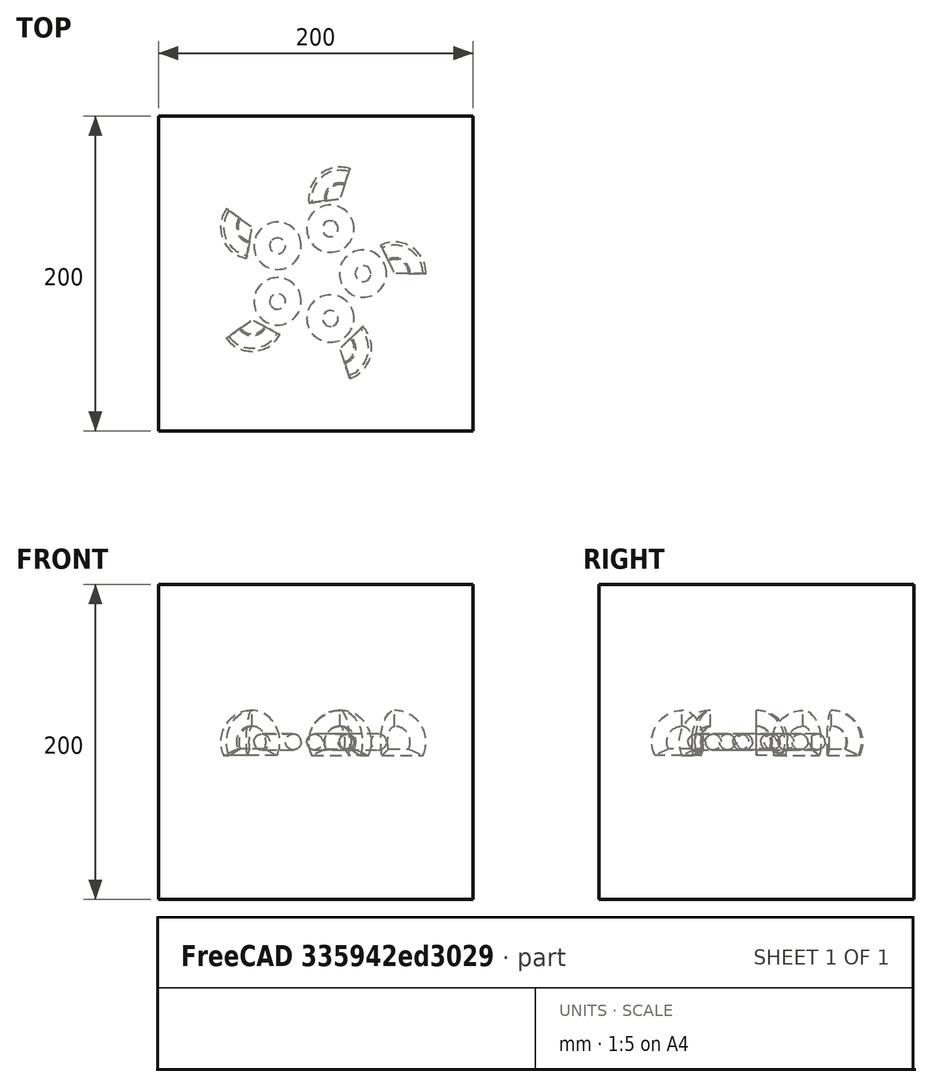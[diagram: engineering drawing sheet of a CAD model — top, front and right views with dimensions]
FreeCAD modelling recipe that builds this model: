
FCSTD DOCUMENT  (FreeCAD 1.0R39109 (Git))
Label: arrayTest-7
License: All rights reserved
LicenseURL: http://en.wikipedia.org/wiki/All_rights_reserved
objects: App::DocumentObjectGroupPython×1248, Part::FeaturePython×4, App::Part×2, Part::MultiFuse×1
note: 5 computed .brp shape members not serialized (recipe doc carries the construction recipe); baked Part::Feature solids carry a one-line shape summary decoded from their .brp

FEATURE [App::DocumentObjectGroupPython] HALFPI  # scripted group (container) (typed FeaturePython)
  name = HALFPI
  value = pi/2.
FEATURE [App::DocumentObjectGroupPython] PI  # scripted group (container) (typed FeaturePython)
  name = PI
  value = 1.*pi
FEATURE [App::DocumentObjectGroupPython] TWOPI  # scripted group (container) (typed FeaturePython)
  name = TWOPI
  value = 2.*pi
FEATURE [App::DocumentObjectGroupPython] Constants  # scripted group (container) (typed FeaturePython)
  Group = -> [HALFPI,PI,TWOPI]
FEATURE [App::DocumentObjectGroupPython] Variables  # scripted group (container) (typed FeaturePython)
FEATURE [App::DocumentObjectGroupPython] Quantities  # scripted group (container) (typed FeaturePython)
FEATURE [App::DocumentObjectGroupPython] Isotopes  # scripted group (container) (typed FeaturePython)
FEATURE [App::DocumentObjectGroupPython] Elements  # scripted group (container) (typed FeaturePython)
FEATURE [App::DocumentObjectGroupPython] G4Isotopes  # scripted group (container) (typed FeaturePython)
FEATURE [App::DocumentObjectGroupPython] H_element  # scripted group (container) (typed FeaturePython)
  Z = 1
  atom_value = 1.008
  formula = H
  name = H_element
FEATURE [App::DocumentObjectGroupPython] He_element  # scripted group (container) (typed FeaturePython)
  Z = 2
  atom_value = 4.0026
  formula = He
  name = He_element
FEATURE [App::DocumentObjectGroupPython] Li_element  # scripted group (container) (typed FeaturePython)
  Z = 3
  atom_value = 6.94
  formula = Li
  name = Li_element
FEATURE [App::DocumentObjectGroupPython] Be_element  # scripted group (container) (typed FeaturePython)
  Z = 4
  atom_value = 9.01218
  formula = Be
  name = Be_element
FEATURE [App::DocumentObjectGroupPython] B_element  # scripted group (container) (typed FeaturePython)
  Z = 5
  atom_value = 10.81
  formula = B
  name = B_element
FEATURE [App::DocumentObjectGroupPython] C_element  # scripted group (container) (typed FeaturePython)
  Z = 6
  atom_value = 12.011
  formula = C
  name = C_element
FEATURE [App::DocumentObjectGroupPython] N_element  # scripted group (container) (typed FeaturePython)
  Z = 7
  atom_value = 14.007
  formula = N
  name = N_element
FEATURE [App::DocumentObjectGroupPython] O_element  # scripted group (container) (typed FeaturePython)
  Z = 8
  atom_value = 15.999
  formula = O
  name = O_element
FEATURE [App::DocumentObjectGroupPython] F_element  # scripted group (container) (typed FeaturePython)
  Z = 9
  atom_value = 18.9984
  formula = F
  name = F_element
FEATURE [App::DocumentObjectGroupPython] Ne_element  # scripted group (container) (typed FeaturePython)
  Z = 10
  atom_value = 20.1797
  formula = Ne
  name = Ne_element
FEATURE [App::DocumentObjectGroupPython] Na_element  # scripted group (container) (typed FeaturePython)
  Z = 11
  atom_value = 22.9898
  formula = Na
  name = Na_element
FEATURE [App::DocumentObjectGroupPython] Mg_element  # scripted group (container) (typed FeaturePython)
  Z = 12
  atom_value = 24.305
  formula = Mg
  name = Mg_element
FEATURE [App::DocumentObjectGroupPython] Al_element  # scripted group (container) (typed FeaturePython)
  Z = 13
  atom_value = 26.9815
  formula = Al
  name = Al_element
FEATURE [App::DocumentObjectGroupPython] Si_element  # scripted group (container) (typed FeaturePython)
  Z = 14
  atom_value = 28.085
  formula = Si
  name = Si_element
FEATURE [App::DocumentObjectGroupPython] P_element  # scripted group (container) (typed FeaturePython)
  Z = 15
  atom_value = 30.9738
  formula = P
  name = P_element
FEATURE [App::DocumentObjectGroupPython] S_element  # scripted group (container) (typed FeaturePython)
  Z = 16
  atom_value = 32.06
  formula = S
  name = S_element
FEATURE [App::DocumentObjectGroupPython] Cl_element  # scripted group (container) (typed FeaturePython)
  Z = 17
  atom_value = 35.45
  formula = Cl
  name = Cl_element
FEATURE [App::DocumentObjectGroupPython] Ar_element  # scripted group (container) (typed FeaturePython)
  Z = 18
  atom_value = 39.95
  formula = Ar
  name = Ar_element
FEATURE [App::DocumentObjectGroupPython] K_element  # scripted group (container) (typed FeaturePython)
  Z = 19
  atom_value = 39.0983
  formula = K
  name = K_element
FEATURE [App::DocumentObjectGroupPython] Ca_element  # scripted group (container) (typed FeaturePython)
  Z = 20
  atom_value = 40.078
  formula = Ca
  name = Ca_element
FEATURE [App::DocumentObjectGroupPython] Sc_element  # scripted group (container) (typed FeaturePython)
  Z = 21
  atom_value = 44.9559
  formula = Sc
  name = Sc_element
FEATURE [App::DocumentObjectGroupPython] Ti_element  # scripted group (container) (typed FeaturePython)
  Z = 22
  atom_value = 47.867
  formula = Ti
  name = Ti_element
FEATURE [App::DocumentObjectGroupPython] V_element  # scripted group (container) (typed FeaturePython)
  Z = 23
  atom_value = 50.9415
  formula = V
  name = V_element
FEATURE [App::DocumentObjectGroupPython] Cr_element  # scripted group (container) (typed FeaturePython)
  Z = 24
  atom_value = 51.9961
  formula = Cr
  name = Cr_element
FEATURE [App::DocumentObjectGroupPython] Mn_element  # scripted group (container) (typed FeaturePython)
  Z = 25
  atom_value = 54.938
  formula = Mn
  name = Mn_element
FEATURE [App::DocumentObjectGroupPython] Fe_element  # scripted group (container) (typed FeaturePython)
  Z = 26
  atom_value = 55.845
  formula = Fe
  name = Fe_element
FEATURE [App::DocumentObjectGroupPython] Co_element  # scripted group (container) (typed FeaturePython)
  Z = 27
  atom_value = 58.9332
  formula = Co
  name = Co_element
FEATURE [App::DocumentObjectGroupPython] Ni_element  # scripted group (container) (typed FeaturePython)
  Z = 28
  atom_value = 58.6934
  formula = Ni
  name = Ni_element
FEATURE [App::DocumentObjectGroupPython] Cu_element  # scripted group (container) (typed FeaturePython)
  Z = 29
  atom_value = 63.546
  formula = Cu
  name = Cu_element
FEATURE [App::DocumentObjectGroupPython] Zn_element  # scripted group (container) (typed FeaturePython)
  Z = 30
  atom_value = 65.38
  formula = Zn
  name = Zn_element
FEATURE [App::DocumentObjectGroupPython] Ga_element  # scripted group (container) (typed FeaturePython)
  Z = 31
  atom_value = 69.723
  formula = Ga
  name = Ga_element
FEATURE [App::DocumentObjectGroupPython] Ge_element  # scripted group (container) (typed FeaturePython)
  Z = 32
  atom_value = 72.63
  formula = Ge
  name = Ge_element
FEATURE [App::DocumentObjectGroupPython] As_element  # scripted group (container) (typed FeaturePython)
  Z = 33
  atom_value = 74.9216
  formula = As
  name = As_element
FEATURE [App::DocumentObjectGroupPython] Se_element  # scripted group (container) (typed FeaturePython)
  Z = 34
  atom_value = 78.971
  formula = Se
  name = Se_element
FEATURE [App::DocumentObjectGroupPython] Br_element  # scripted group (container) (typed FeaturePython)
  Z = 35
  atom_value = 79.904
  formula = Br
  name = Br_element
FEATURE [App::DocumentObjectGroupPython] Kr_element  # scripted group (container) (typed FeaturePython)
  Z = 36
  atom_value = 83.798
  formula = Kr
  name = Kr_element
FEATURE [App::DocumentObjectGroupPython] Rb_element  # scripted group (container) (typed FeaturePython)
  Z = 37
  atom_value = 85.4678
  formula = Rb
  name = Rb_element
FEATURE [App::DocumentObjectGroupPython] Sr_element  # scripted group (container) (typed FeaturePython)
  Z = 38
  atom_value = 87.62
  formula = Sr
  name = Sr_element
FEATURE [App::DocumentObjectGroupPython] Y_element  # scripted group (container) (typed FeaturePython)
  Z = 39
  atom_value = 88.9058
  formula = Y
  name = Y_element
FEATURE [App::DocumentObjectGroupPython] Zr_element  # scripted group (container) (typed FeaturePython)
  Z = 40
  atom_value = 91.224
  formula = Zr
  name = Zr_element
FEATURE [App::DocumentObjectGroupPython] Nb_element  # scripted group (container) (typed FeaturePython)
  Z = 41
  atom_value = 92.9064
  formula = Nb
  name = Nb_element
FEATURE [App::DocumentObjectGroupPython] Mo_element  # scripted group (container) (typed FeaturePython)
  Z = 42
  atom_value = 95.95
  formula = Mo
  name = Mo_element
FEATURE [App::DocumentObjectGroupPython] Tc_element  # scripted group (container) (typed FeaturePython)
  Z = 43
  atom_value = 97
  formula = Tc
  name = Tc_element
FEATURE [App::DocumentObjectGroupPython] Ru_element  # scripted group (container) (typed FeaturePython)
  Z = 44
  atom_value = 101.07
  formula = Ru
  name = Ru_element
FEATURE [App::DocumentObjectGroupPython] Rh_element  # scripted group (container) (typed FeaturePython)
  Z = 45
  atom_value = 102.905
  formula = Rh
  name = Rh_element
FEATURE [App::DocumentObjectGroupPython] Pd_element  # scripted group (container) (typed FeaturePython)
  Z = 46
  atom_value = 106.42
  formula = Pd
  name = Pd_element
FEATURE [App::DocumentObjectGroupPython] Ag_element  # scripted group (container) (typed FeaturePython)
  Z = 47
  atom_value = 107.868
  formula = Ag
  name = Ag_element
FEATURE [App::DocumentObjectGroupPython] Cd_element  # scripted group (container) (typed FeaturePython)
  Z = 48
  atom_value = 112.414
  formula = Cd
  name = Cd_element
FEATURE [App::DocumentObjectGroupPython] In_element  # scripted group (container) (typed FeaturePython)
  Z = 49
  atom_value = 114.818
  formula = In
  name = In_element
FEATURE [App::DocumentObjectGroupPython] Sn_element  # scripted group (container) (typed FeaturePython)
  Z = 50
  atom_value = 118.71
  formula = Sn
  name = Sn_element
FEATURE [App::DocumentObjectGroupPython] Sb_element  # scripted group (container) (typed FeaturePython)
  Z = 51
  atom_value = 121.76
  formula = Sb
  name = Sb_element
FEATURE [App::DocumentObjectGroupPython] Te_element  # scripted group (container) (typed FeaturePython)
  Z = 52
  atom_value = 127.6
  formula = Te
  name = Te_element
FEATURE [App::DocumentObjectGroupPython] I_element  # scripted group (container) (typed FeaturePython)
  Z = 53
  atom_value = 126.904
  formula = I
  name = I_element
FEATURE [App::DocumentObjectGroupPython] Xe_element  # scripted group (container) (typed FeaturePython)
  Z = 54
  atom_value = 131.293
  formula = Xe
  name = Xe_element
FEATURE [App::DocumentObjectGroupPython] Cs_element  # scripted group (container) (typed FeaturePython)
  Z = 55
  atom_value = 132.905
  formula = Cs
  name = Cs_element
FEATURE [App::DocumentObjectGroupPython] Ba_element  # scripted group (container) (typed FeaturePython)
  Z = 56
  atom_value = 137.327
  formula = Ba
  name = Ba_element
FEATURE [App::DocumentObjectGroupPython] La_element  # scripted group (container) (typed FeaturePython)
  Z = 57
  atom_value = 138.905
  formula = La
  name = La_element
FEATURE [App::DocumentObjectGroupPython] Ce_element  # scripted group (container) (typed FeaturePython)
  Z = 58
  atom_value = 140.116
  formula = Ce
  name = Ce_element
FEATURE [App::DocumentObjectGroupPython] Pr_element  # scripted group (container) (typed FeaturePython)
  Z = 59
  atom_value = 140.908
  formula = Pr
  name = Pr_element
FEATURE [App::DocumentObjectGroupPython] Nd_element  # scripted group (container) (typed FeaturePython)
  Z = 60
  atom_value = 144.242
  formula = Nd
  name = Nd_element
FEATURE [App::DocumentObjectGroupPython] Pm_element  # scripted group (container) (typed FeaturePython)
  Z = 61
  atom_value = 145
  formula = Pm
  name = Pm_element
FEATURE [App::DocumentObjectGroupPython] Sm_element  # scripted group (container) (typed FeaturePython)
  Z = 62
  atom_value = 150.36
  formula = Sm
  name = Sm_element
FEATURE [App::DocumentObjectGroupPython] Eu_element  # scripted group (container) (typed FeaturePython)
  Z = 63
  atom_value = 151.964
  formula = Eu
  name = Eu_element
FEATURE [App::DocumentObjectGroupPython] Gd_element  # scripted group (container) (typed FeaturePython)
  Z = 64
  atom_value = 157.25
  formula = Gd
  name = Gd_element
FEATURE [App::DocumentObjectGroupPython] Tb_element  # scripted group (container) (typed FeaturePython)
  Z = 65
  atom_value = 158.925
  formula = Tb
  name = Tb_element
FEATURE [App::DocumentObjectGroupPython] Dy_element  # scripted group (container) (typed FeaturePython)
  Z = 66
  atom_value = 162.5
  formula = Dy
  name = Dy_element
FEATURE [App::DocumentObjectGroupPython] Ho_element  # scripted group (container) (typed FeaturePython)
  Z = 67
  atom_value = 164.93
  formula = Ho
  name = Ho_element
FEATURE [App::DocumentObjectGroupPython] Er_element  # scripted group (container) (typed FeaturePython)
  Z = 68
  atom_value = 167.259
  formula = Er
  name = Er_element
FEATURE [App::DocumentObjectGroupPython] Tm_element  # scripted group (container) (typed FeaturePython)
  Z = 69
  atom_value = 168.934
  formula = Tm
  name = Tm_element
FEATURE [App::DocumentObjectGroupPython] Yb_element  # scripted group (container) (typed FeaturePython)
  Z = 70
  atom_value = 173.045
  formula = Yb
  name = Yb_element
FEATURE [App::DocumentObjectGroupPython] Lu_element  # scripted group (container) (typed FeaturePython)
  Z = 71
  atom_value = 174.967
  formula = Lu
  name = Lu_element
FEATURE [App::DocumentObjectGroupPython] Hf_element  # scripted group (container) (typed FeaturePython)
  Z = 72
  atom_value = 178.49
  formula = Hf
  name = Hf_element
FEATURE [App::DocumentObjectGroupPython] Ta_element  # scripted group (container) (typed FeaturePython)
  Z = 73
  atom_value = 180.948
  formula = Ta
  name = Ta_element
FEATURE [App::DocumentObjectGroupPython] W_element  # scripted group (container) (typed FeaturePython)
  Z = 74
  atom_value = 183.84
  formula = W
  name = W_element
FEATURE [App::DocumentObjectGroupPython] Re_element  # scripted group (container) (typed FeaturePython)
  Z = 75
  atom_value = 186.207
  formula = Re
  name = Re_element
FEATURE [App::DocumentObjectGroupPython] Os_element  # scripted group (container) (typed FeaturePython)
  Z = 76
  atom_value = 190.23
  formula = Os
  name = Os_element
FEATURE [App::DocumentObjectGroupPython] Ir_element  # scripted group (container) (typed FeaturePython)
  Z = 77
  atom_value = 192.217
  formula = Ir
  name = Ir_element
FEATURE [App::DocumentObjectGroupPython] Pt_element  # scripted group (container) (typed FeaturePython)
  Z = 78
  atom_value = 195.084
  formula = Pt
  name = Pt_element
FEATURE [App::DocumentObjectGroupPython] Au_element  # scripted group (container) (typed FeaturePython)
  Z = 79
  atom_value = 196.967
  formula = Au
  name = Au_element
FEATURE [App::DocumentObjectGroupPython] Hg_element  # scripted group (container) (typed FeaturePython)
  Z = 80
  atom_value = 200.592
  formula = Hg
  name = Hg_element
FEATURE [App::DocumentObjectGroupPython] Tl_element  # scripted group (container) (typed FeaturePython)
  Z = 81
  atom_value = 204.38
  formula = Tl
  name = Tl_element
FEATURE [App::DocumentObjectGroupPython] Pb_element  # scripted group (container) (typed FeaturePython)
  Z = 82
  atom_value = 207.2
  formula = Pb
  name = Pb_element
FEATURE [App::DocumentObjectGroupPython] Bi_element  # scripted group (container) (typed FeaturePython)
  Z = 83
  atom_value = 208.98
  formula = Bi
  name = Bi_element
FEATURE [App::DocumentObjectGroupPython] Po_element  # scripted group (container) (typed FeaturePython)
  Z = 84
  atom_value = 209
  formula = Po
  name = Po_element
FEATURE [App::DocumentObjectGroupPython] At_element  # scripted group (container) (typed FeaturePython)
  Z = 85
  atom_value = 210
  formula = At
  name = At_element
FEATURE [App::DocumentObjectGroupPython] Rn_element  # scripted group (container) (typed FeaturePython)
  Z = 86
  atom_value = 222
  formula = Rn
  name = Rn_element
FEATURE [App::DocumentObjectGroupPython] Fr_element  # scripted group (container) (typed FeaturePython)
  Z = 87
  atom_value = 223
  formula = Fr
  name = Fr_element
FEATURE [App::DocumentObjectGroupPython] Ra_element  # scripted group (container) (typed FeaturePython)
  Z = 88
  atom_value = 226
  formula = Ra
  name = Ra_element
FEATURE [App::DocumentObjectGroupPython] Ac_element  # scripted group (container) (typed FeaturePython)
  Z = 89
  atom_value = 227
  formula = Ac
  name = Ac_element
FEATURE [App::DocumentObjectGroupPython] Th_element  # scripted group (container) (typed FeaturePython)
  Z = 90
  atom_value = 232.038
  formula = Th
  name = Th_element
FEATURE [App::DocumentObjectGroupPython] Pa_element  # scripted group (container) (typed FeaturePython)
  Z = 91
  atom_value = 231.036
  formula = Pa
  name = Pa_element
FEATURE [App::DocumentObjectGroupPython] U_element  # scripted group (container) (typed FeaturePython)
  Z = 92
  atom_value = 238.029
  formula = U
  name = U_element
FEATURE [App::DocumentObjectGroupPython] Np_element  # scripted group (container) (typed FeaturePython)
  Z = 93
  atom_value = 237
  formula = Np
  name = Np_element
FEATURE [App::DocumentObjectGroupPython] Pu_element  # scripted group (container) (typed FeaturePython)
  Z = 94
  atom_value = 244
  formula = Pu
  name = Pu_element
FEATURE [App::DocumentObjectGroupPython] Am_element  # scripted group (container) (typed FeaturePython)
  Z = 95
  atom_value = 243
  formula = Am
  name = Am_element
FEATURE [App::DocumentObjectGroupPython] Cm_element  # scripted group (container) (typed FeaturePython)
  Z = 96
  atom_value = 247
  formula = Cm
  name = Cm_element
FEATURE [App::DocumentObjectGroupPython] Bk_element  # scripted group (container) (typed FeaturePython)
  Z = 97
  atom_value = 247
  formula = Bk
  name = Bk_element
FEATURE [App::DocumentObjectGroupPython] Cf_element  # scripted group (container) (typed FeaturePython)
  Z = 98
  atom_value = 251
  formula = Cf
  name = Cf_element
FEATURE [App::DocumentObjectGroupPython] G4Elements  # scripted group (container) (typed FeaturePython)
  Group = -> [H_element,He_element,Li_element,Be_element,B_element,C_element,N_element,O_element,F_element,Ne_element,Na_element,Mg_element,Al_element,Si_element,P_element,S_element,Cl_element,Ar_element,K_element,Ca_element,Sc_element,Ti_element,V_element,Cr_element,Mn_element,Fe_element,Co_element,Ni_element,Cu_element,Zn_element,Ga_element,Ge_element,As_element,Se_element,Br_element,Kr_element,Rb_element,+61 more]
FEATURE [App::DocumentObjectGroupPython] H_element001  label="H_element : 0.101"  # scripted group (container) (typed FeaturePython)
  n = 0.101327
FEATURE [App::DocumentObjectGroupPython] C_element001  label="C_element : 0.775"  # scripted group (container) (typed FeaturePython)
  n = 0.7755
FEATURE [App::DocumentObjectGroupPython] N_element001  label="N_element : 0.035"  # scripted group (container) (typed FeaturePython)
  n = 0.035057
FEATURE [App::DocumentObjectGroupPython] O_element001  label="O_element : 0.052"  # scripted group (container) (typed FeaturePython)
  n = 0.0523159
FEATURE [App::DocumentObjectGroupPython] F_element001  label="F_element : 0.017"  # scripted group (container) (typed FeaturePython)
  n = 0.017422
FEATURE [App::DocumentObjectGroupPython] Ca_element001  label="Ca_element : 0.018"  # scripted group (container) (typed FeaturePython)
  n = 0.018378
FEATURE [App::DocumentObjectGroupPython] G4_A_150_TISSUE  label="G4_A-150_TISSUE"  # scripted group (container) (typed FeaturePython)
  Dunit = g/cm3
  Dvalue = 1.127
  Group = -> [H_element001,C_element001,N_element001,O_element001,F_element001,Ca_element001]
  conduct = 2
  density = 1
  expand = 3
  formula = G4_A-150_TISSUE
  name = G4_A-150_TISSUE
  specific = 4
FEATURE [App::DocumentObjectGroupPython] C_element002  label="C_element : 3"  # scripted group (container) (typed FeaturePython)
  n = 3
  ref = C_element
FEATURE [App::DocumentObjectGroupPython] H_element002  label="H_element : 6"  # scripted group (container) (typed FeaturePython)
  n = 6
  ref = H_element
FEATURE [App::DocumentObjectGroupPython] O_element002  label="O_element : 1"  # scripted group (container) (typed FeaturePython)
  n = 1
  ref = O_element
FEATURE [App::DocumentObjectGroupPython] G4_ACETONE  # scripted group (container) (typed FeaturePython)
  Dunit = g/cm3
  Dvalue = 0.7899
  Group = -> [C_element002,H_element002,O_element002]
  conduct = 2
  density = 1
  expand = 3
  formula = G4_ACETONE
  name = G4_ACETONE
  specific = 4
FEATURE [App::DocumentObjectGroupPython] C_element003  label="C_element : 2"  # scripted group (container) (typed FeaturePython)
  n = 2
  ref = C_element
FEATURE [App::DocumentObjectGroupPython] H_element003  label="H_element : 2"  # scripted group (container) (typed FeaturePython)
  n = 2
  ref = H_element
FEATURE [App::DocumentObjectGroupPython] G4_ACETYLENE  # scripted group (container) (typed FeaturePython)
  Dunit = g/cm3
  Dvalue = 0.0010967
  Group = -> [C_element003,H_element003]
  conduct = 2
  density = 1
  expand = 3
  formula = G4_ACETYLENE
  name = G4_ACETYLENE
  specific = 4
FEATURE [App::DocumentObjectGroupPython] C_element004  label="C_element : 5"  # scripted group (container) (typed FeaturePython)
  n = 5
  ref = C_element
FEATURE [App::DocumentObjectGroupPython] H_element004  label="H_element : 5"  # scripted group (container) (typed FeaturePython)
  n = 5
  ref = H_element
FEATURE [App::DocumentObjectGroupPython] N_element002  label="N_element : 5"  # scripted group (container) (typed FeaturePython)
  n = 5
  ref = N_element
FEATURE [App::DocumentObjectGroupPython] G4_ADENINE  # scripted group (container) (typed FeaturePython)
  Dunit = g/cm3
  Dvalue = 1.6
  Group = -> [C_element004,H_element004,N_element002]
  conduct = 2
  density = 1
  expand = 3
  formula = G4_ADENINE
  name = G4_ADENINE
  specific = 4
FEATURE [App::DocumentObjectGroupPython] H_element005  label="H_element : 0.114"  # scripted group (container) (typed FeaturePython)
  n = 0.114
FEATURE [App::DocumentObjectGroupPython] C_element005  label="C_element : 0.598"  # scripted group (container) (typed FeaturePython)
  n = 0.598
FEATURE [App::DocumentObjectGroupPython] N_element003  label="N_element : 0.007"  # scripted group (container) (typed FeaturePython)
  n = 0.007
FEATURE [App::DocumentObjectGroupPython] O_element003  label="O_element : 0.278"  # scripted group (container) (typed FeaturePython)
  n = 0.278
FEATURE [App::DocumentObjectGroupPython] Na_element001  label="Na_element : 0.001"  # scripted group (container) (typed FeaturePython)
  n = 0.001
FEATURE [App::DocumentObjectGroupPython] S_element001  label="S_element : 0.001"  # scripted group (container) (typed FeaturePython)
  n = 0.001
FEATURE [App::DocumentObjectGroupPython] Cl_element001  label="Cl_element : 0.001"  # scripted group (container) (typed FeaturePython)
  n = 0.001
FEATURE [App::DocumentObjectGroupPython] G4_ADIPOSE_TISSUE_ICRP  # scripted group (container) (typed FeaturePython)
  Dunit = g/cm3
  Dvalue = 0.95
  Group = -> [H_element005,C_element005,N_element003,O_element003,Na_element001,S_element001,Cl_element001]
  conduct = 2
  density = 1
  expand = 3
  formula = G4_ADIPOSE_TISSUE_ICRP
  name = G4_ADIPOSE_TISSUE_ICRP
  specific = 4
FEATURE [App::DocumentObjectGroupPython] C_element006  label="C_element : 0.000"  # scripted group (container) (typed FeaturePython)
  n = 0.000124
FEATURE [App::DocumentObjectGroupPython] N_element004  label="N_element : 0.755"  # scripted group (container) (typed FeaturePython)
  n = 0.755268
FEATURE [App::DocumentObjectGroupPython] O_element004  label="O_element : 0.232"  # scripted group (container) (typed FeaturePython)
  n = 0.231781
FEATURE [App::DocumentObjectGroupPython] Ar_element001  label="Ar_element : 0.013"  # scripted group (container) (typed FeaturePython)
  n = 0.012827
FEATURE [App::DocumentObjectGroupPython] G4_AIR  # scripted group (container) (typed FeaturePython)
  Dunit = g/cm3
  Dvalue = 0.00120479
  Group = -> [C_element006,N_element004,O_element004,Ar_element001]
  conduct = 2
  density = 1
  expand = 3
  formula = G4_AIR
  name = G4_AIR
  specific = 4
FEATURE [App::DocumentObjectGroupPython] C_element007  label="C_element : 006"  # scripted group (container) (typed FeaturePython)
  n = 3
  ref = C_element
FEATURE [App::DocumentObjectGroupPython] H_element006  label="H_element : 7"  # scripted group (container) (typed FeaturePython)
  n = 7
  ref = H_element
FEATURE [App::DocumentObjectGroupPython] N_element005  label="N_element : 1"  # scripted group (container) (typed FeaturePython)
  n = 1
  ref = N_element
FEATURE [App::DocumentObjectGroupPython] O_element005  label="O_element : 2"  # scripted group (container) (typed FeaturePython)
  n = 2
  ref = O_element
FEATURE [App::DocumentObjectGroupPython] G4_ALANINE  # scripted group (container) (typed FeaturePython)
  Dunit = g/cm3
  Dvalue = 1.42
  Group = -> [C_element007,H_element006,N_element005,O_element005]
  conduct = 2
  density = 1
  expand = 3
  formula = G4_ALANINE
  name = G4_ALANINE
  specific = 4
FEATURE [App::DocumentObjectGroupPython] Al_element001  label="Al_element : 2"  # scripted group (container) (typed FeaturePython)
  n = 2
  ref = Al_element
FEATURE [App::DocumentObjectGroupPython] O_element006  label="O_element : 3"  # scripted group (container) (typed FeaturePython)
  n = 3
  ref = O_element
FEATURE [App::DocumentObjectGroupPython] G4_ALUMINUM_OXIDE  # scripted group (container) (typed FeaturePython)
  Dunit = g/cm3
  Dvalue = 3.97
  Group = -> [Al_element001,O_element006]
  conduct = 2
  density = 1
  expand = 3
  formula = G4_ALUMINUM_OXIDE
  name = G4_ALUMINUM_OXIDE
  specific = 4
FEATURE [App::DocumentObjectGroupPython] H_element007  label="H_element : 0.106"  # scripted group (container) (typed FeaturePython)
  n = 0.10593
FEATURE [App::DocumentObjectGroupPython] C_element008  label="C_element : 0.789"  # scripted group (container) (typed FeaturePython)
  n = 0.788974
FEATURE [App::DocumentObjectGroupPython] O_element007  label="O_element : 0.105"  # scripted group (container) (typed FeaturePython)
  n = 0.105096
FEATURE [App::DocumentObjectGroupPython] G4_AMBER  # scripted group (container) (typed FeaturePython)
  Dunit = g/cm3
  Dvalue = 1.1
  Group = -> [H_element007,C_element008,O_element007]
  conduct = 2
  density = 1
  expand = 3
  formula = G4_AMBER
  name = G4_AMBER
  specific = 4
FEATURE [App::DocumentObjectGroupPython] N_element006  label="N_element : 006"  # scripted group (container) (typed FeaturePython)
  n = 1
  ref = N_element
FEATURE [App::DocumentObjectGroupPython] H_element008  label="H_element : 3"  # scripted group (container) (typed FeaturePython)
  n = 3
  ref = H_element
FEATURE [App::DocumentObjectGroupPython] G4_AMMONIA  # scripted group (container) (typed FeaturePython)
  Dunit = g/cm3
  Dvalue = 0.000826019
  Group = -> [N_element006,H_element008]
  conduct = 2
  density = 1
  expand = 3
  formula = G4_AMMONIA
  name = G4_AMMONIA
  specific = 4
FEATURE [App::DocumentObjectGroupPython] C_element009  label="C_element : 6"  # scripted group (container) (typed FeaturePython)
  n = 6
  ref = C_element
FEATURE [App::DocumentObjectGroupPython] H_element009  label="H_element : 008"  # scripted group (container) (typed FeaturePython)
  n = 7
  ref = H_element
FEATURE [App::DocumentObjectGroupPython] N_element007  label="N_element : 007"  # scripted group (container) (typed FeaturePython)
  n = 1
  ref = N_element
FEATURE [App::DocumentObjectGroupPython] G4_ANILINE  # scripted group (container) (typed FeaturePython)
  Dunit = g/cm3
  Dvalue = 1.0235
  Group = -> [C_element009,H_element009,N_element007]
  conduct = 2
  density = 1
  expand = 3
  formula = G4_ANILINE
  name = G4_ANILINE
  specific = 4
FEATURE [App::DocumentObjectGroupPython] C_element010  label="C_element : 14"  # scripted group (container) (typed FeaturePython)
  n = 14
  ref = C_element
FEATURE [App::DocumentObjectGroupPython] H_element010  label="H_element : 10"  # scripted group (container) (typed FeaturePython)
  n = 10
  ref = H_element
FEATURE [App::DocumentObjectGroupPython] G4_ANTHRACENE  # scripted group (container) (typed FeaturePython)
  Dunit = g/cm3
  Dvalue = 1.283
  Group = -> [C_element010,H_element010]
  conduct = 2
  density = 1
  expand = 3
  formula = G4_ANTHRACENE
  name = G4_ANTHRACENE
  specific = 4
FEATURE [App::DocumentObjectGroupPython] H_element011  label="H_element : 0.065"  # scripted group (container) (typed FeaturePython)
  n = 0.0654709
FEATURE [App::DocumentObjectGroupPython] C_element011  label="C_element : 0.537"  # scripted group (container) (typed FeaturePython)
  n = 0.536944
FEATURE [App::DocumentObjectGroupPython] N_element008  label="N_element : 0.021"  # scripted group (container) (typed FeaturePython)
  n = 0.0215
FEATURE [App::DocumentObjectGroupPython] O_element008  label="O_element : 0.032"  # scripted group (container) (typed FeaturePython)
  n = 0.032085
FEATURE [App::DocumentObjectGroupPython] F_element002  label="F_element : 0.167"  # scripted group (container) (typed FeaturePython)
  n = 0.167411
FEATURE [App::DocumentObjectGroupPython] Ca_element002  label="Ca_element : 0.177"  # scripted group (container) (typed FeaturePython)
  n = 0.176589
FEATURE [App::DocumentObjectGroupPython] G4_B_100_BONE  label="G4_B-100_BONE"  # scripted group (container) (typed FeaturePython)
  Dunit = g/cm3
  Dvalue = 1.45
  Group = -> [H_element011,C_element011,N_element008,O_element008,F_element002,Ca_element002]
  conduct = 2
  density = 1
  expand = 3
  formula = G4_B-100_BONE
  name = G4_B-100_BONE
  specific = 4
FEATURE [App::DocumentObjectGroupPython] H_element012  label="H_element : 0.057"  # scripted group (container) (typed FeaturePython)
  n = 0.057441
FEATURE [App::DocumentObjectGroupPython] C_element012  label="C_element : 0.790"  # scripted group (container) (typed FeaturePython)
  n = 0.774591
FEATURE [App::DocumentObjectGroupPython] O_element009  label="O_element : 0.168"  # scripted group (container) (typed FeaturePython)
  n = 0.167968
FEATURE [App::DocumentObjectGroupPython] G4_BAKELITE  # scripted group (container) (typed FeaturePython)
  Dunit = g/cm3
  Dvalue = 1.25
  Group = -> [H_element012,C_element012,O_element009]
  conduct = 2
  density = 1
  expand = 3
  formula = G4_BAKELITE
  name = G4_BAKELITE
  specific = 4
FEATURE [App::DocumentObjectGroupPython] Ba_element001  label="Ba_element : 1"  # scripted group (container) (typed FeaturePython)
  n = 1
  ref = Ba_element
FEATURE [App::DocumentObjectGroupPython] F_element003  label="F_element : 2"  # scripted group (container) (typed FeaturePython)
  n = 2
  ref = F_element
FEATURE [App::DocumentObjectGroupPython] G4_BARIUM_FLUORIDE  # scripted group (container) (typed FeaturePython)
  Dunit = g/cm3
  Dvalue = 4.89
  Group = -> [Ba_element001,F_element003]
  conduct = 2
  density = 1
  expand = 3
  formula = G4_BARIUM_FLUORIDE
  name = G4_BARIUM_FLUORIDE
  specific = 4
FEATURE [App::DocumentObjectGroupPython] Ba_element002  label="Ba_element : 002"  # scripted group (container) (typed FeaturePython)
  n = 1
  ref = Ba_element
FEATURE [App::DocumentObjectGroupPython] S_element002  label="S_element : 1"  # scripted group (container) (typed FeaturePython)
  n = 1
  ref = S_element
FEATURE [App::DocumentObjectGroupPython] O_element010  label="O_element : 4"  # scripted group (container) (typed FeaturePython)
  n = 4
  ref = O_element
FEATURE [App::DocumentObjectGroupPython] G4_BARIUM_SULFATE  # scripted group (container) (typed FeaturePython)
  Dunit = g/cm3
  Dvalue = 4.5
  Group = -> [Ba_element002,S_element002,O_element010]
  conduct = 2
  density = 1
  expand = 3
  formula = G4_BARIUM_SULFATE
  name = G4_BARIUM_SULFATE
  specific = 4
FEATURE [App::DocumentObjectGroupPython] C_element013  label="C_element : 007"  # scripted group (container) (typed FeaturePython)
  n = 6
  ref = C_element
FEATURE [App::DocumentObjectGroupPython] H_element013  label="H_element : 009"  # scripted group (container) (typed FeaturePython)
  n = 6
  ref = H_element
FEATURE [App::DocumentObjectGroupPython] G4_BENZENE  # scripted group (container) (typed FeaturePython)
  Dunit = g/cm3
  Dvalue = 0.87865
  Group = -> [C_element013,H_element013]
  conduct = 2
  density = 1
  expand = 3
  formula = G4_BENZENE
  name = G4_BENZENE
  specific = 4
FEATURE [App::DocumentObjectGroupPython] Be_element001  label="Be_element : 1"  # scripted group (container) (typed FeaturePython)
  n = 1
  ref = Be_element
FEATURE [App::DocumentObjectGroupPython] O_element011  label="O_element : 005"  # scripted group (container) (typed FeaturePython)
  n = 1
  ref = O_element
FEATURE [App::DocumentObjectGroupPython] G4_BERYLLIUM_OXIDE  # scripted group (container) (typed FeaturePython)
  Dunit = g/cm3
  Dvalue = 3.01
  Group = -> [Be_element001,O_element011]
  conduct = 2
  density = 1
  expand = 3
  formula = G4_BERYLLIUM_OXIDE
  name = G4_BERYLLIUM_OXIDE
  specific = 4
FEATURE [App::DocumentObjectGroupPython] Bi_element001  label="Bi_element : 4"  # scripted group (container) (typed FeaturePython)
  n = 4
  ref = Bi_element
FEATURE [App::DocumentObjectGroupPython] Ge_element001  label="Ge_element : 3"  # scripted group (container) (typed FeaturePython)
  n = 3
  ref = Ge_element
FEATURE [App::DocumentObjectGroupPython] O_element012  label="O_element : 12"  # scripted group (container) (typed FeaturePython)
  n = 12
  ref = O_element
FEATURE [App::DocumentObjectGroupPython] G4_BGO  # scripted group (container) (typed FeaturePython)
  Dunit = g/cm3
  Dvalue = 7.13
  Group = -> [Bi_element001,Ge_element001,O_element012]
  conduct = 2
  density = 1
  expand = 3
  formula = G4_BGO
  name = G4_BGO
  specific = 4
FEATURE [App::DocumentObjectGroupPython] H_element014  label="H_element : 0.102"  # scripted group (container) (typed FeaturePython)
  n = 0.102
FEATURE [App::DocumentObjectGroupPython] C_element014  label="C_element : 0.110"  # scripted group (container) (typed FeaturePython)
  n = 0.11
FEATURE [App::DocumentObjectGroupPython] N_element009  label="N_element : 0.033"  # scripted group (container) (typed FeaturePython)
  n = 0.033
FEATURE [App::DocumentObjectGroupPython] O_element013  label="O_element : 0.745"  # scripted group (container) (typed FeaturePython)
  n = 0.745
FEATURE [App::DocumentObjectGroupPython] Na_element002  label="Na_element : 0.002"  # scripted group (container) (typed FeaturePython)
  n = 0.001
FEATURE [App::DocumentObjectGroupPython] P_element001  label="P_element : 0.001"  # scripted group (container) (typed FeaturePython)
  n = 0.001
FEATURE [App::DocumentObjectGroupPython] S_element003  label="S_element : 0.002"  # scripted group (container) (typed FeaturePython)
  n = 0.002
FEATURE [App::DocumentObjectGroupPython] Cl_element002  label="Cl_element : 0.003"  # scripted group (container) (typed FeaturePython)
  n = 0.003
FEATURE [App::DocumentObjectGroupPython] K_element001  label="K_element : 0.002"  # scripted group (container) (typed FeaturePython)
  n = 0.002
FEATURE [App::DocumentObjectGroupPython] Fe_element001  label="Fe_element : 0.001"  # scripted group (container) (typed FeaturePython)
  n = 0.001
FEATURE [App::DocumentObjectGroupPython] G4_BLOOD_ICRP  # scripted group (container) (typed FeaturePython)
  Dunit = g/cm3
  Dvalue = 1.06
  Group = -> [H_element014,C_element014,N_element009,O_element013,Na_element002,P_element001,S_element003,Cl_element002,K_element001,Fe_element001]
  conduct = 2
  density = 1
  expand = 3
  formula = G4_BLOOD_ICRP
  name = G4_BLOOD_ICRP
  specific = 4
FEATURE [App::DocumentObjectGroupPython] H_element015  label="H_element : 0.064"  # scripted group (container) (typed FeaturePython)
  n = 0.064
FEATURE [App::DocumentObjectGroupPython] C_element015  label="C_element : 0.278"  # scripted group (container) (typed FeaturePython)
  n = 0.278
FEATURE [App::DocumentObjectGroupPython] N_element010  label="N_element : 0.027"  # scripted group (container) (typed FeaturePython)
  n = 0.027
FEATURE [App::DocumentObjectGroupPython] O_element014  label="O_element : 0.410"  # scripted group (container) (typed FeaturePython)
  n = 0.41
FEATURE [App::DocumentObjectGroupPython] Mg_element001  label="Mg_element : 0.002"  # scripted group (container) (typed FeaturePython)
  n = 0.002
FEATURE [App::DocumentObjectGroupPython] P_element002  label="P_element : 0.070"  # scripted group (container) (typed FeaturePython)
  n = 0.07
FEATURE [App::DocumentObjectGroupPython] S_element004  label="S_element : 0.003"  # scripted group (container) (typed FeaturePython)
  n = 0.002
FEATURE [App::DocumentObjectGroupPython] Ca_element003  label="Ca_element : 0.147"  # scripted group (container) (typed FeaturePython)
  n = 0.147
FEATURE [App::DocumentObjectGroupPython] G4_BONE_COMPACT_ICRU  # scripted group (container) (typed FeaturePython)
  Dunit = g/cm3
  Dvalue = 1.85
  Group = -> [H_element015,C_element015,N_element010,O_element014,Mg_element001,P_element002,S_element004,Ca_element003]
  conduct = 2
  density = 1
  expand = 3
  formula = G4_BONE_COMPACT_ICRU
  name = G4_BONE_COMPACT_ICRU
  specific = 4
FEATURE [App::DocumentObjectGroupPython] H_element016  label="H_element : 0.034"  # scripted group (container) (typed FeaturePython)
  n = 0.034
FEATURE [App::DocumentObjectGroupPython] C_element016  label="C_element : 0.155"  # scripted group (container) (typed FeaturePython)
  n = 0.155
FEATURE [App::DocumentObjectGroupPython] N_element011  label="N_element : 0.042"  # scripted group (container) (typed FeaturePython)
  n = 0.042
FEATURE [App::DocumentObjectGroupPython] O_element015  label="O_element : 0.435"  # scripted group (container) (typed FeaturePython)
  n = 0.435
FEATURE [App::DocumentObjectGroupPython] Na_element003  label="Na_element : 0.003"  # scripted group (container) (typed FeaturePython)
  n = 0.001
FEATURE [App::DocumentObjectGroupPython] Mg_element002  label="Mg_element : 0.003"  # scripted group (container) (typed FeaturePython)
  n = 0.002
FEATURE [App::DocumentObjectGroupPython] P_element003  label="P_element : 0.103"  # scripted group (container) (typed FeaturePython)
  n = 0.103
FEATURE [App::DocumentObjectGroupPython] S_element005  label="S_element : 0.004"  # scripted group (container) (typed FeaturePython)
  n = 0.003
FEATURE [App::DocumentObjectGroupPython] Ca_element004  label="Ca_element : 0.225"  # scripted group (container) (typed FeaturePython)
  n = 0.225
FEATURE [App::DocumentObjectGroupPython] G4_BONE_CORTICAL_ICRP  # scripted group (container) (typed FeaturePython)
  Dunit = g/cm3
  Dvalue = 1.92
  Group = -> [H_element016,C_element016,N_element011,O_element015,Na_element003,Mg_element002,P_element003,S_element005,Ca_element004]
  conduct = 2
  density = 1
  expand = 3
  formula = G4_BONE_CORTICAL_ICRP
  name = G4_BONE_CORTICAL_ICRP
  specific = 4
FEATURE [App::DocumentObjectGroupPython] B_element001  label="B_element : 4"  # scripted group (container) (typed FeaturePython)
  n = 4
  ref = B_element
FEATURE [App::DocumentObjectGroupPython] C_element017  label="C_element : 1"  # scripted group (container) (typed FeaturePython)
  n = 1
  ref = C_element
FEATURE [App::DocumentObjectGroupPython] G4_BORON_CARBIDE  # scripted group (container) (typed FeaturePython)
  Dunit = g/cm3
  Dvalue = 2.52
  Group = -> [B_element001,C_element017]
  conduct = 2
  density = 1
  expand = 3
  formula = G4_BORON_CARBIDE
  name = G4_BORON_CARBIDE
  specific = 4
FEATURE [App::DocumentObjectGroupPython] B_element002  label="B_element : 2"  # scripted group (container) (typed FeaturePython)
  n = 2
  ref = B_element
FEATURE [App::DocumentObjectGroupPython] O_element016  label="O_element : 006"  # scripted group (container) (typed FeaturePython)
  n = 3
  ref = O_element
FEATURE [App::DocumentObjectGroupPython] G4_BORON_OXIDE  # scripted group (container) (typed FeaturePython)
  Dunit = g/cm3
  Dvalue = 1.812
  Group = -> [B_element002,O_element016]
  conduct = 2
  density = 1
  expand = 3
  formula = G4_BORON_OXIDE
  name = G4_BORON_OXIDE
  specific = 4
FEATURE [App::DocumentObjectGroupPython] H_element017  label="H_element : 0.107"  # scripted group (container) (typed FeaturePython)
  n = 0.107
FEATURE [App::DocumentObjectGroupPython] C_element018  label="C_element : 0.145"  # scripted group (container) (typed FeaturePython)
  n = 0.145
FEATURE [App::DocumentObjectGroupPython] N_element012  label="N_element : 0.022"  # scripted group (container) (typed FeaturePython)
  n = 0.022
FEATURE [App::DocumentObjectGroupPython] O_element017  label="O_element : 0.712"  # scripted group (container) (typed FeaturePython)
  n = 0.712
FEATURE [App::DocumentObjectGroupPython] Na_element004  label="Na_element : 0.004"  # scripted group (container) (typed FeaturePython)
  n = 0.002
FEATURE [App::DocumentObjectGroupPython] P_element004  label="P_element : 0.004"  # scripted group (container) (typed FeaturePython)
  n = 0.004
FEATURE [App::DocumentObjectGroupPython] S_element006  label="S_element : 0.005"  # scripted group (container) (typed FeaturePython)
  n = 0.002
FEATURE [App::DocumentObjectGroupPython] Cl_element003  label="Cl_element : 0.004"  # scripted group (container) (typed FeaturePython)
  n = 0.003
FEATURE [App::DocumentObjectGroupPython] K_element002  label="K_element : 0.003"  # scripted group (container) (typed FeaturePython)
  n = 0.003
FEATURE [App::DocumentObjectGroupPython] G4_BRAIN_ICRP  # scripted group (container) (typed FeaturePython)
  Dunit = g/cm3
  Dvalue = 1.04
  Group = -> [H_element017,C_element018,N_element012,O_element017,Na_element004,P_element004,S_element006,Cl_element003,K_element002]
  conduct = 2
  density = 1
  expand = 3
  formula = G4_BRAIN_ICRP
  name = G4_BRAIN_ICRP
  specific = 4
FEATURE [App::DocumentObjectGroupPython] C_element019  label="C_element : 4"  # scripted group (container) (typed FeaturePython)
  n = 4
  ref = C_element
FEATURE [App::DocumentObjectGroupPython] H_element018  label="H_element : 010"  # scripted group (container) (typed FeaturePython)
  n = 10
  ref = H_element
FEATURE [App::DocumentObjectGroupPython] G4_BUTANE  # scripted group (container) (typed FeaturePython)
  Dunit = g/cm3
  Dvalue = 0.00249343
  Group = -> [C_element019,H_element018]
  conduct = 2
  density = 1
  expand = 3
  formula = G4_BUTANE
  name = G4_BUTANE
  specific = 4
FEATURE [App::DocumentObjectGroupPython] C_element020  label="C_element : 008"  # scripted group (container) (typed FeaturePython)
  n = 4
  ref = C_element
FEATURE [App::DocumentObjectGroupPython] H_element019  label="H_element : 011"  # scripted group (container) (typed FeaturePython)
  n = 10
  ref = H_element
FEATURE [App::DocumentObjectGroupPython] O_element018  label="O_element : 007"  # scripted group (container) (typed FeaturePython)
  n = 1
  ref = O_element
FEATURE [App::DocumentObjectGroupPython] G4_N_BUTYL_ALCOHOL  label="G4_N-BUTYL_ALCOHOL"  # scripted group (container) (typed FeaturePython)
  Dunit = g/cm3
  Dvalue = 0.8098
  Group = -> [C_element020,H_element019,O_element018]
  conduct = 2
  density = 1
  expand = 3
  formula = G4_N-BUTYL_ALCOHOL
  name = G4_N-BUTYL_ALCOHOL
  specific = 4
FEATURE [App::DocumentObjectGroupPython] H_element020  label="H_element : 0.025"  # scripted group (container) (typed FeaturePython)
  n = 0.02468
FEATURE [App::DocumentObjectGroupPython] C_element021  label="C_element : 0.502"  # scripted group (container) (typed FeaturePython)
  n = 0.501611
FEATURE [App::DocumentObjectGroupPython] O_element019  label="O_element : 0.005"  # scripted group (container) (typed FeaturePython)
  n = 0.004527
FEATURE [App::DocumentObjectGroupPython] F_element004  label="F_element : 0.465"  # scripted group (container) (typed FeaturePython)
  n = 0.465209
FEATURE [App::DocumentObjectGroupPython] Si_element001  label="Si_element : 0.004"  # scripted group (container) (typed FeaturePython)
  n = 0.003973
FEATURE [App::DocumentObjectGroupPython] G4_C_552  label="G4_C-552"  # scripted group (container) (typed FeaturePython)
  Dunit = g/cm3
  Dvalue = 1.76
  Group = -> [H_element020,C_element021,O_element019,F_element004,Si_element001]
  conduct = 2
  density = 1
  expand = 3
  formula = G4_C-552
  name = G4_C-552
  specific = 4
FEATURE [App::DocumentObjectGroupPython] Cd_element001  label="Cd_element : 1"  # scripted group (container) (typed FeaturePython)
  n = 1
  ref = Cd_element
FEATURE [App::DocumentObjectGroupPython] Te_element001  label="Te_element : 1"  # scripted group (container) (typed FeaturePython)
  n = 1
  ref = Te_element
FEATURE [App::DocumentObjectGroupPython] G4_CADMIUM_TELLURIDE  # scripted group (container) (typed FeaturePython)
  Dunit = g/cm3
  Dvalue = 6.2
  Group = -> [Cd_element001,Te_element001]
  conduct = 2
  density = 1
  expand = 3
  formula = G4_CADMIUM_TELLURIDE
  name = G4_CADMIUM_TELLURIDE
  specific = 4
FEATURE [App::DocumentObjectGroupPython] Cd_element002  label="Cd_element : 002"  # scripted group (container) (typed FeaturePython)
  n = 1
  ref = Cd_element
FEATURE [App::DocumentObjectGroupPython] W_element001  label="W_element : 1"  # scripted group (container) (typed FeaturePython)
  n = 1
  ref = W_element
FEATURE [App::DocumentObjectGroupPython] O_element020  label="O_element : 008"  # scripted group (container) (typed FeaturePython)
  n = 4
  ref = O_element
FEATURE [App::DocumentObjectGroupPython] G4_CADMIUM_TUNGSTATE  # scripted group (container) (typed FeaturePython)
  Dunit = g/cm3
  Dvalue = 7.9
  Group = -> [Cd_element002,W_element001,O_element020]
  conduct = 2
  density = 1
  expand = 3
  formula = G4_CADMIUM_TUNGSTATE
  name = G4_CADMIUM_TUNGSTATE
  specific = 4
FEATURE [App::DocumentObjectGroupPython] Ca_element005  label="Ca_element : 1"  # scripted group (container) (typed FeaturePython)
  n = 1
  ref = Ca_element
FEATURE [App::DocumentObjectGroupPython] C_element022  label="C_element : 009"  # scripted group (container) (typed FeaturePython)
  n = 1
  ref = C_element
FEATURE [App::DocumentObjectGroupPython] O_element021  label="O_element : 009"  # scripted group (container) (typed FeaturePython)
  n = 3
  ref = O_element
FEATURE [App::DocumentObjectGroupPython] G4_CALCIUM_CARBONATE  # scripted group (container) (typed FeaturePython)
  Dunit = g/cm3
  Dvalue = 2.8
  Group = -> [Ca_element005,C_element022,O_element021]
  conduct = 2
  density = 1
  expand = 3
  formula = G4_CALCIUM_CARBONATE
  name = G4_CALCIUM_CARBONATE
  specific = 4
FEATURE [App::DocumentObjectGroupPython] Ca_element006  label="Ca_element : 002"  # scripted group (container) (typed FeaturePython)
  n = 1
  ref = Ca_element
FEATURE [App::DocumentObjectGroupPython] F_element005  label="F_element : 003"  # scripted group (container) (typed FeaturePython)
  n = 2
  ref = F_element
FEATURE [App::DocumentObjectGroupPython] G4_CALCIUM_FLUORIDE  # scripted group (container) (typed FeaturePython)
  Dunit = g/cm3
  Dvalue = 3.18
  Group = -> [Ca_element006,F_element005]
  conduct = 2
  density = 1
  expand = 3
  formula = G4_CALCIUM_FLUORIDE
  name = G4_CALCIUM_FLUORIDE
  specific = 4
FEATURE [App::DocumentObjectGroupPython] Ca_element007  label="Ca_element : 003"  # scripted group (container) (typed FeaturePython)
  n = 1
  ref = Ca_element
FEATURE [App::DocumentObjectGroupPython] O_element022  label="O_element : 010"  # scripted group (container) (typed FeaturePython)
  n = 1
  ref = O_element
FEATURE [App::DocumentObjectGroupPython] G4_CALCIUM_OXIDE  # scripted group (container) (typed FeaturePython)
  Dunit = g/cm3
  Dvalue = 3.3
  Group = -> [Ca_element007,O_element022]
  conduct = 2
  density = 1
  expand = 3
  formula = G4_CALCIUM_OXIDE
  name = G4_CALCIUM_OXIDE
  specific = 4
FEATURE [App::DocumentObjectGroupPython] Ca_element008  label="Ca_element : 004"  # scripted group (container) (typed FeaturePython)
  n = 1
  ref = Ca_element
FEATURE [App::DocumentObjectGroupPython] S_element007  label="S_element : 002"  # scripted group (container) (typed FeaturePython)
  n = 1
  ref = S_element
FEATURE [App::DocumentObjectGroupPython] O_element023  label="O_element : 011"  # scripted group (container) (typed FeaturePython)
  n = 4
  ref = O_element
FEATURE [App::DocumentObjectGroupPython] G4_CALCIUM_SULFATE  # scripted group (container) (typed FeaturePython)
  Dunit = g/cm3
  Dvalue = 2.96
  Group = -> [Ca_element008,S_element007,O_element023]
  conduct = 2
  density = 1
  expand = 3
  formula = G4_CALCIUM_SULFATE
  name = G4_CALCIUM_SULFATE
  specific = 4
FEATURE [App::DocumentObjectGroupPython] Ca_element009  label="Ca_element : 005"  # scripted group (container) (typed FeaturePython)
  n = 1
  ref = Ca_element
FEATURE [App::DocumentObjectGroupPython] W_element002  label="W_element : 002"  # scripted group (container) (typed FeaturePython)
  n = 1
  ref = W_element
FEATURE [App::DocumentObjectGroupPython] O_element024  label="O_element : 012"  # scripted group (container) (typed FeaturePython)
  n = 4
  ref = O_element
FEATURE [App::DocumentObjectGroupPython] G4_CALCIUM_TUNGSTATE  # scripted group (container) (typed FeaturePython)
  Dunit = g/cm3
  Dvalue = 6.062
  Group = -> [Ca_element009,W_element002,O_element024]
  conduct = 2
  density = 1
  expand = 3
  formula = G4_CALCIUM_TUNGSTATE
  name = G4_CALCIUM_TUNGSTATE
  specific = 4
FEATURE [App::DocumentObjectGroupPython] C_element023  label="C_element : 010"  # scripted group (container) (typed FeaturePython)
  n = 1
  ref = C_element
FEATURE [App::DocumentObjectGroupPython] O_element025  label="O_element : 013"  # scripted group (container) (typed FeaturePython)
  n = 2
  ref = O_element
FEATURE [App::DocumentObjectGroupPython] G4_CARBON_DIOXIDE  # scripted group (container) (typed FeaturePython)
  Dunit = g/cm3
  Dvalue = 0.00184212
  Group = -> [C_element023,O_element025]
  conduct = 2
  density = 1
  expand = 3
  formula = G4_CARBON_DIOXIDE
  name = G4_CARBON_DIOXIDE
  specific = 4
FEATURE [App::DocumentObjectGroupPython] C_element024  label="C_element : 011"  # scripted group (container) (typed FeaturePython)
  n = 1
  ref = C_element
FEATURE [App::DocumentObjectGroupPython] Cl_element004  label="Cl_element : 4"  # scripted group (container) (typed FeaturePython)
  n = 4
  ref = Cl_element
FEATURE [App::DocumentObjectGroupPython] G4_CARBON_TETRACHLORIDE  # scripted group (container) (typed FeaturePython)
  Dunit = g/cm3
  Dvalue = 1.594
  Group = -> [C_element024,Cl_element004]
  conduct = 2
  density = 1
  expand = 3
  formula = G4_CARBON_TETRACHLORIDE
  name = G4_CARBON_TETRACHLORIDE
  specific = 4
FEATURE [App::DocumentObjectGroupPython] C_element025  label="C_element : 012"  # scripted group (container) (typed FeaturePython)
  n = 6
  ref = C_element
FEATURE [App::DocumentObjectGroupPython] H_element021  label="H_element : 012"  # scripted group (container) (typed FeaturePython)
  n = 10
  ref = H_element
FEATURE [App::DocumentObjectGroupPython] O_element026  label="O_element : 5"  # scripted group (container) (typed FeaturePython)
  n = 5
  ref = O_element
FEATURE [App::DocumentObjectGroupPython] G4_CELLULOSE_CELLOPHANE  # scripted group (container) (typed FeaturePython)
  Dunit = g/cm3
  Dvalue = 1.42
  Group = -> [C_element025,H_element021,O_element026]
  conduct = 2
  density = 1
  expand = 3
  formula = G4_CELLULOSE_CELLOPHANE
  name = G4_CELLULOSE_CELLOPHANE
  specific = 4
FEATURE [App::DocumentObjectGroupPython] H_element022  label="H_element : 0.067"  # scripted group (container) (typed FeaturePython)
  n = 0.067125
FEATURE [App::DocumentObjectGroupPython] C_element026  label="C_element : 0.545"  # scripted group (container) (typed FeaturePython)
  n = 0.545403
FEATURE [App::DocumentObjectGroupPython] O_element027  label="O_element : 0.387"  # scripted group (container) (typed FeaturePython)
  n = 0.387472
FEATURE [App::DocumentObjectGroupPython] G4_CELLULOSE_BUTYRATE  # scripted group (container) (typed FeaturePython)
  Dunit = g/cm3
  Dvalue = 1.2
  Group = -> [H_element022,C_element026,O_element027]
  conduct = 2
  density = 1
  expand = 3
  formula = G4_CELLULOSE_BUTYRATE
  name = G4_CELLULOSE_BUTYRATE
  specific = 4
FEATURE [App::DocumentObjectGroupPython] H_element023  label="H_element : 0.029"  # scripted group (container) (typed FeaturePython)
  n = 0.029216
FEATURE [App::DocumentObjectGroupPython] C_element027  label="C_element : 0.271"  # scripted group (container) (typed FeaturePython)
  n = 0.271296
FEATURE [App::DocumentObjectGroupPython] N_element013  label="N_element : 0.121"  # scripted group (container) (typed FeaturePython)
  n = 0.121276
FEATURE [App::DocumentObjectGroupPython] O_element028  label="O_element : 0.578"  # scripted group (container) (typed FeaturePython)
  n = 0.578212
FEATURE [App::DocumentObjectGroupPython] G4_CELLULOSE_NITRATE  # scripted group (container) (typed FeaturePython)
  Dunit = g/cm3
  Dvalue = 1.49
  Group = -> [H_element023,C_element027,N_element013,O_element028]
  conduct = 2
  density = 1
  expand = 3
  formula = G4_CELLULOSE_NITRATE
  name = G4_CELLULOSE_NITRATE
  specific = 4
FEATURE [App::DocumentObjectGroupPython] H_element024  label="H_element : 0.108"  # scripted group (container) (typed FeaturePython)
  n = 0.107596
FEATURE [App::DocumentObjectGroupPython] N_element014  label="N_element : 0.001"  # scripted group (container) (typed FeaturePython)
  n = 0.0008
FEATURE [App::DocumentObjectGroupPython] O_element029  label="O_element : 0.875"  # scripted group (container) (typed FeaturePython)
  n = 0.874976
FEATURE [App::DocumentObjectGroupPython] S_element008  label="S_element : 0.015"  # scripted group (container) (typed FeaturePython)
  n = 0.014627
FEATURE [App::DocumentObjectGroupPython] Ce_element001  label="Ce_element : 0.002"  # scripted group (container) (typed FeaturePython)
  n = 0.002001
FEATURE [App::DocumentObjectGroupPython] G4_CERIC_SULFATE  # scripted group (container) (typed FeaturePython)
  Dunit = g/cm3
  Dvalue = 1.03
  Group = -> [H_element024,N_element014,O_element029,S_element008,Ce_element001]
  conduct = 2
  density = 1
  expand = 3
  formula = G4_CERIC_SULFATE
  name = G4_CERIC_SULFATE
  specific = 4
FEATURE [App::DocumentObjectGroupPython] Cs_element001  label="Cs_element : 1"  # scripted group (container) (typed FeaturePython)
  n = 1
  ref = Cs_element
FEATURE [App::DocumentObjectGroupPython] F_element006  label="F_element : 1"  # scripted group (container) (typed FeaturePython)
  n = 1
  ref = F_element
FEATURE [App::DocumentObjectGroupPython] G4_CESIUM_FLUORIDE  # scripted group (container) (typed FeaturePython)
  Dunit = g/cm3
  Dvalue = 4.115
  Group = -> [Cs_element001,F_element006]
  conduct = 2
  density = 1
  expand = 3
  formula = G4_CESIUM_FLUORIDE
  name = G4_CESIUM_FLUORIDE
  specific = 4
FEATURE [App::DocumentObjectGroupPython] Cs_element002  label="Cs_element : 002"  # scripted group (container) (typed FeaturePython)
  n = 1
  ref = Cs_element
FEATURE [App::DocumentObjectGroupPython] I_element001  label="I_element : 1"  # scripted group (container) (typed FeaturePython)
  n = 1
  ref = I_element
FEATURE [App::DocumentObjectGroupPython] G4_CESIUM_IODIDE  # scripted group (container) (typed FeaturePython)
  Dunit = g/cm3
  Dvalue = 4.51
  Group = -> [Cs_element002,I_element001]
  conduct = 2
  density = 1
  expand = 3
  formula = G4_CESIUM_IODIDE
  name = G4_CESIUM_IODIDE
  specific = 4
FEATURE [App::DocumentObjectGroupPython] C_element028  label="C_element : 013"  # scripted group (container) (typed FeaturePython)
  n = 6
  ref = C_element
FEATURE [App::DocumentObjectGroupPython] H_element025  label="H_element : 013"  # scripted group (container) (typed FeaturePython)
  n = 5
  ref = H_element
FEATURE [App::DocumentObjectGroupPython] Cl_element005  label="Cl_element : 1"  # scripted group (container) (typed FeaturePython)
  n = 1
  ref = Cl_element
FEATURE [App::DocumentObjectGroupPython] G4_CHLOROBENZENE  # scripted group (container) (typed FeaturePython)
  Dunit = g/cm3
  Dvalue = 1.1058
  Group = -> [C_element028,H_element025,Cl_element005]
  conduct = 2
  density = 1
  expand = 3
  formula = G4_CHLOROBENZENE
  name = G4_CHLOROBENZENE
  specific = 4
FEATURE [App::DocumentObjectGroupPython] C_element029  label="C_element : 014"  # scripted group (container) (typed FeaturePython)
  n = 1
  ref = C_element
FEATURE [App::DocumentObjectGroupPython] H_element026  label="H_element : 1"  # scripted group (container) (typed FeaturePython)
  n = 1
  ref = H_element
FEATURE [App::DocumentObjectGroupPython] Cl_element006  label="Cl_element : 3"  # scripted group (container) (typed FeaturePython)
  n = 3
  ref = Cl_element
FEATURE [App::DocumentObjectGroupPython] G4_CHLOROFORM  # scripted group (container) (typed FeaturePython)
  Dunit = g/cm3
  Dvalue = 1.4832
  Group = -> [C_element029,H_element026,Cl_element006]
  conduct = 2
  density = 1
  expand = 3
  formula = G4_CHLOROFORM
  name = G4_CHLOROFORM
  specific = 4
FEATURE [App::DocumentObjectGroupPython] H_element027  label="H_element : 0.010"  # scripted group (container) (typed FeaturePython)
  n = 0.01
FEATURE [App::DocumentObjectGroupPython] C_element030  label="C_element : 0.001"  # scripted group (container) (typed FeaturePython)
  n = 0.001
FEATURE [App::DocumentObjectGroupPython] O_element030  label="O_element : 0.529"  # scripted group (container) (typed FeaturePython)
  n = 0.529107
FEATURE [App::DocumentObjectGroupPython] Na_element005  label="Na_element : 0.016"  # scripted group (container) (typed FeaturePython)
  n = 0.016
FEATURE [App::DocumentObjectGroupPython] Mg_element003  label="Mg_element : 0.004"  # scripted group (container) (typed FeaturePython)
  n = 0.002
FEATURE [App::DocumentObjectGroupPython] Al_element002  label="Al_element : 0.034"  # scripted group (container) (typed FeaturePython)
  n = 0.033872
FEATURE [App::DocumentObjectGroupPython] Si_element002  label="Si_element : 0.337"  # scripted group (container) (typed FeaturePython)
  n = 0.337021
FEATURE [App::DocumentObjectGroupPython] K_element003  label="K_element : 0.013"  # scripted group (container) (typed FeaturePython)
  n = 0.013
FEATURE [App::DocumentObjectGroupPython] Ca_element010  label="Ca_element : 0.044"  # scripted group (container) (typed FeaturePython)
  n = 0.044
FEATURE [App::DocumentObjectGroupPython] Fe_element002  label="Fe_element : 0.014"  # scripted group (container) (typed FeaturePython)
  n = 0.014
FEATURE [App::DocumentObjectGroupPython] G4_CONCRETE  # scripted group (container) (typed FeaturePython)
  Dunit = g/cm3
  Dvalue = 2.3
  Group = -> [H_element027,C_element030,O_element030,Na_element005,Mg_element003,Al_element002,Si_element002,K_element003,Ca_element010,Fe_element002]
  conduct = 2
  density = 1
  expand = 3
  formula = G4_CONCRETE
  name = G4_CONCRETE
  specific = 4
FEATURE [App::DocumentObjectGroupPython] C_element031  label="C_element : 015"  # scripted group (container) (typed FeaturePython)
  n = 6
  ref = C_element
FEATURE [App::DocumentObjectGroupPython] H_element028  label="H_element : 12"  # scripted group (container) (typed FeaturePython)
  n = 12
  ref = H_element
FEATURE [App::DocumentObjectGroupPython] G4_CYCLOHEXANE  # scripted group (container) (typed FeaturePython)
  Dunit = g/cm3
  Dvalue = 0.779
  Group = -> [C_element031,H_element028]
  conduct = 2
  density = 1
  expand = 3
  formula = G4_CYCLOHEXANE
  name = G4_CYCLOHEXANE
  specific = 4
FEATURE [App::DocumentObjectGroupPython] C_element032  label="C_element : 016"  # scripted group (container) (typed FeaturePython)
  n = 6
  ref = C_element
FEATURE [App::DocumentObjectGroupPython] H_element029  label="H_element : 4"  # scripted group (container) (typed FeaturePython)
  n = 4
  ref = H_element
FEATURE [App::DocumentObjectGroupPython] Cl_element007  label="Cl_element : 2"  # scripted group (container) (typed FeaturePython)
  n = 2
  ref = Cl_element
FEATURE [App::DocumentObjectGroupPython] G4_1_2_DICHLOROBENZENE  label="G4_1.2-DICHLOROBENZENE"  # scripted group (container) (typed FeaturePython)
  Dunit = g/cm3
  Dvalue = 1.3048
  Group = -> [C_element032,H_element029,Cl_element007]
  conduct = 2
  density = 1
  expand = 3
  formula = G4_1.2-DICHLOROBENZENE
  name = G4_1.2-DICHLOROBENZENE
  specific = 4
FEATURE [App::DocumentObjectGroupPython] C_element033  label="C_element : 017"  # scripted group (container) (typed FeaturePython)
  n = 4
  ref = C_element
FEATURE [App::DocumentObjectGroupPython] H_element030  label="H_element : 8"  # scripted group (container) (typed FeaturePython)
  n = 8
  ref = H_element
FEATURE [App::DocumentObjectGroupPython] O_element031  label="O_element : 014"  # scripted group (container) (typed FeaturePython)
  n = 1
  ref = O_element
FEATURE [App::DocumentObjectGroupPython] Cl_element008  label="Cl_element : 005"  # scripted group (container) (typed FeaturePython)
  n = 2
  ref = Cl_element
FEATURE [App::DocumentObjectGroupPython] G4_DICHLORODIETHYL_ETHER  # scripted group (container) (typed FeaturePython)
  Dunit = g/cm3
  Dvalue = 1.2199
  Group = -> [C_element033,H_element030,O_element031,Cl_element008]
  conduct = 2
  density = 1
  expand = 3
  formula = G4_DICHLORODIETHYL_ETHER
  name = G4_DICHLORODIETHYL_ETHER
  specific = 4
FEATURE [App::DocumentObjectGroupPython] C_element034  label="C_element : 018"  # scripted group (container) (typed FeaturePython)
  n = 2
  ref = C_element
FEATURE [App::DocumentObjectGroupPython] H_element031  label="H_element : 014"  # scripted group (container) (typed FeaturePython)
  n = 4
  ref = H_element
FEATURE [App::DocumentObjectGroupPython] Cl_element009  label="Cl_element : 006"  # scripted group (container) (typed FeaturePython)
  n = 2
  ref = Cl_element
FEATURE [App::DocumentObjectGroupPython] G4_1_2_DICHLOROETHANE  label="G4_1.2-DICHLOROETHANE"  # scripted group (container) (typed FeaturePython)
  Dunit = g/cm3
  Dvalue = 1.2351
  Group = -> [C_element034,H_element031,Cl_element009]
  conduct = 2
  density = 1
  expand = 3
  formula = G4_1.2-DICHLOROETHANE
  name = G4_1.2-DICHLOROETHANE
  specific = 4
FEATURE [App::DocumentObjectGroupPython] C_element035  label="C_element : 019"  # scripted group (container) (typed FeaturePython)
  n = 4
  ref = C_element
FEATURE [App::DocumentObjectGroupPython] H_element032  label="H_element : 015"  # scripted group (container) (typed FeaturePython)
  n = 10
  ref = H_element
FEATURE [App::DocumentObjectGroupPython] O_element032  label="O_element : 015"  # scripted group (container) (typed FeaturePython)
  n = 1
  ref = O_element
FEATURE [App::DocumentObjectGroupPython] G4_DIETHYL_ETHER  # scripted group (container) (typed FeaturePython)
  Dunit = g/cm3
  Dvalue = 0.71378
  Group = -> [C_element035,H_element032,O_element032]
  conduct = 2
  density = 1
  expand = 3
  formula = G4_DIETHYL_ETHER
  name = G4_DIETHYL_ETHER
  specific = 4
FEATURE [App::DocumentObjectGroupPython] C_element036  label="C_element : 020"  # scripted group (container) (typed FeaturePython)
  n = 3
  ref = C_element
FEATURE [App::DocumentObjectGroupPython] H_element033  label="H_element : 016"  # scripted group (container) (typed FeaturePython)
  n = 7
  ref = H_element
FEATURE [App::DocumentObjectGroupPython] N_element015  label="N_element : 008"  # scripted group (container) (typed FeaturePython)
  n = 1
  ref = N_element
FEATURE [App::DocumentObjectGroupPython] O_element033  label="O_element : 016"  # scripted group (container) (typed FeaturePython)
  n = 1
  ref = O_element
FEATURE [App::DocumentObjectGroupPython] G4_N_N_DIMETHYL_FORMAMIDE  label="G4_N.N-DIMETHYL_FORMAMIDE"  # scripted group (container) (typed FeaturePython)
  Dunit = g/cm3
  Dvalue = 0.9487
  Group = -> [C_element036,H_element033,N_element015,O_element033]
  conduct = 2
  density = 1
  expand = 3
  formula = G4_N.N-DIMETHYL_FORMAMIDE
  name = G4_N.N-DIMETHYL_FORMAMIDE
  specific = 4
FEATURE [App::DocumentObjectGroupPython] C_element037  label="C_element : 021"  # scripted group (container) (typed FeaturePython)
  n = 2
  ref = C_element
FEATURE [App::DocumentObjectGroupPython] H_element034  label="H_element : 017"  # scripted group (container) (typed FeaturePython)
  n = 6
  ref = H_element
FEATURE [App::DocumentObjectGroupPython] O_element034  label="O_element : 017"  # scripted group (container) (typed FeaturePython)
  n = 1
  ref = O_element
FEATURE [App::DocumentObjectGroupPython] S_element009  label="S_element : 003"  # scripted group (container) (typed FeaturePython)
  n = 1
  ref = S_element
FEATURE [App::DocumentObjectGroupPython] G4_DIMETHYL_SULFOXIDE  # scripted group (container) (typed FeaturePython)
  Dunit = g/cm3
  Dvalue = 1.1014
  Group = -> [C_element037,H_element034,O_element034,S_element009]
  conduct = 2
  density = 1
  expand = 3
  formula = G4_DIMETHYL_SULFOXIDE
  name = G4_DIMETHYL_SULFOXIDE
  specific = 4
FEATURE [App::DocumentObjectGroupPython] C_element038  label="C_element : 022"  # scripted group (container) (typed FeaturePython)
  n = 2
  ref = C_element
FEATURE [App::DocumentObjectGroupPython] H_element035  label="H_element : 018"  # scripted group (container) (typed FeaturePython)
  n = 6
  ref = H_element
FEATURE [App::DocumentObjectGroupPython] G4_ETHANE  # scripted group (container) (typed FeaturePython)
  Dunit = g/cm3
  Dvalue = 0.00125324
  Group = -> [C_element038,H_element035]
  conduct = 2
  density = 1
  expand = 3
  formula = G4_ETHANE
  name = G4_ETHANE
  specific = 4
FEATURE [App::DocumentObjectGroupPython] C_element039  label="C_element : 023"  # scripted group (container) (typed FeaturePython)
  n = 2
  ref = C_element
FEATURE [App::DocumentObjectGroupPython] H_element036  label="H_element : 019"  # scripted group (container) (typed FeaturePython)
  n = 6
  ref = H_element
FEATURE [App::DocumentObjectGroupPython] O_element035  label="O_element : 018"  # scripted group (container) (typed FeaturePython)
  n = 1
  ref = O_element
FEATURE [App::DocumentObjectGroupPython] G4_ETHYL_ALCOHOL  # scripted group (container) (typed FeaturePython)
  Dunit = g/cm3
  Dvalue = 0.7893
  Group = -> [C_element039,H_element036,O_element035]
  conduct = 2
  density = 1
  expand = 3
  formula = G4_ETHYL_ALCOHOL
  name = G4_ETHYL_ALCOHOL
  specific = 4
FEATURE [App::DocumentObjectGroupPython] H_element037  label="H_element : 0.090"  # scripted group (container) (typed FeaturePython)
  n = 0.090027
FEATURE [App::DocumentObjectGroupPython] C_element040  label="C_element : 0.585"  # scripted group (container) (typed FeaturePython)
  n = 0.585182
FEATURE [App::DocumentObjectGroupPython] O_element036  label="O_element : 0.325"  # scripted group (container) (typed FeaturePython)
  n = 0.324791
FEATURE [App::DocumentObjectGroupPython] G4_ETHYL_CELLULOSE  # scripted group (container) (typed FeaturePython)
  Dunit = g/cm3
  Dvalue = 1.13
  Group = -> [H_element037,C_element040,O_element036]
  conduct = 2
  density = 1
  expand = 3
  formula = G4_ETHYL_CELLULOSE
  name = G4_ETHYL_CELLULOSE
  specific = 4
FEATURE [App::DocumentObjectGroupPython] C_element041  label="C_element : 024"  # scripted group (container) (typed FeaturePython)
  n = 2
  ref = C_element
FEATURE [App::DocumentObjectGroupPython] H_element038  label="H_element : 020"  # scripted group (container) (typed FeaturePython)
  n = 4
  ref = H_element
FEATURE [App::DocumentObjectGroupPython] G4_ETHYLENE  # scripted group (container) (typed FeaturePython)
  Dunit = g/cm3
  Dvalue = 0.00117497
  Group = -> [C_element041,H_element038]
  conduct = 2
  density = 1
  expand = 3
  formula = G4_ETHYLENE
  name = G4_ETHYLENE
  specific = 4
FEATURE [App::DocumentObjectGroupPython] H_element039  label="H_element : 0.096"  # scripted group (container) (typed FeaturePython)
  n = 0.096
FEATURE [App::DocumentObjectGroupPython] C_element042  label="C_element : 0.195"  # scripted group (container) (typed FeaturePython)
  n = 0.195
FEATURE [App::DocumentObjectGroupPython] N_element016  label="N_element : 0.057"  # scripted group (container) (typed FeaturePython)
  n = 0.057
FEATURE [App::DocumentObjectGroupPython] O_element037  label="O_element : 0.646"  # scripted group (container) (typed FeaturePython)
  n = 0.646
FEATURE [App::DocumentObjectGroupPython] Na_element006  label="Na_element : 0.017"  # scripted group (container) (typed FeaturePython)
  n = 0.001
FEATURE [App::DocumentObjectGroupPython] P_element005  label="P_element : 0.104"  # scripted group (container) (typed FeaturePython)
  n = 0.001
FEATURE [App::DocumentObjectGroupPython] S_element010  label="S_element : 0.016"  # scripted group (container) (typed FeaturePython)
  n = 0.003
FEATURE [App::DocumentObjectGroupPython] Cl_element010  label="Cl_element : 0.005"  # scripted group (container) (typed FeaturePython)
  n = 0.001
FEATURE [App::DocumentObjectGroupPython] G4_EYE_LENS_ICRP  # scripted group (container) (typed FeaturePython)
  Dunit = g/cm3
  Dvalue = 1.07
  Group = -> [H_element039,C_element042,N_element016,O_element037,Na_element006,P_element005,S_element010,Cl_element010]
  conduct = 2
  density = 1
  expand = 3
  formula = G4_EYE_LENS_ICRP
  name = G4_EYE_LENS_ICRP
  specific = 4
FEATURE [App::DocumentObjectGroupPython] Fe_element003  label="Fe_element : 2"  # scripted group (container) (typed FeaturePython)
  n = 2
  ref = Fe_element
FEATURE [App::DocumentObjectGroupPython] O_element038  label="O_element : 019"  # scripted group (container) (typed FeaturePython)
  n = 3
  ref = O_element
FEATURE [App::DocumentObjectGroupPython] G4_FERRIC_OXIDE  # scripted group (container) (typed FeaturePython)
  Dunit = g/cm3
  Dvalue = 5.2
  Group = -> [Fe_element003,O_element038]
  conduct = 2
  density = 1
  expand = 3
  formula = G4_FERRIC_OXIDE
  name = G4_FERRIC_OXIDE
  specific = 4
FEATURE [App::DocumentObjectGroupPython] Fe_element004  label="Fe_element : 1"  # scripted group (container) (typed FeaturePython)
  n = 1
  ref = Fe_element
FEATURE [App::DocumentObjectGroupPython] B_element003  label="B_element : 1"  # scripted group (container) (typed FeaturePython)
  n = 1
  ref = B_element
FEATURE [App::DocumentObjectGroupPython] G4_FERROBORIDE  # scripted group (container) (typed FeaturePython)
  Dunit = g/cm3
  Dvalue = 7.15
  Group = -> [Fe_element004,B_element003]
  conduct = 2
  density = 1
  expand = 3
  formula = G4_FERROBORIDE
  name = G4_FERROBORIDE
  specific = 4
FEATURE [App::DocumentObjectGroupPython] Fe_element005  label="Fe_element : 003"  # scripted group (container) (typed FeaturePython)
  n = 1
  ref = Fe_element
FEATURE [App::DocumentObjectGroupPython] O_element039  label="O_element : 020"  # scripted group (container) (typed FeaturePython)
  n = 1
  ref = O_element
FEATURE [App::DocumentObjectGroupPython] G4_FERROUS_OXIDE  # scripted group (container) (typed FeaturePython)
  Dunit = g/cm3
  Dvalue = 5.7
  Group = -> [Fe_element005,O_element039]
  conduct = 2
  density = 1
  expand = 3
  formula = G4_FERROUS_OXIDE
  name = G4_FERROUS_OXIDE
  specific = 4
FEATURE [App::DocumentObjectGroupPython] H_element040  label="H_element : 0.115"  # scripted group (container) (typed FeaturePython)
  n = 0.108259
FEATURE [App::DocumentObjectGroupPython] N_element017  label="N_element : 0.000"  # scripted group (container) (typed FeaturePython)
  n = 2.7e-05
FEATURE [App::DocumentObjectGroupPython] O_element040  label="O_element : 0.879"  # scripted group (container) (typed FeaturePython)
  n = 0.878636
FEATURE [App::DocumentObjectGroupPython] Na_element007  label="Na_element : 0.000"  # scripted group (container) (typed FeaturePython)
  n = 2.2e-05
FEATURE [App::DocumentObjectGroupPython] S_element011  label="S_element : 0.013"  # scripted group (container) (typed FeaturePython)
  n = 0.012968
FEATURE [App::DocumentObjectGroupPython] Cl_element011  label="Cl_element : 0.000"  # scripted group (container) (typed FeaturePython)
  n = 3.4e-05
FEATURE [App::DocumentObjectGroupPython] Fe_element006  label="Fe_element : 0.000"  # scripted group (container) (typed FeaturePython)
  n = 5.4e-05
FEATURE [App::DocumentObjectGroupPython] G4_FERROUS_SULFATE  # scripted group (container) (typed FeaturePython)
  Dunit = g/cm3
  Dvalue = 1.024
  Group = -> [H_element040,N_element017,O_element040,Na_element007,S_element011,Cl_element011,Fe_element006]
  conduct = 2
  density = 1
  expand = 3
  formula = G4_FERROUS_SULFATE
  name = G4_FERROUS_SULFATE
  specific = 4
FEATURE [App::DocumentObjectGroupPython] C_element043  label="C_element : 0.099"  # scripted group (container) (typed FeaturePython)
  n = 0.099335
FEATURE [App::DocumentObjectGroupPython] F_element007  label="F_element : 0.314"  # scripted group (container) (typed FeaturePython)
  n = 0.314247
FEATURE [App::DocumentObjectGroupPython] Cl_element012  label="Cl_element : 0.586"  # scripted group (container) (typed FeaturePython)
  n = 0.586418
FEATURE [App::DocumentObjectGroupPython] G4_FREON_12  label="G4_FREON-12"  # scripted group (container) (typed FeaturePython)
  Dunit = g/cm3
  Dvalue = 1.12
  Group = -> [C_element043,F_element007,Cl_element012]
  conduct = 2
  density = 1
  expand = 3
  formula = G4_FREON-12
  name = G4_FREON-12
  specific = 4
FEATURE [App::DocumentObjectGroupPython] C_element044  label="C_element : 0.057"  # scripted group (container) (typed FeaturePython)
  n = 0.057245
FEATURE [App::DocumentObjectGroupPython] F_element008  label="F_element : 0.181"  # scripted group (container) (typed FeaturePython)
  n = 0.181096
FEATURE [App::DocumentObjectGroupPython] Br_element001  label="Br_element : 0.762"  # scripted group (container) (typed FeaturePython)
  n = 0.761659
FEATURE [App::DocumentObjectGroupPython] G4_FREON_12B2  label="G4_FREON-12B2"  # scripted group (container) (typed FeaturePython)
  Dunit = g/cm3
  Dvalue = 1.8
  Group = -> [C_element044,F_element008,Br_element001]
  conduct = 2
  density = 1
  expand = 3
  formula = G4_FREON-12B2
  name = G4_FREON-12B2
  specific = 4
FEATURE [App::DocumentObjectGroupPython] C_element045  label="C_element : 0.115"  # scripted group (container) (typed FeaturePython)
  n = 0.114983
FEATURE [App::DocumentObjectGroupPython] F_element009  label="F_element : 0.546"  # scripted group (container) (typed FeaturePython)
  n = 0.545621
FEATURE [App::DocumentObjectGroupPython] Cl_element013  label="Cl_element : 0.339"  # scripted group (container) (typed FeaturePython)
  n = 0.339396
FEATURE [App::DocumentObjectGroupPython] G4_FREON_13  label="G4_FREON-13"  # scripted group (container) (typed FeaturePython)
  Dunit = g/cm3
  Dvalue = 0.95
  Group = -> [C_element045,F_element009,Cl_element013]
  conduct = 2
  density = 1
  expand = 3
  formula = G4_FREON-13
  name = G4_FREON-13
  specific = 4
FEATURE [App::DocumentObjectGroupPython] C_element046  label="C_element : 025"  # scripted group (container) (typed FeaturePython)
  n = 1
  ref = C_element
FEATURE [App::DocumentObjectGroupPython] F_element010  label="F_element : 3"  # scripted group (container) (typed FeaturePython)
  n = 3
  ref = F_element
FEATURE [App::DocumentObjectGroupPython] Br_element002  label="Br_element : 1"  # scripted group (container) (typed FeaturePython)
  n = 1
  ref = Br_element
FEATURE [App::DocumentObjectGroupPython] G4_FREON_13B1  label="G4_FREON-13B1"  # scripted group (container) (typed FeaturePython)
  Dunit = g/cm3
  Dvalue = 1.5
  Group = -> [C_element046,F_element010,Br_element002]
  conduct = 2
  density = 1
  expand = 3
  formula = G4_FREON-13B1
  name = G4_FREON-13B1
  specific = 4
FEATURE [App::DocumentObjectGroupPython] C_element047  label="C_element : 0.061"  # scripted group (container) (typed FeaturePython)
  n = 0.061309
FEATURE [App::DocumentObjectGroupPython] F_element011  label="F_element : 0.291"  # scripted group (container) (typed FeaturePython)
  n = 0.290924
FEATURE [App::DocumentObjectGroupPython] I_element002  label="I_element : 0.648"  # scripted group (container) (typed FeaturePython)
  n = 0.647767
FEATURE [App::DocumentObjectGroupPython] G4_FREON_13I1  label="G4_FREON-13I1"  # scripted group (container) (typed FeaturePython)
  Dunit = g/cm3
  Dvalue = 1.8
  Group = -> [C_element047,F_element011,I_element002]
  conduct = 2
  density = 1
  expand = 3
  formula = G4_FREON-13I1
  name = G4_FREON-13I1
  specific = 4
FEATURE [App::DocumentObjectGroupPython] Gd_element001  label="Gd_element : 2"  # scripted group (container) (typed FeaturePython)
  n = 2
  ref = Gd_element
FEATURE [App::DocumentObjectGroupPython] O_element041  label="O_element : 021"  # scripted group (container) (typed FeaturePython)
  n = 2
  ref = O_element
FEATURE [App::DocumentObjectGroupPython] S_element012  label="S_element : 004"  # scripted group (container) (typed FeaturePython)
  n = 1
  ref = S_element
FEATURE [App::DocumentObjectGroupPython] G4_GADOLINIUM_OXYSULFIDE  # scripted group (container) (typed FeaturePython)
  Dunit = g/cm3
  Dvalue = 7.44
  Group = -> [Gd_element001,O_element041,S_element012]
  conduct = 2
  density = 1
  expand = 3
  formula = G4_GADOLINIUM_OXYSULFIDE
  name = G4_GADOLINIUM_OXYSULFIDE
  specific = 4
FEATURE [App::DocumentObjectGroupPython] Ga_element001  label="Ga_element : 1"  # scripted group (container) (typed FeaturePython)
  n = 1
  ref = Ga_element
FEATURE [App::DocumentObjectGroupPython] As_element001  label="As_element : 1"  # scripted group (container) (typed FeaturePython)
  n = 1
  ref = As_element
FEATURE [App::DocumentObjectGroupPython] G4_GALLIUM_ARSENIDE  # scripted group (container) (typed FeaturePython)
  Dunit = g/cm3
  Dvalue = 5.31
  Group = -> [Ga_element001,As_element001]
  conduct = 2
  density = 1
  expand = 3
  formula = G4_GALLIUM_ARSENIDE
  name = G4_GALLIUM_ARSENIDE
  specific = 4
FEATURE [App::DocumentObjectGroupPython] H_element041  label="H_element : 0.081"  # scripted group (container) (typed FeaturePython)
  n = 0.08118
FEATURE [App::DocumentObjectGroupPython] C_element048  label="C_element : 0.416"  # scripted group (container) (typed FeaturePython)
  n = 0.41606
FEATURE [App::DocumentObjectGroupPython] N_element018  label="N_element : 0.111"  # scripted group (container) (typed FeaturePython)
  n = 0.11124
FEATURE [App::DocumentObjectGroupPython] O_element042  label="O_element : 0.381"  # scripted group (container) (typed FeaturePython)
  n = 0.38064
FEATURE [App::DocumentObjectGroupPython] S_element013  label="S_element : 0.011"  # scripted group (container) (typed FeaturePython)
  n = 0.01088
FEATURE [App::DocumentObjectGroupPython] G4_GEL_PHOTO_EMULSION  # scripted group (container) (typed FeaturePython)
  Dunit = g/cm3
  Dvalue = 1.2914
  Group = -> [H_element041,C_element048,N_element018,O_element042,S_element013]
  conduct = 2
  density = 1
  expand = 3
  formula = G4_GEL_PHOTO_EMULSION
  name = G4_GEL_PHOTO_EMULSION
  specific = 4
FEATURE [App::DocumentObjectGroupPython] B_element004  label="B_element : 0.040"  # scripted group (container) (typed FeaturePython)
  n = 0.0400639
FEATURE [App::DocumentObjectGroupPython] O_element043  label="O_element : 0.540"  # scripted group (container) (typed FeaturePython)
  n = 0.539561
FEATURE [App::DocumentObjectGroupPython] Na_element008  label="Na_element : 0.028"  # scripted group (container) (typed FeaturePython)
  n = 0.0281909
FEATURE [App::DocumentObjectGroupPython] Al_element003  label="Al_element : 0.012"  # scripted group (container) (typed FeaturePython)
  n = 0.011644
FEATURE [App::DocumentObjectGroupPython] Si_element003  label="Si_element : 0.377"  # scripted group (container) (typed FeaturePython)
  n = 0.377219
FEATURE [App::DocumentObjectGroupPython] K_element004  label="K_element : 0.014"  # scripted group (container) (typed FeaturePython)
  n = 0.00332099
FEATURE [App::DocumentObjectGroupPython] G4_Pyrex_Glass  # scripted group (container) (typed FeaturePython)
  Dunit = g/cm3
  Dvalue = 2.23
  Group = -> [B_element004,O_element043,Na_element008,Al_element003,Si_element003,K_element004]
  conduct = 2
  density = 1
  expand = 3
  formula = G4_Pyrex_Glass
  name = G4_Pyrex_Glass
  specific = 4
FEATURE [App::DocumentObjectGroupPython] O_element044  label="O_element : 0.156"  # scripted group (container) (typed FeaturePython)
  n = 0.156453
FEATURE [App::DocumentObjectGroupPython] Si_element004  label="Si_element : 0.081"  # scripted group (container) (typed FeaturePython)
  n = 0.080866
FEATURE [App::DocumentObjectGroupPython] Ti_element001  label="Ti_element : 0.008"  # scripted group (container) (typed FeaturePython)
  n = 0.008092
FEATURE [App::DocumentObjectGroupPython] As_element002  label="As_element : 0.003"  # scripted group (container) (typed FeaturePython)
  n = 0.002651
FEATURE [App::DocumentObjectGroupPython] Pb_element001  label="Pb_element : 0.752"  # scripted group (container) (typed FeaturePython)
  n = 0.751938
FEATURE [App::DocumentObjectGroupPython] G4_GLASS_LEAD  # scripted group (container) (typed FeaturePython)
  Dunit = g/cm3
  Dvalue = 6.22
  Group = -> [O_element044,Si_element004,Ti_element001,As_element002,Pb_element001]
  conduct = 2
  density = 1
  expand = 3
  formula = G4_GLASS_LEAD
  name = G4_GLASS_LEAD
  specific = 4
FEATURE [App::DocumentObjectGroupPython] O_element045  label="O_element : 0.460"  # scripted group (container) (typed FeaturePython)
  n = 0.4598
FEATURE [App::DocumentObjectGroupPython] Na_element009  label="Na_element : 0.096"  # scripted group (container) (typed FeaturePython)
  n = 0.0964411
FEATURE [App::DocumentObjectGroupPython] Si_element005  label="Si_element : 0.378"  # scripted group (container) (typed FeaturePython)
  n = 0.336553
FEATURE [App::DocumentObjectGroupPython] Ca_element011  label="Ca_element : 0.107"  # scripted group (container) (typed FeaturePython)
  n = 0.107205
FEATURE [App::DocumentObjectGroupPython] G4_GLASS_PLATE  # scripted group (container) (typed FeaturePython)
  Dunit = g/cm3
  Dvalue = 2.4
  Group = -> [O_element045,Na_element009,Si_element005,Ca_element011]
  conduct = 2
  density = 1
  expand = 3
  formula = G4_GLASS_PLATE
  name = G4_GLASS_PLATE
  specific = 4
FEATURE [App::DocumentObjectGroupPython] C_element049  label="C_element : 026"  # scripted group (container) (typed FeaturePython)
  n = 5
  ref = C_element
FEATURE [App::DocumentObjectGroupPython] H_element042  label="H_element : 021"  # scripted group (container) (typed FeaturePython)
  n = 10
  ref = H_element
FEATURE [App::DocumentObjectGroupPython] N_element019  label="N_element : 2"  # scripted group (container) (typed FeaturePython)
  n = 2
  ref = N_element
FEATURE [App::DocumentObjectGroupPython] O_element046  label="O_element : 022"  # scripted group (container) (typed FeaturePython)
  n = 3
  ref = O_element
FEATURE [App::DocumentObjectGroupPython] G4_GLUTAMINE  # scripted group (container) (typed FeaturePython)
  Dunit = g/cm3
  Dvalue = 1.46
  Group = -> [C_element049,H_element042,N_element019,O_element046]
  conduct = 2
  density = 1
  expand = 3
  formula = G4_GLUTAMINE
  name = G4_GLUTAMINE
  specific = 4
FEATURE [App::DocumentObjectGroupPython] C_element050  label="C_element : 027"  # scripted group (container) (typed FeaturePython)
  n = 3
  ref = C_element
FEATURE [App::DocumentObjectGroupPython] H_element043  label="H_element : 022"  # scripted group (container) (typed FeaturePython)
  n = 8
  ref = H_element
FEATURE [App::DocumentObjectGroupPython] O_element047  label="O_element : 023"  # scripted group (container) (typed FeaturePython)
  n = 3
  ref = O_element
FEATURE [App::DocumentObjectGroupPython] G4_GLYCEROL  # scripted group (container) (typed FeaturePython)
  Dunit = g/cm3
  Dvalue = 1.2613
  Group = -> [C_element050,H_element043,O_element047]
  conduct = 2
  density = 1
  expand = 3
  formula = G4_GLYCEROL
  name = G4_GLYCEROL
  specific = 4
FEATURE [App::DocumentObjectGroupPython] C_element051  label="C_element : 028"  # scripted group (container) (typed FeaturePython)
  n = 5
  ref = C_element
FEATURE [App::DocumentObjectGroupPython] H_element044  label="H_element : 023"  # scripted group (container) (typed FeaturePython)
  n = 5
  ref = H_element
FEATURE [App::DocumentObjectGroupPython] N_element020  label="N_element : 009"  # scripted group (container) (typed FeaturePython)
  n = 5
  ref = N_element
FEATURE [App::DocumentObjectGroupPython] O_element048  label="O_element : 024"  # scripted group (container) (typed FeaturePython)
  n = 1
  ref = O_element
FEATURE [App::DocumentObjectGroupPython] G4_GUANINE  # scripted group (container) (typed FeaturePython)
  Dunit = g/cm3
  Dvalue = 2.2
  Group = -> [C_element051,H_element044,N_element020,O_element048]
  conduct = 2
  density = 1
  expand = 3
  formula = G4_GUANINE
  name = G4_GUANINE
  specific = 4
FEATURE [App::DocumentObjectGroupPython] Ca_element012  label="Ca_element : 006"  # scripted group (container) (typed FeaturePython)
  n = 1
  ref = Ca_element
FEATURE [App::DocumentObjectGroupPython] S_element014  label="S_element : 005"  # scripted group (container) (typed FeaturePython)
  n = 1
  ref = S_element
FEATURE [App::DocumentObjectGroupPython] O_element049  label="O_element : 6"  # scripted group (container) (typed FeaturePython)
  n = 6
  ref = O_element
FEATURE [App::DocumentObjectGroupPython] H_element045  label="H_element : 024"  # scripted group (container) (typed FeaturePython)
  n = 4
  ref = H_element
FEATURE [App::DocumentObjectGroupPython] G4_GYPSUM  # scripted group (container) (typed FeaturePython)
  Dunit = g/cm3
  Dvalue = 2.32
  Group = -> [Ca_element012,S_element014,O_element049,H_element045]
  conduct = 2
  density = 1
  expand = 3
  formula = G4_GYPSUM
  name = G4_GYPSUM
  specific = 4
FEATURE [App::DocumentObjectGroupPython] C_element052  label="C_element : 7"  # scripted group (container) (typed FeaturePython)
  n = 7
  ref = C_element
FEATURE [App::DocumentObjectGroupPython] H_element046  label="H_element : 16"  # scripted group (container) (typed FeaturePython)
  n = 16
  ref = H_element
FEATURE [App::DocumentObjectGroupPython] G4_N_HEPTANE  label="G4_N-HEPTANE"  # scripted group (container) (typed FeaturePython)
  Dunit = g/cm3
  Dvalue = 0.68376
  Group = -> [C_element052,H_element046]
  conduct = 2
  density = 1
  expand = 3
  formula = G4_N-HEPTANE
  name = G4_N-HEPTANE
  specific = 4
FEATURE [App::DocumentObjectGroupPython] C_element053  label="C_element : 029"  # scripted group (container) (typed FeaturePython)
  n = 6
  ref = C_element
FEATURE [App::DocumentObjectGroupPython] H_element047  label="H_element : 14"  # scripted group (container) (typed FeaturePython)
  n = 14
  ref = H_element
FEATURE [App::DocumentObjectGroupPython] G4_N_HEXANE  label="G4_N-HEXANE"  # scripted group (container) (typed FeaturePython)
  Dunit = g/cm3
  Dvalue = 0.6603
  Group = -> [C_element053,H_element047]
  conduct = 2
  density = 1
  expand = 3
  formula = G4_N-HEXANE
  name = G4_N-HEXANE
  specific = 4
FEATURE [App::DocumentObjectGroupPython] C_element054  label="C_element : 22"  # scripted group (container) (typed FeaturePython)
  n = 22
  ref = C_element
FEATURE [App::DocumentObjectGroupPython] H_element048  label="H_element : 025"  # scripted group (container) (typed FeaturePython)
  n = 10
  ref = H_element
FEATURE [App::DocumentObjectGroupPython] N_element021  label="N_element : 010"  # scripted group (container) (typed FeaturePython)
  n = 2
  ref = N_element
FEATURE [App::DocumentObjectGroupPython] O_element050  label="O_element : 025"  # scripted group (container) (typed FeaturePython)
  n = 5
  ref = O_element
FEATURE [App::DocumentObjectGroupPython] G4_KAPTON  # scripted group (container) (typed FeaturePython)
  Dunit = g/cm3
  Dvalue = 1.42
  Group = -> [C_element054,H_element048,N_element021,O_element050]
  conduct = 2
  density = 1
  expand = 3
  formula = G4_KAPTON
  name = G4_KAPTON
  specific = 4
FEATURE [App::DocumentObjectGroupPython] La_element001  label="La_element : 1"  # scripted group (container) (typed FeaturePython)
  n = 1
  ref = La_element
FEATURE [App::DocumentObjectGroupPython] Br_element003  label="Br_element : 002"  # scripted group (container) (typed FeaturePython)
  n = 1
  ref = Br_element
FEATURE [App::DocumentObjectGroupPython] O_element051  label="O_element : 026"  # scripted group (container) (typed FeaturePython)
  n = 1
  ref = O_element
FEATURE [App::DocumentObjectGroupPython] G4_LANTHANUM_OXYBROMIDE  # scripted group (container) (typed FeaturePython)
  Dunit = g/cm3
  Dvalue = 6.28
  Group = -> [La_element001,Br_element003,O_element051]
  conduct = 2
  density = 1
  expand = 3
  formula = G4_LANTHANUM_OXYBROMIDE
  name = G4_LANTHANUM_OXYBROMIDE
  specific = 4
FEATURE [App::DocumentObjectGroupPython] La_element002  label="La_element : 2"  # scripted group (container) (typed FeaturePython)
  n = 2
  ref = La_element
FEATURE [App::DocumentObjectGroupPython] O_element052  label="O_element : 027"  # scripted group (container) (typed FeaturePython)
  n = 2
  ref = O_element
FEATURE [App::DocumentObjectGroupPython] S_element015  label="S_element : 006"  # scripted group (container) (typed FeaturePython)
  n = 1
  ref = S_element
FEATURE [App::DocumentObjectGroupPython] G4_LANTHANUM_OXYSULFIDE  # scripted group (container) (typed FeaturePython)
  Dunit = g/cm3
  Dvalue = 5.86
  Group = -> [La_element002,O_element052,S_element015]
  conduct = 2
  density = 1
  expand = 3
  formula = G4_LANTHANUM_OXYSULFIDE
  name = G4_LANTHANUM_OXYSULFIDE
  specific = 4
FEATURE [App::DocumentObjectGroupPython] O_element053  label="O_element : 0.072"  # scripted group (container) (typed FeaturePython)
  n = 0.071682
FEATURE [App::DocumentObjectGroupPython] Pb_element002  label="Pb_element : 0.928"  # scripted group (container) (typed FeaturePython)
  n = 0.928318
FEATURE [App::DocumentObjectGroupPython] G4_LEAD_OXIDE  # scripted group (container) (typed FeaturePython)
  Dunit = g/cm3
  Dvalue = 9.53
  Group = -> [O_element053,Pb_element002]
  conduct = 2
  density = 1
  expand = 3
  formula = G4_LEAD_OXIDE
  name = G4_LEAD_OXIDE
  specific = 4
FEATURE [App::DocumentObjectGroupPython] Li_element001  label="Li_element : 1"  # scripted group (container) (typed FeaturePython)
  n = 1
  ref = Li_element
FEATURE [App::DocumentObjectGroupPython] N_element022  label="N_element : 011"  # scripted group (container) (typed FeaturePython)
  n = 1
  ref = N_element
FEATURE [App::DocumentObjectGroupPython] H_element049  label="H_element : 026"  # scripted group (container) (typed FeaturePython)
  n = 2
  ref = H_element
FEATURE [App::DocumentObjectGroupPython] G4_LITHIUM_AMIDE  # scripted group (container) (typed FeaturePython)
  Dunit = g/cm3
  Dvalue = 1.178
  Group = -> [Li_element001,N_element022,H_element049]
  conduct = 2
  density = 1
  expand = 3
  formula = G4_LITHIUM_AMIDE
  name = G4_LITHIUM_AMIDE
  specific = 4
FEATURE [App::DocumentObjectGroupPython] Li_element002  label="Li_element : 2"  # scripted group (container) (typed FeaturePython)
  n = 2
  ref = Li_element
FEATURE [App::DocumentObjectGroupPython] C_element055  label="C_element : 030"  # scripted group (container) (typed FeaturePython)
  n = 1
  ref = C_element
FEATURE [App::DocumentObjectGroupPython] O_element054  label="O_element : 028"  # scripted group (container) (typed FeaturePython)
  n = 3
  ref = O_element
FEATURE [App::DocumentObjectGroupPython] G4_LITHIUM_CARBONATE  # scripted group (container) (typed FeaturePython)
  Dunit = g/cm3
  Dvalue = 2.11
  Group = -> [Li_element002,C_element055,O_element054]
  conduct = 2
  density = 1
  expand = 3
  formula = G4_LITHIUM_CARBONATE
  name = G4_LITHIUM_CARBONATE
  specific = 4
FEATURE [App::DocumentObjectGroupPython] Li_element003  label="Li_element : 003"  # scripted group (container) (typed FeaturePython)
  n = 1
  ref = Li_element
FEATURE [App::DocumentObjectGroupPython] F_element012  label="F_element : 004"  # scripted group (container) (typed FeaturePython)
  n = 1
  ref = F_element
FEATURE [App::DocumentObjectGroupPython] G4_LITHIUM_FLUORIDE  # scripted group (container) (typed FeaturePython)
  Dunit = g/cm3
  Dvalue = 2.635
  Group = -> [Li_element003,F_element012]
  conduct = 2
  density = 1
  expand = 3
  formula = G4_LITHIUM_FLUORIDE
  name = G4_LITHIUM_FLUORIDE
  specific = 4
FEATURE [App::DocumentObjectGroupPython] Li_element004  label="Li_element : 004"  # scripted group (container) (typed FeaturePython)
  n = 1
  ref = Li_element
FEATURE [App::DocumentObjectGroupPython] H_element050  label="H_element : 027"  # scripted group (container) (typed FeaturePython)
  n = 1
  ref = H_element
FEATURE [App::DocumentObjectGroupPython] G4_LITHIUM_HYDRIDE  # scripted group (container) (typed FeaturePython)
  Dunit = g/cm3
  Dvalue = 0.82
  Group = -> [Li_element004,H_element050]
  conduct = 2
  density = 1
  expand = 3
  formula = G4_LITHIUM_HYDRIDE
  name = G4_LITHIUM_HYDRIDE
  specific = 4
FEATURE [App::DocumentObjectGroupPython] Li_element005  label="Li_element : 005"  # scripted group (container) (typed FeaturePython)
  n = 1
  ref = Li_element
FEATURE [App::DocumentObjectGroupPython] I_element003  label="I_element : 002"  # scripted group (container) (typed FeaturePython)
  n = 1
  ref = I_element
FEATURE [App::DocumentObjectGroupPython] G4_LITHIUM_IODIDE  # scripted group (container) (typed FeaturePython)
  Dunit = g/cm3
  Dvalue = 3.494
  Group = -> [Li_element005,I_element003]
  conduct = 2
  density = 1
  expand = 3
  formula = G4_LITHIUM_IODIDE
  name = G4_LITHIUM_IODIDE
  specific = 4
FEATURE [App::DocumentObjectGroupPython] Li_element006  label="Li_element : 006"  # scripted group (container) (typed FeaturePython)
  n = 2
  ref = Li_element
FEATURE [App::DocumentObjectGroupPython] O_element055  label="O_element : 029"  # scripted group (container) (typed FeaturePython)
  n = 1
  ref = O_element
FEATURE [App::DocumentObjectGroupPython] G4_LITHIUM_OXIDE  # scripted group (container) (typed FeaturePython)
  Dunit = g/cm3
  Dvalue = 2.013
  Group = -> [Li_element006,O_element055]
  conduct = 2
  density = 1
  expand = 3
  formula = G4_LITHIUM_OXIDE
  name = G4_LITHIUM_OXIDE
  specific = 4
FEATURE [App::DocumentObjectGroupPython] Li_element007  label="Li_element : 007"  # scripted group (container) (typed FeaturePython)
  n = 2
  ref = Li_element
FEATURE [App::DocumentObjectGroupPython] B_element005  label="B_element : 005"  # scripted group (container) (typed FeaturePython)
  n = 4
  ref = B_element
FEATURE [App::DocumentObjectGroupPython] O_element056  label="O_element : 7"  # scripted group (container) (typed FeaturePython)
  n = 7
  ref = O_element
FEATURE [App::DocumentObjectGroupPython] G4_LITHIUM_TETRABORATE  # scripted group (container) (typed FeaturePython)
  Dunit = g/cm3
  Dvalue = 2.44
  Group = -> [Li_element007,B_element005,O_element056]
  conduct = 2
  density = 1
  expand = 3
  formula = G4_LITHIUM_TETRABORATE
  name = G4_LITHIUM_TETRABORATE
  specific = 4
FEATURE [App::DocumentObjectGroupPython] H_element051  label="H_element : 0.105"  # scripted group (container) (typed FeaturePython)
  n = 0.105
FEATURE [App::DocumentObjectGroupPython] C_element056  label="C_element : 0.083"  # scripted group (container) (typed FeaturePython)
  n = 0.083
FEATURE [App::DocumentObjectGroupPython] N_element023  label="N_element : 0.023"  # scripted group (container) (typed FeaturePython)
  n = 0.023
FEATURE [App::DocumentObjectGroupPython] O_element057  label="O_element : 0.779"  # scripted group (container) (typed FeaturePython)
  n = 0.779
FEATURE [App::DocumentObjectGroupPython] Na_element010  label="Na_element : 0.097"  # scripted group (container) (typed FeaturePython)
  n = 0.002
FEATURE [App::DocumentObjectGroupPython] P_element006  label="P_element : 0.105"  # scripted group (container) (typed FeaturePython)
  n = 0.001
FEATURE [App::DocumentObjectGroupPython] S_element016  label="S_element : 0.017"  # scripted group (container) (typed FeaturePython)
  n = 0.002
FEATURE [App::DocumentObjectGroupPython] Cl_element014  label="Cl_element : 0.587"  # scripted group (container) (typed FeaturePython)
  n = 0.003
FEATURE [App::DocumentObjectGroupPython] K_element005  label="K_element : 0.015"  # scripted group (container) (typed FeaturePython)
  n = 0.002
FEATURE [App::DocumentObjectGroupPython] G4_LUNG_ICRP  # scripted group (container) (typed FeaturePython)
  Dunit = g/cm3
  Dvalue = 1.04
  Group = -> [H_element051,C_element056,N_element023,O_element057,Na_element010,P_element006,S_element016,Cl_element014,K_element005]
  conduct = 2
  density = 1
  expand = 3
  formula = G4_LUNG_ICRP
  name = G4_LUNG_ICRP
  specific = 4
FEATURE [App::DocumentObjectGroupPython] H_element052  label="H_element : 0.116"  # scripted group (container) (typed FeaturePython)
  n = 0.114318
FEATURE [App::DocumentObjectGroupPython] C_element057  label="C_element : 0.656"  # scripted group (container) (typed FeaturePython)
  n = 0.655824
FEATURE [App::DocumentObjectGroupPython] O_element058  label="O_element : 0.092"  # scripted group (container) (typed FeaturePython)
  n = 0.0921831
FEATURE [App::DocumentObjectGroupPython] Mg_element004  label="Mg_element : 0.135"  # scripted group (container) (typed FeaturePython)
  n = 0.134792
FEATURE [App::DocumentObjectGroupPython] Ca_element013  label="Ca_element : 0.003"  # scripted group (container) (typed FeaturePython)
  n = 0.002883
FEATURE [App::DocumentObjectGroupPython] G4_M3_WAX  # scripted group (container) (typed FeaturePython)
  Dunit = g/cm3
  Dvalue = 1.05
  Group = -> [H_element052,C_element057,O_element058,Mg_element004,Ca_element013]
  conduct = 2
  density = 1
  expand = 3
  formula = G4_M3_WAX
  name = G4_M3_WAX
  specific = 4
FEATURE [App::DocumentObjectGroupPython] Mg_element005  label="Mg_element : 1"  # scripted group (container) (typed FeaturePython)
  n = 1
  ref = Mg_element
FEATURE [App::DocumentObjectGroupPython] C_element058  label="C_element : 031"  # scripted group (container) (typed FeaturePython)
  n = 1
  ref = C_element
FEATURE [App::DocumentObjectGroupPython] O_element059  label="O_element : 030"  # scripted group (container) (typed FeaturePython)
  n = 3
  ref = O_element
FEATURE [App::DocumentObjectGroupPython] G4_MAGNESIUM_CARBONATE  # scripted group (container) (typed FeaturePython)
  Dunit = g/cm3
  Dvalue = 2.958
  Group = -> [Mg_element005,C_element058,O_element059]
  conduct = 2
  density = 1
  expand = 3
  formula = G4_MAGNESIUM_CARBONATE
  name = G4_MAGNESIUM_CARBONATE
  specific = 4
FEATURE [App::DocumentObjectGroupPython] Mg_element006  label="Mg_element : 002"  # scripted group (container) (typed FeaturePython)
  n = 1
  ref = Mg_element
FEATURE [App::DocumentObjectGroupPython] F_element013  label="F_element : 005"  # scripted group (container) (typed FeaturePython)
  n = 2
  ref = F_element
FEATURE [App::DocumentObjectGroupPython] G4_MAGNESIUM_FLUORIDE  # scripted group (container) (typed FeaturePython)
  Dunit = g/cm3
  Dvalue = 3
  Group = -> [Mg_element006,F_element013]
  conduct = 2
  density = 1
  expand = 3
  formula = G4_MAGNESIUM_FLUORIDE
  name = G4_MAGNESIUM_FLUORIDE
  specific = 4
FEATURE [App::DocumentObjectGroupPython] Mg_element007  label="Mg_element : 003"  # scripted group (container) (typed FeaturePython)
  n = 1
  ref = Mg_element
FEATURE [App::DocumentObjectGroupPython] O_element060  label="O_element : 031"  # scripted group (container) (typed FeaturePython)
  n = 1
  ref = O_element
FEATURE [App::DocumentObjectGroupPython] G4_MAGNESIUM_OXIDE  # scripted group (container) (typed FeaturePython)
  Dunit = g/cm3
  Dvalue = 3.58
  Group = -> [Mg_element007,O_element060]
  conduct = 2
  density = 1
  expand = 3
  formula = G4_MAGNESIUM_OXIDE
  name = G4_MAGNESIUM_OXIDE
  specific = 4
FEATURE [App::DocumentObjectGroupPython] Mg_element008  label="Mg_element : 004"  # scripted group (container) (typed FeaturePython)
  n = 1
  ref = Mg_element
FEATURE [App::DocumentObjectGroupPython] B_element006  label="B_element : 006"  # scripted group (container) (typed FeaturePython)
  n = 4
  ref = B_element
FEATURE [App::DocumentObjectGroupPython] O_element061  label="O_element : 032"  # scripted group (container) (typed FeaturePython)
  n = 7
  ref = O_element
FEATURE [App::DocumentObjectGroupPython] G4_MAGNESIUM_TETRABORATE  # scripted group (container) (typed FeaturePython)
  Dunit = g/cm3
  Dvalue = 2.53
  Group = -> [Mg_element008,B_element006,O_element061]
  conduct = 2
  density = 1
  expand = 3
  formula = G4_MAGNESIUM_TETRABORATE
  name = G4_MAGNESIUM_TETRABORATE
  specific = 4
FEATURE [App::DocumentObjectGroupPython] Hg_element001  label="Hg_element : 1"  # scripted group (container) (typed FeaturePython)
  n = 1
  ref = Hg_element
FEATURE [App::DocumentObjectGroupPython] I_element004  label="I_element : 2"  # scripted group (container) (typed FeaturePython)
  n = 2
  ref = I_element
FEATURE [App::DocumentObjectGroupPython] G4_MERCURIC_IODIDE  # scripted group (container) (typed FeaturePython)
  Dunit = g/cm3
  Dvalue = 6.36
  Group = -> [Hg_element001,I_element004]
  conduct = 2
  density = 1
  expand = 3
  formula = G4_MERCURIC_IODIDE
  name = G4_MERCURIC_IODIDE
  specific = 4
FEATURE [App::DocumentObjectGroupPython] C_element059  label="C_element : 032"  # scripted group (container) (typed FeaturePython)
  n = 1
  ref = C_element
FEATURE [App::DocumentObjectGroupPython] H_element053  label="H_element : 028"  # scripted group (container) (typed FeaturePython)
  n = 4
  ref = H_element
FEATURE [App::DocumentObjectGroupPython] G4_METHANE  # scripted group (container) (typed FeaturePython)
  Dunit = g/cm3
  Dvalue = 0.000667151
  Group = -> [C_element059,H_element053]
  conduct = 2
  density = 1
  expand = 3
  formula = G4_METHANE
  name = G4_METHANE
  specific = 4
FEATURE [App::DocumentObjectGroupPython] C_element060  label="C_element : 033"  # scripted group (container) (typed FeaturePython)
  n = 1
  ref = C_element
FEATURE [App::DocumentObjectGroupPython] H_element054  label="H_element : 029"  # scripted group (container) (typed FeaturePython)
  n = 4
  ref = H_element
FEATURE [App::DocumentObjectGroupPython] O_element062  label="O_element : 033"  # scripted group (container) (typed FeaturePython)
  n = 1
  ref = O_element
FEATURE [App::DocumentObjectGroupPython] G4_METHANOL  # scripted group (container) (typed FeaturePython)
  Dunit = g/cm3
  Dvalue = 0.7914
  Group = -> [C_element060,H_element054,O_element062]
  conduct = 2
  density = 1
  expand = 3
  formula = G4_METHANOL
  name = G4_METHANOL
  specific = 4
FEATURE [App::DocumentObjectGroupPython] H_element055  label="H_element : 0.134"  # scripted group (container) (typed FeaturePython)
  n = 0.13404
FEATURE [App::DocumentObjectGroupPython] C_element061  label="C_element : 0.778"  # scripted group (container) (typed FeaturePython)
  n = 0.77796
FEATURE [App::DocumentObjectGroupPython] O_element063  label="O_element : 0.035"  # scripted group (container) (typed FeaturePython)
  n = 0.03502
FEATURE [App::DocumentObjectGroupPython] Mg_element009  label="Mg_element : 0.039"  # scripted group (container) (typed FeaturePython)
  n = 0.038594
FEATURE [App::DocumentObjectGroupPython] Ti_element002  label="Ti_element : 0.014"  # scripted group (container) (typed FeaturePython)
  n = 0.014386
FEATURE [App::DocumentObjectGroupPython] G4_MIX_D_WAX  # scripted group (container) (typed FeaturePython)
  Dunit = g/cm3
  Dvalue = 0.99
  Group = -> [H_element055,C_element061,O_element063,Mg_element009,Ti_element002]
  conduct = 2
  density = 1
  expand = 3
  formula = G4_MIX_D_WAX
  name = G4_MIX_D_WAX
  specific = 4
FEATURE [App::DocumentObjectGroupPython] H_element056  label="H_element : 0.135"  # scripted group (container) (typed FeaturePython)
  n = 0.081192
FEATURE [App::DocumentObjectGroupPython] C_element062  label="C_element : 0.583"  # scripted group (container) (typed FeaturePython)
  n = 0.583442
FEATURE [App::DocumentObjectGroupPython] N_element024  label="N_element : 0.018"  # scripted group (container) (typed FeaturePython)
  n = 0.017798
FEATURE [App::DocumentObjectGroupPython] O_element064  label="O_element : 0.186"  # scripted group (container) (typed FeaturePython)
  n = 0.186381
FEATURE [App::DocumentObjectGroupPython] Mg_element010  label="Mg_element : 0.130"  # scripted group (container) (typed FeaturePython)
  n = 0.130287
FEATURE [App::DocumentObjectGroupPython] Cl_element015  label="Cl_element : 0.588"  # scripted group (container) (typed FeaturePython)
  n = 0.0009
FEATURE [App::DocumentObjectGroupPython] G4_MS20_TISSUE  # scripted group (container) (typed FeaturePython)
  Dunit = g/cm3
  Dvalue = 1
  Group = -> [H_element056,C_element062,N_element024,O_element064,Mg_element010,Cl_element015]
  conduct = 2
  density = 1
  expand = 3
  formula = G4_MS20_TISSUE
  name = G4_MS20_TISSUE
  specific = 4
FEATURE [App::DocumentObjectGroupPython] H_element057  label="H_element : 0.136"  # scripted group (container) (typed FeaturePython)
  n = 0.102
FEATURE [App::DocumentObjectGroupPython] C_element063  label="C_element : 0.143"  # scripted group (container) (typed FeaturePython)
  n = 0.143
FEATURE [App::DocumentObjectGroupPython] N_element025  label="N_element : 0.034"  # scripted group (container) (typed FeaturePython)
  n = 0.034
FEATURE [App::DocumentObjectGroupPython] O_element065  label="O_element : 0.710"  # scripted group (container) (typed FeaturePython)
  n = 0.71
FEATURE [App::DocumentObjectGroupPython] Na_element011  label="Na_element : 0.098"  # scripted group (container) (typed FeaturePython)
  n = 0.001
FEATURE [App::DocumentObjectGroupPython] P_element007  label="P_element : 0.002"  # scripted group (container) (typed FeaturePython)
  n = 0.002
FEATURE [App::DocumentObjectGroupPython] S_element017  label="S_element : 0.018"  # scripted group (container) (typed FeaturePython)
  n = 0.003
FEATURE [App::DocumentObjectGroupPython] Cl_element016  label="Cl_element : 0.589"  # scripted group (container) (typed FeaturePython)
  n = 0.001
FEATURE [App::DocumentObjectGroupPython] K_element006  label="K_element : 0.004"  # scripted group (container) (typed FeaturePython)
  n = 0.004
FEATURE [App::DocumentObjectGroupPython] G4_MUSCLE_SKELETAL_ICRP  # scripted group (container) (typed FeaturePython)
  Dunit = g/cm3
  Dvalue = 1.05
  Group = -> [H_element057,C_element063,N_element025,O_element065,Na_element011,P_element007,S_element017,Cl_element016,K_element006]
  conduct = 2
  density = 1
  expand = 3
  formula = G4_MUSCLE_SKELETAL_ICRP
  name = G4_MUSCLE_SKELETAL_ICRP
  specific = 4
FEATURE [App::DocumentObjectGroupPython] H_element058  label="H_element : 0.137"  # scripted group (container) (typed FeaturePython)
  n = 0.102102
FEATURE [App::DocumentObjectGroupPython] C_element064  label="C_element : 0.123"  # scripted group (container) (typed FeaturePython)
  n = 0.123123
FEATURE [App::DocumentObjectGroupPython] N_element026  label="N_element : 0.756"  # scripted group (container) (typed FeaturePython)
  n = 0.035035
FEATURE [App::DocumentObjectGroupPython] O_element066  label="O_element : 0.730"  # scripted group (container) (typed FeaturePython)
  n = 0.72973
FEATURE [App::DocumentObjectGroupPython] Na_element012  label="Na_element : 0.099"  # scripted group (container) (typed FeaturePython)
  n = 0.001001
FEATURE [App::DocumentObjectGroupPython] P_element008  label="P_element : 0.106"  # scripted group (container) (typed FeaturePython)
  n = 0.002002
FEATURE [App::DocumentObjectGroupPython] S_element018  label="S_element : 0.019"  # scripted group (container) (typed FeaturePython)
  n = 0.004004
FEATURE [App::DocumentObjectGroupPython] K_element007  label="K_element : 0.016"  # scripted group (container) (typed FeaturePython)
  n = 0.003003
FEATURE [App::DocumentObjectGroupPython] G4_MUSCLE_STRIATED_ICRU  # scripted group (container) (typed FeaturePython)
  Dunit = g/cm3
  Dvalue = 1.04
  Group = -> [H_element058,C_element064,N_element026,O_element066,Na_element012,P_element008,S_element018,K_element007]
  conduct = 2
  density = 1
  expand = 3
  formula = G4_MUSCLE_STRIATED_ICRU
  name = G4_MUSCLE_STRIATED_ICRU
  specific = 4
FEATURE [App::DocumentObjectGroupPython] H_element059  label="H_element : 0.098"  # scripted group (container) (typed FeaturePython)
  n = 0.0982341
FEATURE [App::DocumentObjectGroupPython] C_element065  label="C_element : 0.156"  # scripted group (container) (typed FeaturePython)
  n = 0.156214
FEATURE [App::DocumentObjectGroupPython] N_element027  label="N_element : 0.757"  # scripted group (container) (typed FeaturePython)
  n = 0.035451
FEATURE [App::DocumentObjectGroupPython] O_element067  label="O_element : 0.880"  # scripted group (container) (typed FeaturePython)
  n = 0.710101
FEATURE [App::DocumentObjectGroupPython] G4_MUSCLE_WITH_SUCROSE  # scripted group (container) (typed FeaturePython)
  Dunit = g/cm3
  Dvalue = 1.11
  Group = -> [H_element059,C_element065,N_element027,O_element067]
  conduct = 2
  density = 1
  expand = 3
  formula = G4_MUSCLE_WITH_SUCROSE
  name = G4_MUSCLE_WITH_SUCROSE
  specific = 4
FEATURE [App::DocumentObjectGroupPython] H_element060  label="H_element : 0.138"  # scripted group (container) (typed FeaturePython)
  n = 0.101969
FEATURE [App::DocumentObjectGroupPython] C_element066  label="C_element : 0.120"  # scripted group (container) (typed FeaturePython)
  n = 0.120058
FEATURE [App::DocumentObjectGroupPython] N_element028  label="N_element : 0.758"  # scripted group (container) (typed FeaturePython)
  n = 0.035451
FEATURE [App::DocumentObjectGroupPython] O_element068  label="O_element : 0.743"  # scripted group (container) (typed FeaturePython)
  n = 0.742522
FEATURE [App::DocumentObjectGroupPython] G4_MUSCLE_WITHOUT_SUCROSE  # scripted group (container) (typed FeaturePython)
  Dunit = g/cm3
  Dvalue = 1.07
  Group = -> [H_element060,C_element066,N_element028,O_element068]
  conduct = 2
  density = 1
  expand = 3
  formula = G4_MUSCLE_WITHOUT_SUCROSE
  name = G4_MUSCLE_WITHOUT_SUCROSE
  specific = 4
FEATURE [App::DocumentObjectGroupPython] C_element067  label="C_element : 10"  # scripted group (container) (typed FeaturePython)
  n = 10
  ref = C_element
FEATURE [App::DocumentObjectGroupPython] H_element061  label="H_element : 030"  # scripted group (container) (typed FeaturePython)
  n = 8
  ref = H_element
FEATURE [App::DocumentObjectGroupPython] G4_NAPHTHALENE  # scripted group (container) (typed FeaturePython)
  Dunit = g/cm3
  Dvalue = 1.145
  Group = -> [C_element067,H_element061]
  conduct = 2
  density = 1
  expand = 3
  formula = G4_NAPHTHALENE
  name = G4_NAPHTHALENE
  specific = 4
FEATURE [App::DocumentObjectGroupPython] C_element068  label="C_element : 034"  # scripted group (container) (typed FeaturePython)
  n = 6
  ref = C_element
FEATURE [App::DocumentObjectGroupPython] H_element062  label="H_element : 031"  # scripted group (container) (typed FeaturePython)
  n = 5
  ref = H_element
FEATURE [App::DocumentObjectGroupPython] N_element029  label="N_element : 012"  # scripted group (container) (typed FeaturePython)
  n = 1
  ref = N_element
FEATURE [App::DocumentObjectGroupPython] O_element069  label="O_element : 034"  # scripted group (container) (typed FeaturePython)
  n = 2
  ref = O_element
FEATURE [App::DocumentObjectGroupPython] G4_NITROBENZENE  # scripted group (container) (typed FeaturePython)
  Dunit = g/cm3
  Dvalue = 1.19867
  Group = -> [C_element068,H_element062,N_element029,O_element069]
  conduct = 2
  density = 1
  expand = 3
  formula = G4_NITROBENZENE
  name = G4_NITROBENZENE
  specific = 4
FEATURE [App::DocumentObjectGroupPython] N_element030  label="N_element : 013"  # scripted group (container) (typed FeaturePython)
  n = 2
  ref = N_element
FEATURE [App::DocumentObjectGroupPython] O_element070  label="O_element : 035"  # scripted group (container) (typed FeaturePython)
  n = 1
  ref = O_element
FEATURE [App::DocumentObjectGroupPython] G4_NITROUS_OXIDE  # scripted group (container) (typed FeaturePython)
  Dunit = g/cm3
  Dvalue = 0.00183094
  Group = -> [N_element030,O_element070]
  conduct = 2
  density = 1
  expand = 3
  formula = G4_NITROUS_OXIDE
  name = G4_NITROUS_OXIDE
  specific = 4
FEATURE [App::DocumentObjectGroupPython] H_element063  label="H_element : 0.104"  # scripted group (container) (typed FeaturePython)
  n = 0.103509
FEATURE [App::DocumentObjectGroupPython] C_element069  label="C_element : 0.648"  # scripted group (container) (typed FeaturePython)
  n = 0.648416
FEATURE [App::DocumentObjectGroupPython] N_element031  label="N_element : 0.100"  # scripted group (container) (typed FeaturePython)
  n = 0.0995361
FEATURE [App::DocumentObjectGroupPython] O_element071  label="O_element : 0.149"  # scripted group (container) (typed FeaturePython)
  n = 0.148539
FEATURE [App::DocumentObjectGroupPython] G4_NYLON_8062  label="G4_NYLON-8062"  # scripted group (container) (typed FeaturePython)
  Dunit = g/cm3
  Dvalue = 1.08
  Group = -> [H_element063,C_element069,N_element031,O_element071]
  conduct = 2
  density = 1
  expand = 3
  formula = G4_NYLON-8062
  name = G4_NYLON-8062
  specific = 4
FEATURE [App::DocumentObjectGroupPython] C_element070  label="C_element : 035"  # scripted group (container) (typed FeaturePython)
  n = 6
  ref = C_element
FEATURE [App::DocumentObjectGroupPython] H_element064  label="H_element : 11"  # scripted group (container) (typed FeaturePython)
  n = 11
  ref = H_element
FEATURE [App::DocumentObjectGroupPython] N_element032  label="N_element : 014"  # scripted group (container) (typed FeaturePython)
  n = 1
  ref = N_element
FEATURE [App::DocumentObjectGroupPython] O_element072  label="O_element : 036"  # scripted group (container) (typed FeaturePython)
  n = 1
  ref = O_element
FEATURE [App::DocumentObjectGroupPython] G4_NYLON_6_6  label="G4_NYLON-6-6"  # scripted group (container) (typed FeaturePython)
  Dunit = g/cm3
  Dvalue = 1.14
  Group = -> [C_element070,H_element064,N_element032,O_element072]
  conduct = 2
  density = 1
  expand = 3
  formula = G4_NYLON-6-6
  name = G4_NYLON-6-6
  specific = 4
FEATURE [App::DocumentObjectGroupPython] H_element065  label="H_element : 0.139"  # scripted group (container) (typed FeaturePython)
  n = 0.107062
FEATURE [App::DocumentObjectGroupPython] C_element071  label="C_element : 0.680"  # scripted group (container) (typed FeaturePython)
  n = 0.680449
FEATURE [App::DocumentObjectGroupPython] N_element033  label="N_element : 0.099"  # scripted group (container) (typed FeaturePython)
  n = 0.099189
FEATURE [App::DocumentObjectGroupPython] O_element073  label="O_element : 0.113"  # scripted group (container) (typed FeaturePython)
  n = 0.1133
FEATURE [App::DocumentObjectGroupPython] G4_NYLON_6_10  label="G4_NYLON-6-10"  # scripted group (container) (typed FeaturePython)
  Dunit = g/cm3
  Dvalue = 1.14
  Group = -> [H_element065,C_element071,N_element033,O_element073]
  conduct = 2
  density = 1
  expand = 3
  formula = G4_NYLON-6-10
  name = G4_NYLON-6-10
  specific = 4
FEATURE [App::DocumentObjectGroupPython] H_element066  label="H_element : 0.140"  # scripted group (container) (typed FeaturePython)
  n = 0.115476
FEATURE [App::DocumentObjectGroupPython] C_element072  label="C_element : 0.721"  # scripted group (container) (typed FeaturePython)
  n = 0.720818
FEATURE [App::DocumentObjectGroupPython] N_element034  label="N_element : 0.076"  # scripted group (container) (typed FeaturePython)
  n = 0.0764169
FEATURE [App::DocumentObjectGroupPython] O_element074  label="O_element : 0.087"  # scripted group (container) (typed FeaturePython)
  n = 0.0872889
FEATURE [App::DocumentObjectGroupPython] G4_NYLON_11_RILSAN  label="G4_NYLON-11_RILSAN"  # scripted group (container) (typed FeaturePython)
  Dunit = g/cm3
  Dvalue = 1.425
  Group = -> [H_element066,C_element072,N_element034,O_element074]
  conduct = 2
  density = 1
  expand = 3
  formula = G4_NYLON-11_RILSAN
  name = G4_NYLON-11_RILSAN
  specific = 4
FEATURE [App::DocumentObjectGroupPython] C_element073  label="C_element : 8"  # scripted group (container) (typed FeaturePython)
  n = 8
  ref = C_element
FEATURE [App::DocumentObjectGroupPython] H_element067  label="H_element : 18"  # scripted group (container) (typed FeaturePython)
  n = 18
  ref = H_element
FEATURE [App::DocumentObjectGroupPython] G4_OCTANE  # scripted group (container) (typed FeaturePython)
  Dunit = g/cm3
  Dvalue = 0.7026
  Group = -> [C_element073,H_element067]
  conduct = 2
  density = 1
  expand = 3
  formula = G4_OCTANE
  name = G4_OCTANE
  specific = 4
FEATURE [App::DocumentObjectGroupPython] C_element074  label="C_element : 25"  # scripted group (container) (typed FeaturePython)
  n = 25
  ref = C_element
FEATURE [App::DocumentObjectGroupPython] H_element068  label="H_element : 52"  # scripted group (container) (typed FeaturePython)
  n = 52
  ref = H_element
FEATURE [App::DocumentObjectGroupPython] G4_PARAFFIN  # scripted group (container) (typed FeaturePython)
  Dunit = g/cm3
  Dvalue = 0.93
  Group = -> [C_element074,H_element068]
  conduct = 2
  density = 1
  expand = 3
  formula = G4_PARAFFIN
  name = G4_PARAFFIN
  specific = 4
FEATURE [App::DocumentObjectGroupPython] C_element075  label="C_element : 036"  # scripted group (container) (typed FeaturePython)
  n = 5
  ref = C_element
FEATURE [App::DocumentObjectGroupPython] H_element069  label="H_element : 032"  # scripted group (container) (typed FeaturePython)
  n = 12
  ref = H_element
FEATURE [App::DocumentObjectGroupPython] G4_N_PENTANE  label="G4_N-PENTANE"  # scripted group (container) (typed FeaturePython)
  Dunit = g/cm3
  Dvalue = 0.6262
  Group = -> [C_element075,H_element069]
  conduct = 2
  density = 1
  expand = 3
  formula = G4_N-PENTANE
  name = G4_N-PENTANE
  specific = 4
FEATURE [App::DocumentObjectGroupPython] H_element070  label="H_element : 0.014"  # scripted group (container) (typed FeaturePython)
  n = 0.0141
FEATURE [App::DocumentObjectGroupPython] C_element076  label="C_element : 0.072"  # scripted group (container) (typed FeaturePython)
  n = 0.072261
FEATURE [App::DocumentObjectGroupPython] N_element035  label="N_element : 0.019"  # scripted group (container) (typed FeaturePython)
  n = 0.01932
FEATURE [App::DocumentObjectGroupPython] O_element075  label="O_element : 0.066"  # scripted group (container) (typed FeaturePython)
  n = 0.066101
FEATURE [App::DocumentObjectGroupPython] S_element019  label="S_element : 0.020"  # scripted group (container) (typed FeaturePython)
  n = 0.00189
FEATURE [App::DocumentObjectGroupPython] Br_element004  label="Br_element : 0.349"  # scripted group (container) (typed FeaturePython)
  n = 0.349103
FEATURE [App::DocumentObjectGroupPython] Ag_element001  label="Ag_element : 0.474"  # scripted group (container) (typed FeaturePython)
  n = 0.474105
FEATURE [App::DocumentObjectGroupPython] I_element005  label="I_element : 0.003"  # scripted group (container) (typed FeaturePython)
  n = 0.00312
FEATURE [App::DocumentObjectGroupPython] G4_PHOTO_EMULSION  # scripted group (container) (typed FeaturePython)
  Dunit = g/cm3
  Dvalue = 3.815
  Group = -> [H_element070,C_element076,N_element035,O_element075,S_element019,Br_element004,Ag_element001,I_element005]
  conduct = 2
  density = 1
  expand = 3
  formula = G4_PHOTO_EMULSION
  name = G4_PHOTO_EMULSION
  specific = 4
FEATURE [App::DocumentObjectGroupPython] C_element077  label="C_element : 9"  # scripted group (container) (typed FeaturePython)
  n = 9
  ref = C_element
FEATURE [App::DocumentObjectGroupPython] H_element071  label="H_element : 033"  # scripted group (container) (typed FeaturePython)
  n = 10
  ref = H_element
FEATURE [App::DocumentObjectGroupPython] G4_PLASTIC_SC_VINYLTOLUENE  # scripted group (container) (typed FeaturePython)
  Dunit = g/cm3
  Dvalue = 1.032
  Group = -> [C_element077,H_element071]
  conduct = 2
  density = 1
  expand = 3
  formula = G4_PLASTIC_SC_VINYLTOLUENE
  name = G4_PLASTIC_SC_VINYLTOLUENE
  specific = 4
FEATURE [App::DocumentObjectGroupPython] Pu_element001  label="Pu_element : 1"  # scripted group (container) (typed FeaturePython)
  n = 1
  ref = Pu_element
FEATURE [App::DocumentObjectGroupPython] O_element076  label="O_element : 037"  # scripted group (container) (typed FeaturePython)
  n = 2
  ref = O_element
FEATURE [App::DocumentObjectGroupPython] G4_PLUTONIUM_DIOXIDE  # scripted group (container) (typed FeaturePython)
  Dunit = g/cm3
  Dvalue = 11.46
  Group = -> [Pu_element001,O_element076]
  conduct = 2
  density = 1
  expand = 3
  formula = G4_PLUTONIUM_DIOXIDE
  name = G4_PLUTONIUM_DIOXIDE
  specific = 4
FEATURE [App::DocumentObjectGroupPython] C_element078  label="C_element : 037"  # scripted group (container) (typed FeaturePython)
  n = 3
  ref = C_element
FEATURE [App::DocumentObjectGroupPython] H_element072  label="H_element : 034"  # scripted group (container) (typed FeaturePython)
  n = 3
  ref = H_element
FEATURE [App::DocumentObjectGroupPython] N_element036  label="N_element : 015"  # scripted group (container) (typed FeaturePython)
  n = 1
  ref = N_element
FEATURE [App::DocumentObjectGroupPython] G4_POLYACRYLONITRILE  # scripted group (container) (typed FeaturePython)
  Dunit = g/cm3
  Dvalue = 1.17
  Group = -> [C_element078,H_element072,N_element036]
  conduct = 2
  density = 1
  expand = 3
  formula = G4_POLYACRYLONITRILE
  name = G4_POLYACRYLONITRILE
  specific = 4
FEATURE [App::DocumentObjectGroupPython] C_element079  label="C_element : 16"  # scripted group (container) (typed FeaturePython)
  n = 16
  ref = C_element
FEATURE [App::DocumentObjectGroupPython] H_element073  label="H_element : 035"  # scripted group (container) (typed FeaturePython)
  n = 14
  ref = H_element
FEATURE [App::DocumentObjectGroupPython] O_element077  label="O_element : 038"  # scripted group (container) (typed FeaturePython)
  n = 3
  ref = O_element
FEATURE [App::DocumentObjectGroupPython] G4_POLYCARBONATE  # scripted group (container) (typed FeaturePython)
  Dunit = g/cm3
  Dvalue = 1.2
  Group = -> [C_element079,H_element073,O_element077]
  conduct = 2
  density = 1
  expand = 3
  formula = G4_POLYCARBONATE
  name = G4_POLYCARBONATE
  specific = 4
FEATURE [App::DocumentObjectGroupPython] C_element080  label="C_element : 038"  # scripted group (container) (typed FeaturePython)
  n = 8
  ref = C_element
FEATURE [App::DocumentObjectGroupPython] H_element074  label="H_element : 036"  # scripted group (container) (typed FeaturePython)
  n = 7
  ref = H_element
FEATURE [App::DocumentObjectGroupPython] Cl_element017  label="Cl_element : 007"  # scripted group (container) (typed FeaturePython)
  n = 1
  ref = Cl_element
FEATURE [App::DocumentObjectGroupPython] G4_POLYCHLOROSTYRENE  # scripted group (container) (typed FeaturePython)
  Dunit = g/cm3
  Dvalue = 1.3
  Group = -> [C_element080,H_element074,Cl_element017]
  conduct = 2
  density = 1
  expand = 3
  formula = G4_POLYCHLOROSTYRENE
  name = G4_POLYCHLOROSTYRENE
  specific = 4
FEATURE [App::DocumentObjectGroupPython] C_element081  label="C_element : 039"  # scripted group (container) (typed FeaturePython)
  n = 1
  ref = C_element
FEATURE [App::DocumentObjectGroupPython] H_element075  label="H_element : 037"  # scripted group (container) (typed FeaturePython)
  n = 2
  ref = H_element
FEATURE [App::DocumentObjectGroupPython] G4_POLYETHYLENE  # scripted group (container) (typed FeaturePython)
  Dunit = g/cm3
  Dvalue = 0.94
  Group = -> [C_element081,H_element075]
  conduct = 2
  density = 1
  expand = 3
  formula = G4_POLYETHYLENE
  name = G4_POLYETHYLENE
  specific = 4
FEATURE [App::DocumentObjectGroupPython] C_element082  label="C_element : 040"  # scripted group (container) (typed FeaturePython)
  n = 10
  ref = C_element
FEATURE [App::DocumentObjectGroupPython] H_element076  label="H_element : 038"  # scripted group (container) (typed FeaturePython)
  n = 8
  ref = H_element
FEATURE [App::DocumentObjectGroupPython] O_element078  label="O_element : 039"  # scripted group (container) (typed FeaturePython)
  n = 4
  ref = O_element
FEATURE [App::DocumentObjectGroupPython] G4_MYLAR  # scripted group (container) (typed FeaturePython)
  Dunit = g/cm3
  Dvalue = 1.4
  Group = -> [C_element082,H_element076,O_element078]
  conduct = 2
  density = 1
  expand = 3
  formula = G4_MYLAR
  name = G4_MYLAR
  specific = 4
FEATURE [App::DocumentObjectGroupPython] C_element083  label="C_element : 041"  # scripted group (container) (typed FeaturePython)
  n = 5
  ref = C_element
FEATURE [App::DocumentObjectGroupPython] H_element077  label="H_element : 039"  # scripted group (container) (typed FeaturePython)
  n = 8
  ref = H_element
FEATURE [App::DocumentObjectGroupPython] O_element079  label="O_element : 040"  # scripted group (container) (typed FeaturePython)
  n = 2
  ref = O_element
FEATURE [App::DocumentObjectGroupPython] G4_PLEXIGLASS  # scripted group (container) (typed FeaturePython)
  Dunit = g/cm3
  Dvalue = 1.19
  Group = -> [C_element083,H_element077,O_element079]
  conduct = 2
  density = 1
  expand = 3
  formula = G4_PLEXIGLASS
  name = G4_PLEXIGLASS
  specific = 4
FEATURE [App::DocumentObjectGroupPython] C_element084  label="C_element : 042"  # scripted group (container) (typed FeaturePython)
  n = 1
  ref = C_element
FEATURE [App::DocumentObjectGroupPython] H_element078  label="H_element : 040"  # scripted group (container) (typed FeaturePython)
  n = 2
  ref = H_element
FEATURE [App::DocumentObjectGroupPython] O_element080  label="O_element : 041"  # scripted group (container) (typed FeaturePython)
  n = 1
  ref = O_element
FEATURE [App::DocumentObjectGroupPython] G4_POLYOXYMETHYLENE  # scripted group (container) (typed FeaturePython)
  Dunit = g/cm3
  Dvalue = 1.425
  Group = -> [C_element084,H_element078,O_element080]
  conduct = 2
  density = 1
  expand = 3
  formula = G4_POLYOXYMETHYLENE
  name = G4_POLYOXYMETHYLENE
  specific = 4
FEATURE [App::DocumentObjectGroupPython] C_element085  label="C_element : 043"  # scripted group (container) (typed FeaturePython)
  n = 2
  ref = C_element
FEATURE [App::DocumentObjectGroupPython] H_element079  label="H_element : 041"  # scripted group (container) (typed FeaturePython)
  n = 4
  ref = H_element
FEATURE [App::DocumentObjectGroupPython] G4_POLYPROPYLENE  # scripted group (container) (typed FeaturePython)
  Dunit = g/cm3
  Dvalue = 0.9
  Group = -> [C_element085,H_element079]
  conduct = 2
  density = 1
  expand = 3
  formula = G4_POLYPROPYLENE
  name = G4_POLYPROPYLENE
  specific = 4
FEATURE [App::DocumentObjectGroupPython] C_element086  label="C_element : 044"  # scripted group (container) (typed FeaturePython)
  n = 8
  ref = C_element
FEATURE [App::DocumentObjectGroupPython] H_element080  label="H_element : 042"  # scripted group (container) (typed FeaturePython)
  n = 8
  ref = H_element
FEATURE [App::DocumentObjectGroupPython] G4_POLYSTYRENE  # scripted group (container) (typed FeaturePython)
  Dunit = g/cm3
  Dvalue = 1.06
  Group = -> [C_element086,H_element080]
  conduct = 2
  density = 1
  expand = 3
  formula = G4_POLYSTYRENE
  name = G4_POLYSTYRENE
  specific = 4
FEATURE [App::DocumentObjectGroupPython] C_element087  label="C_element : 045"  # scripted group (container) (typed FeaturePython)
  n = 2
  ref = C_element
FEATURE [App::DocumentObjectGroupPython] F_element014  label="F_element : 4"  # scripted group (container) (typed FeaturePython)
  n = 4
  ref = F_element
FEATURE [App::DocumentObjectGroupPython] G4_TEFLON  # scripted group (container) (typed FeaturePython)
  Dunit = g/cm3
  Dvalue = 2.2
  Group = -> [C_element087,F_element014]
  conduct = 2
  density = 1
  expand = 3
  formula = G4_TEFLON
  name = G4_TEFLON
  specific = 4
FEATURE [App::DocumentObjectGroupPython] C_element088  label="C_element : 046"  # scripted group (container) (typed FeaturePython)
  n = 2
  ref = C_element
FEATURE [App::DocumentObjectGroupPython] F_element015  label="F_element : 006"  # scripted group (container) (typed FeaturePython)
  n = 3
  ref = F_element
FEATURE [App::DocumentObjectGroupPython] Cl_element018  label="Cl_element : 008"  # scripted group (container) (typed FeaturePython)
  n = 1
  ref = Cl_element
FEATURE [App::DocumentObjectGroupPython] G4_POLYTRIFLUOROCHLOROETHYLENE  # scripted group (container) (typed FeaturePython)
  Dunit = g/cm3
  Dvalue = 2.1
  Group = -> [C_element088,F_element015,Cl_element018]
  conduct = 2
  density = 1
  expand = 3
  formula = G4_POLYTRIFLUOROCHLOROETHYLENE
  name = G4_POLYTRIFLUOROCHLOROETHYLENE
  specific = 4
FEATURE [App::DocumentObjectGroupPython] C_element089  label="C_element : 047"  # scripted group (container) (typed FeaturePython)
  n = 4
  ref = C_element
FEATURE [App::DocumentObjectGroupPython] H_element081  label="H_element : 043"  # scripted group (container) (typed FeaturePython)
  n = 6
  ref = H_element
FEATURE [App::DocumentObjectGroupPython] O_element081  label="O_element : 042"  # scripted group (container) (typed FeaturePython)
  n = 2
  ref = O_element
FEATURE [App::DocumentObjectGroupPython] G4_POLYVINYL_ACETATE  # scripted group (container) (typed FeaturePython)
  Dunit = g/cm3
  Dvalue = 1.19
  Group = -> [C_element089,H_element081,O_element081]
  conduct = 2
  density = 1
  expand = 3
  formula = G4_POLYVINYL_ACETATE
  name = G4_POLYVINYL_ACETATE
  specific = 4
FEATURE [App::DocumentObjectGroupPython] C_element090  label="C_element : 048"  # scripted group (container) (typed FeaturePython)
  n = 2
  ref = C_element
FEATURE [App::DocumentObjectGroupPython] H_element082  label="H_element : 044"  # scripted group (container) (typed FeaturePython)
  n = 4
  ref = H_element
FEATURE [App::DocumentObjectGroupPython] O_element082  label="O_element : 043"  # scripted group (container) (typed FeaturePython)
  n = 1
  ref = O_element
FEATURE [App::DocumentObjectGroupPython] G4_POLYVINYL_ALCOHOL  # scripted group (container) (typed FeaturePython)
  Dunit = g/cm3
  Dvalue = 1.3
  Group = -> [C_element090,H_element082,O_element082]
  conduct = 2
  density = 1
  expand = 3
  formula = G4_POLYVINYL_ALCOHOL
  name = G4_POLYVINYL_ALCOHOL
  specific = 4
FEATURE [App::DocumentObjectGroupPython] C_element091  label="C_element : 049"  # scripted group (container) (typed FeaturePython)
  n = 8
  ref = C_element
FEATURE [App::DocumentObjectGroupPython] H_element083  label="H_element : 045"  # scripted group (container) (typed FeaturePython)
  n = 14
  ref = H_element
FEATURE [App::DocumentObjectGroupPython] O_element083  label="O_element : 044"  # scripted group (container) (typed FeaturePython)
  n = 2
  ref = O_element
FEATURE [App::DocumentObjectGroupPython] G4_POLYVINYL_BUTYRAL  # scripted group (container) (typed FeaturePython)
  Dunit = g/cm3
  Dvalue = 1.12
  Group = -> [C_element091,H_element083,O_element083]
  conduct = 2
  density = 1
  expand = 3
  formula = G4_POLYVINYL_BUTYRAL
  name = G4_POLYVINYL_BUTYRAL
  specific = 4
FEATURE [App::DocumentObjectGroupPython] C_element092  label="C_element : 050"  # scripted group (container) (typed FeaturePython)
  n = 2
  ref = C_element
FEATURE [App::DocumentObjectGroupPython] H_element084  label="H_element : 046"  # scripted group (container) (typed FeaturePython)
  n = 3
  ref = H_element
FEATURE [App::DocumentObjectGroupPython] Cl_element019  label="Cl_element : 009"  # scripted group (container) (typed FeaturePython)
  n = 1
  ref = Cl_element
FEATURE [App::DocumentObjectGroupPython] G4_POLYVINYL_CHLORIDE  # scripted group (container) (typed FeaturePython)
  Dunit = g/cm3
  Dvalue = 1.3
  Group = -> [C_element092,H_element084,Cl_element019]
  conduct = 2
  density = 1
  expand = 3
  formula = G4_POLYVINYL_CHLORIDE
  name = G4_POLYVINYL_CHLORIDE
  specific = 4
FEATURE [App::DocumentObjectGroupPython] C_element093  label="C_element : 051"  # scripted group (container) (typed FeaturePython)
  n = 2
  ref = C_element
FEATURE [App::DocumentObjectGroupPython] H_element085  label="H_element : 047"  # scripted group (container) (typed FeaturePython)
  n = 2
  ref = H_element
FEATURE [App::DocumentObjectGroupPython] Cl_element020  label="Cl_element : 010"  # scripted group (container) (typed FeaturePython)
  n = 2
  ref = Cl_element
FEATURE [App::DocumentObjectGroupPython] G4_POLYVINYLIDENE_CHLORIDE  # scripted group (container) (typed FeaturePython)
  Dunit = g/cm3
  Dvalue = 1.7
  Group = -> [C_element093,H_element085,Cl_element020]
  conduct = 2
  density = 1
  expand = 3
  formula = G4_POLYVINYLIDENE_CHLORIDE
  name = G4_POLYVINYLIDENE_CHLORIDE
  specific = 4
FEATURE [App::DocumentObjectGroupPython] C_element094  label="C_element : 052"  # scripted group (container) (typed FeaturePython)
  n = 2
  ref = C_element
FEATURE [App::DocumentObjectGroupPython] H_element086  label="H_element : 048"  # scripted group (container) (typed FeaturePython)
  n = 2
  ref = H_element
FEATURE [App::DocumentObjectGroupPython] F_element016  label="F_element : 007"  # scripted group (container) (typed FeaturePython)
  n = 2
  ref = F_element
FEATURE [App::DocumentObjectGroupPython] G4_POLYVINYLIDENE_FLUORIDE  # scripted group (container) (typed FeaturePython)
  Dunit = g/cm3
  Dvalue = 1.76
  Group = -> [C_element094,H_element086,F_element016]
  conduct = 2
  density = 1
  expand = 3
  formula = G4_POLYVINYLIDENE_FLUORIDE
  name = G4_POLYVINYLIDENE_FLUORIDE
  specific = 4
FEATURE [App::DocumentObjectGroupPython] C_element095  label="C_element : 053"  # scripted group (container) (typed FeaturePython)
  n = 6
  ref = C_element
FEATURE [App::DocumentObjectGroupPython] H_element087  label="H_element : 9"  # scripted group (container) (typed FeaturePython)
  n = 9
  ref = H_element
FEATURE [App::DocumentObjectGroupPython] N_element037  label="N_element : 016"  # scripted group (container) (typed FeaturePython)
  n = 1
  ref = N_element
FEATURE [App::DocumentObjectGroupPython] O_element084  label="O_element : 045"  # scripted group (container) (typed FeaturePython)
  n = 1
  ref = O_element
FEATURE [App::DocumentObjectGroupPython] G4_POLYVINYL_PYRROLIDONE  # scripted group (container) (typed FeaturePython)
  Dunit = g/cm3
  Dvalue = 1.25
  Group = -> [C_element095,H_element087,N_element037,O_element084]
  conduct = 2
  density = 1
  expand = 3
  formula = G4_POLYVINYL_PYRROLIDONE
  name = G4_POLYVINYL_PYRROLIDONE
  specific = 4
FEATURE [App::DocumentObjectGroupPython] K_element008  label="K_element : 1"  # scripted group (container) (typed FeaturePython)
  n = 1
  ref = K_element
FEATURE [App::DocumentObjectGroupPython] I_element006  label="I_element : 003"  # scripted group (container) (typed FeaturePython)
  n = 1
  ref = I_element
FEATURE [App::DocumentObjectGroupPython] G4_POTASSIUM_IODIDE  # scripted group (container) (typed FeaturePython)
  Dunit = g/cm3
  Dvalue = 3.13
  Group = -> [K_element008,I_element006]
  conduct = 2
  density = 1
  expand = 3
  formula = G4_POTASSIUM_IODIDE
  name = G4_POTASSIUM_IODIDE
  specific = 4
FEATURE [App::DocumentObjectGroupPython] K_element009  label="K_element : 2"  # scripted group (container) (typed FeaturePython)
  n = 2
  ref = K_element
FEATURE [App::DocumentObjectGroupPython] O_element085  label="O_element : 046"  # scripted group (container) (typed FeaturePython)
  n = 1
  ref = O_element
FEATURE [App::DocumentObjectGroupPython] G4_POTASSIUM_OXIDE  # scripted group (container) (typed FeaturePython)
  Dunit = g/cm3
  Dvalue = 2.32
  Group = -> [K_element009,O_element085]
  conduct = 2
  density = 1
  expand = 3
  formula = G4_POTASSIUM_OXIDE
  name = G4_POTASSIUM_OXIDE
  specific = 4
FEATURE [App::DocumentObjectGroupPython] C_element096  label="C_element : 054"  # scripted group (container) (typed FeaturePython)
  n = 3
  ref = C_element
FEATURE [App::DocumentObjectGroupPython] H_element088  label="H_element : 049"  # scripted group (container) (typed FeaturePython)
  n = 8
  ref = H_element
FEATURE [App::DocumentObjectGroupPython] G4_PROPANE  # scripted group (container) (typed FeaturePython)
  Dunit = g/cm3
  Dvalue = 0.00187939
  Group = -> [C_element096,H_element088]
  conduct = 2
  density = 1
  expand = 3
  formula = G4_PROPANE
  name = G4_PROPANE
  specific = 4
FEATURE [App::DocumentObjectGroupPython] C_element097  label="C_element : 055"  # scripted group (container) (typed FeaturePython)
  n = 3
  ref = C_element
FEATURE [App::DocumentObjectGroupPython] H_element089  label="H_element : 050"  # scripted group (container) (typed FeaturePython)
  n = 8
  ref = H_element
FEATURE [App::DocumentObjectGroupPython] G4_lPROPANE  # scripted group (container) (typed FeaturePython)
  Dunit = g/cm3
  Dvalue = 0.43
  Group = -> [C_element097,H_element089]
  conduct = 2
  density = 1
  expand = 3
  formula = G4_lPROPANE
  name = G4_lPROPANE
  specific = 4
FEATURE [App::DocumentObjectGroupPython] C_element098  label="C_element : 056"  # scripted group (container) (typed FeaturePython)
  n = 3
  ref = C_element
FEATURE [App::DocumentObjectGroupPython] H_element090  label="H_element : 051"  # scripted group (container) (typed FeaturePython)
  n = 8
  ref = H_element
FEATURE [App::DocumentObjectGroupPython] O_element086  label="O_element : 047"  # scripted group (container) (typed FeaturePython)
  n = 1
  ref = O_element
FEATURE [App::DocumentObjectGroupPython] G4_N_PROPYL_ALCOHOL  label="G4_N-PROPYL_ALCOHOL"  # scripted group (container) (typed FeaturePython)
  Dunit = g/cm3
  Dvalue = 0.8035
  Group = -> [C_element098,H_element090,O_element086]
  conduct = 2
  density = 1
  expand = 3
  formula = G4_N-PROPYL_ALCOHOL
  name = G4_N-PROPYL_ALCOHOL
  specific = 4
FEATURE [App::DocumentObjectGroupPython] C_element099  label="C_element : 057"  # scripted group (container) (typed FeaturePython)
  n = 5
  ref = C_element
FEATURE [App::DocumentObjectGroupPython] H_element091  label="H_element : 052"  # scripted group (container) (typed FeaturePython)
  n = 5
  ref = H_element
FEATURE [App::DocumentObjectGroupPython] N_element038  label="N_element : 017"  # scripted group (container) (typed FeaturePython)
  n = 1
  ref = N_element
FEATURE [App::DocumentObjectGroupPython] G4_PYRIDINE  # scripted group (container) (typed FeaturePython)
  Dunit = g/cm3
  Dvalue = 0.9819
  Group = -> [C_element099,H_element091,N_element038]
  conduct = 2
  density = 1
  expand = 3
  formula = G4_PYRIDINE
  name = G4_PYRIDINE
  specific = 4
FEATURE [App::DocumentObjectGroupPython] H_element092  label="H_element : 0.144"  # scripted group (container) (typed FeaturePython)
  n = 0.143711
FEATURE [App::DocumentObjectGroupPython] C_element100  label="C_element : 0.856"  # scripted group (container) (typed FeaturePython)
  n = 0.856289
FEATURE [App::DocumentObjectGroupPython] G4_RUBBER_BUTYL  # scripted group (container) (typed FeaturePython)
  Dunit = g/cm3
  Dvalue = 0.92
  Group = -> [H_element092,C_element100]
  conduct = 2
  density = 1
  expand = 3
  formula = G4_RUBBER_BUTYL
  name = G4_RUBBER_BUTYL
  specific = 4
FEATURE [App::DocumentObjectGroupPython] H_element093  label="H_element : 0.118"  # scripted group (container) (typed FeaturePython)
  n = 0.118371
FEATURE [App::DocumentObjectGroupPython] C_element101  label="C_element : 0.882"  # scripted group (container) (typed FeaturePython)
  n = 0.881629
FEATURE [App::DocumentObjectGroupPython] G4_RUBBER_NATURAL  # scripted group (container) (typed FeaturePython)
  Dunit = g/cm3
  Dvalue = 0.92
  Group = -> [H_element093,C_element101]
  conduct = 2
  density = 1
  expand = 3
  formula = G4_RUBBER_NATURAL
  name = G4_RUBBER_NATURAL
  specific = 4
FEATURE [App::DocumentObjectGroupPython] H_element094  label="H_element : 0.145"  # scripted group (container) (typed FeaturePython)
  n = 0.05692
FEATURE [App::DocumentObjectGroupPython] C_element102  label="C_element : 0.543"  # scripted group (container) (typed FeaturePython)
  n = 0.542646
FEATURE [App::DocumentObjectGroupPython] Cl_element021  label="Cl_element : 0.400"  # scripted group (container) (typed FeaturePython)
  n = 0.400434
FEATURE [App::DocumentObjectGroupPython] G4_RUBBER_NEOPRENE  # scripted group (container) (typed FeaturePython)
  Dunit = g/cm3
  Dvalue = 1.23
  Group = -> [H_element094,C_element102,Cl_element021]
  conduct = 2
  density = 1
  expand = 3
  formula = G4_RUBBER_NEOPRENE
  name = G4_RUBBER_NEOPRENE
  specific = 4
FEATURE [App::DocumentObjectGroupPython] Si_element006  label="Si_element : 1"  # scripted group (container) (typed FeaturePython)
  n = 1
  ref = Si_element
FEATURE [App::DocumentObjectGroupPython] O_element087  label="O_element : 048"  # scripted group (container) (typed FeaturePython)
  n = 2
  ref = O_element
FEATURE [App::DocumentObjectGroupPython] G4_SILICON_DIOXIDE  # scripted group (container) (typed FeaturePython)
  Dunit = g/cm3
  Dvalue = 2.32
  Group = -> [Si_element006,O_element087]
  conduct = 2
  density = 1
  expand = 3
  formula = G4_SILICON_DIOXIDE
  name = G4_SILICON_DIOXIDE
  specific = 4
FEATURE [App::DocumentObjectGroupPython] Ag_element002  label="Ag_element : 1"  # scripted group (container) (typed FeaturePython)
  n = 1
  ref = Ag_element
FEATURE [App::DocumentObjectGroupPython] Br_element005  label="Br_element : 003"  # scripted group (container) (typed FeaturePython)
  n = 1
  ref = Br_element
FEATURE [App::DocumentObjectGroupPython] G4_SILVER_BROMIDE  # scripted group (container) (typed FeaturePython)
  Dunit = g/cm3
  Dvalue = 6.473
  Group = -> [Ag_element002,Br_element005]
  conduct = 2
  density = 1
  expand = 3
  formula = G4_SILVER_BROMIDE
  name = G4_SILVER_BROMIDE
  specific = 4
FEATURE [App::DocumentObjectGroupPython] Ag_element003  label="Ag_element : 002"  # scripted group (container) (typed FeaturePython)
  n = 1
  ref = Ag_element
FEATURE [App::DocumentObjectGroupPython] Cl_element022  label="Cl_element : 011"  # scripted group (container) (typed FeaturePython)
  n = 1
  ref = Cl_element
FEATURE [App::DocumentObjectGroupPython] G4_SILVER_CHLORIDE  # scripted group (container) (typed FeaturePython)
  Dunit = g/cm3
  Dvalue = 5.56
  Group = -> [Ag_element003,Cl_element022]
  conduct = 2
  density = 1
  expand = 3
  formula = G4_SILVER_CHLORIDE
  name = G4_SILVER_CHLORIDE
  specific = 4
FEATURE [App::DocumentObjectGroupPython] Br_element006  label="Br_element : 0.423"  # scripted group (container) (typed FeaturePython)
  n = 0.422895
FEATURE [App::DocumentObjectGroupPython] Ag_element004  label="Ag_element : 0.574"  # scripted group (container) (typed FeaturePython)
  n = 0.573748
FEATURE [App::DocumentObjectGroupPython] I_element007  label="I_element : 0.649"  # scripted group (container) (typed FeaturePython)
  n = 0.003357
FEATURE [App::DocumentObjectGroupPython] G4_SILVER_HALIDES  # scripted group (container) (typed FeaturePython)
  Dunit = g/cm3
  Dvalue = 6.47
  Group = -> [Br_element006,Ag_element004,I_element007]
  conduct = 2
  density = 1
  expand = 3
  formula = G4_SILVER_HALIDES
  name = G4_SILVER_HALIDES
  specific = 4
FEATURE [App::DocumentObjectGroupPython] Ag_element005  label="Ag_element : 003"  # scripted group (container) (typed FeaturePython)
  n = 1
  ref = Ag_element
FEATURE [App::DocumentObjectGroupPython] I_element008  label="I_element : 004"  # scripted group (container) (typed FeaturePython)
  n = 1
  ref = I_element
FEATURE [App::DocumentObjectGroupPython] G4_SILVER_IODIDE  # scripted group (container) (typed FeaturePython)
  Dunit = g/cm3
  Dvalue = 6.01
  Group = -> [Ag_element005,I_element008]
  conduct = 2
  density = 1
  expand = 3
  formula = G4_SILVER_IODIDE
  name = G4_SILVER_IODIDE
  specific = 4
FEATURE [App::DocumentObjectGroupPython] H_element095  label="H_element : 0.100"  # scripted group (container) (typed FeaturePython)
  n = 0.1
FEATURE [App::DocumentObjectGroupPython] C_element103  label="C_element : 0.204"  # scripted group (container) (typed FeaturePython)
  n = 0.204
FEATURE [App::DocumentObjectGroupPython] N_element039  label="N_element : 0.759"  # scripted group (container) (typed FeaturePython)
  n = 0.042
FEATURE [App::DocumentObjectGroupPython] O_element088  label="O_element : 0.645"  # scripted group (container) (typed FeaturePython)
  n = 0.645
FEATURE [App::DocumentObjectGroupPython] Na_element013  label="Na_element : 0.100"  # scripted group (container) (typed FeaturePython)
  n = 0.002
FEATURE [App::DocumentObjectGroupPython] P_element009  label="P_element : 0.107"  # scripted group (container) (typed FeaturePython)
  n = 0.001
FEATURE [App::DocumentObjectGroupPython] S_element020  label="S_element : 0.021"  # scripted group (container) (typed FeaturePython)
  n = 0.002
FEATURE [App::DocumentObjectGroupPython] Cl_element023  label="Cl_element : 0.590"  # scripted group (container) (typed FeaturePython)
  n = 0.003
FEATURE [App::DocumentObjectGroupPython] K_element010  label="K_element : 0.001"  # scripted group (container) (typed FeaturePython)
  n = 0.001
FEATURE [App::DocumentObjectGroupPython] G4_SKIN_ICRP  # scripted group (container) (typed FeaturePython)
  Dunit = g/cm3
  Dvalue = 1.09
  Group = -> [H_element095,C_element103,N_element039,O_element088,Na_element013,P_element009,S_element020,Cl_element023,K_element010]
  conduct = 2
  density = 1
  expand = 3
  formula = G4_SKIN_ICRP
  name = G4_SKIN_ICRP
  specific = 4
FEATURE [App::DocumentObjectGroupPython] Na_element014  label="Na_element : 2"  # scripted group (container) (typed FeaturePython)
  n = 2
  ref = Na_element
FEATURE [App::DocumentObjectGroupPython] C_element104  label="C_element : 058"  # scripted group (container) (typed FeaturePython)
  n = 1
  ref = C_element
FEATURE [App::DocumentObjectGroupPython] O_element089  label="O_element : 049"  # scripted group (container) (typed FeaturePython)
  n = 3
  ref = O_element
FEATURE [App::DocumentObjectGroupPython] G4_SODIUM_CARBONATE  # scripted group (container) (typed FeaturePython)
  Dunit = g/cm3
  Dvalue = 2.532
  Group = -> [Na_element014,C_element104,O_element089]
  conduct = 2
  density = 1
  expand = 3
  formula = G4_SODIUM_CARBONATE
  name = G4_SODIUM_CARBONATE
  specific = 4
FEATURE [App::DocumentObjectGroupPython] Na_element015  label="Na_element : 1"  # scripted group (container) (typed FeaturePython)
  n = 1
  ref = Na_element
FEATURE [App::DocumentObjectGroupPython] I_element009  label="I_element : 005"  # scripted group (container) (typed FeaturePython)
  n = 1
  ref = I_element
FEATURE [App::DocumentObjectGroupPython] G4_SODIUM_IODIDE  # scripted group (container) (typed FeaturePython)
  Dunit = g/cm3
  Dvalue = 3.667
  Group = -> [Na_element015,I_element009]
  conduct = 2
  density = 1
  expand = 3
  formula = G4_SODIUM_IODIDE
  name = G4_SODIUM_IODIDE
  specific = 4
FEATURE [App::DocumentObjectGroupPython] Na_element016  label="Na_element : 003"  # scripted group (container) (typed FeaturePython)
  n = 2
  ref = Na_element
FEATURE [App::DocumentObjectGroupPython] O_element090  label="O_element : 050"  # scripted group (container) (typed FeaturePython)
  n = 1
  ref = O_element
FEATURE [App::DocumentObjectGroupPython] G4_SODIUM_MONOXIDE  # scripted group (container) (typed FeaturePython)
  Dunit = g/cm3
  Dvalue = 2.27
  Group = -> [Na_element016,O_element090]
  conduct = 2
  density = 1
  expand = 3
  formula = G4_SODIUM_MONOXIDE
  name = G4_SODIUM_MONOXIDE
  specific = 4
FEATURE [App::DocumentObjectGroupPython] Na_element017  label="Na_element : 004"  # scripted group (container) (typed FeaturePython)
  n = 1
  ref = Na_element
FEATURE [App::DocumentObjectGroupPython] N_element040  label="N_element : 018"  # scripted group (container) (typed FeaturePython)
  n = 1
  ref = N_element
FEATURE [App::DocumentObjectGroupPython] O_element091  label="O_element : 051"  # scripted group (container) (typed FeaturePython)
  n = 3
  ref = O_element
FEATURE [App::DocumentObjectGroupPython] G4_SODIUM_NITRATE  # scripted group (container) (typed FeaturePython)
  Dunit = g/cm3
  Dvalue = 2.261
  Group = -> [Na_element017,N_element040,O_element091]
  conduct = 2
  density = 1
  expand = 3
  formula = G4_SODIUM_NITRATE
  name = G4_SODIUM_NITRATE
  specific = 4
FEATURE [App::DocumentObjectGroupPython] C_element105  label="C_element : 059"  # scripted group (container) (typed FeaturePython)
  n = 14
  ref = C_element
FEATURE [App::DocumentObjectGroupPython] H_element096  label="H_element : 053"  # scripted group (container) (typed FeaturePython)
  n = 12
  ref = H_element
FEATURE [App::DocumentObjectGroupPython] G4_STILBENE  # scripted group (container) (typed FeaturePython)
  Dunit = g/cm3
  Dvalue = 0.9707
  Group = -> [C_element105,H_element096]
  conduct = 2
  density = 1
  expand = 3
  formula = G4_STILBENE
  name = G4_STILBENE
  specific = 4
FEATURE [App::DocumentObjectGroupPython] C_element106  label="C_element : 12"  # scripted group (container) (typed FeaturePython)
  n = 12
  ref = C_element
FEATURE [App::DocumentObjectGroupPython] H_element097  label="H_element : 22"  # scripted group (container) (typed FeaturePython)
  n = 22
  ref = H_element
FEATURE [App::DocumentObjectGroupPython] O_element092  label="O_element : 11"  # scripted group (container) (typed FeaturePython)
  n = 11
  ref = O_element
FEATURE [App::DocumentObjectGroupPython] G4_SUCROSE  # scripted group (container) (typed FeaturePython)
  Dunit = g/cm3
  Dvalue = 1.5805
  Group = -> [C_element106,H_element097,O_element092]
  conduct = 2
  density = 1
  expand = 3
  formula = G4_SUCROSE
  name = G4_SUCROSE
  specific = 4
FEATURE [App::DocumentObjectGroupPython] C_element107  label="C_element : 18"  # scripted group (container) (typed FeaturePython)
  n = 18
  ref = C_element
FEATURE [App::DocumentObjectGroupPython] H_element098  label="H_element : 054"  # scripted group (container) (typed FeaturePython)
  n = 14
  ref = H_element
FEATURE [App::DocumentObjectGroupPython] G4_TERPHENYL  # scripted group (container) (typed FeaturePython)
  Dunit = g/cm3
  Dvalue = 1.24
  Group = -> [C_element107,H_element098]
  conduct = 2
  density = 1
  expand = 3
  formula = G4_TERPHENYL
  name = G4_TERPHENYL
  specific = 4
FEATURE [App::DocumentObjectGroupPython] H_element099  label="H_element : 0.146"  # scripted group (container) (typed FeaturePython)
  n = 0.106
FEATURE [App::DocumentObjectGroupPython] C_element108  label="C_element : 0.883"  # scripted group (container) (typed FeaturePython)
  n = 0.099
FEATURE [App::DocumentObjectGroupPython] N_element041  label="N_element : 0.020"  # scripted group (container) (typed FeaturePython)
  n = 0.02
FEATURE [App::DocumentObjectGroupPython] O_element093  label="O_element : 0.766"  # scripted group (container) (typed FeaturePython)
  n = 0.766
FEATURE [App::DocumentObjectGroupPython] Na_element018  label="Na_element : 0.101"  # scripted group (container) (typed FeaturePython)
  n = 0.002
FEATURE [App::DocumentObjectGroupPython] P_element010  label="P_element : 0.108"  # scripted group (container) (typed FeaturePython)
  n = 0.001
FEATURE [App::DocumentObjectGroupPython] S_element021  label="S_element : 0.022"  # scripted group (container) (typed FeaturePython)
  n = 0.002
FEATURE [App::DocumentObjectGroupPython] Cl_element024  label="Cl_element : 0.002"  # scripted group (container) (typed FeaturePython)
  n = 0.002
FEATURE [App::DocumentObjectGroupPython] K_element011  label="K_element : 0.017"  # scripted group (container) (typed FeaturePython)
  n = 0.002
FEATURE [App::DocumentObjectGroupPython] G4_TESTIS_ICRP  # scripted group (container) (typed FeaturePython)
  Dunit = g/cm3
  Dvalue = 1.04
  Group = -> [H_element099,C_element108,N_element041,O_element093,Na_element018,P_element010,S_element021,Cl_element024,K_element011]
  conduct = 2
  density = 1
  expand = 3
  formula = G4_TESTIS_ICRP
  name = G4_TESTIS_ICRP
  specific = 4
FEATURE [App::DocumentObjectGroupPython] C_element109  label="C_element : 060"  # scripted group (container) (typed FeaturePython)
  n = 2
  ref = C_element
FEATURE [App::DocumentObjectGroupPython] Cl_element025  label="Cl_element : 012"  # scripted group (container) (typed FeaturePython)
  n = 4
  ref = Cl_element
FEATURE [App::DocumentObjectGroupPython] G4_TETRACHLOROETHYLENE  # scripted group (container) (typed FeaturePython)
  Dunit = g/cm3
  Dvalue = 1.625
  Group = -> [C_element109,Cl_element025]
  conduct = 2
  density = 1
  expand = 3
  formula = G4_TETRACHLOROETHYLENE
  name = G4_TETRACHLOROETHYLENE
  specific = 4
FEATURE [App::DocumentObjectGroupPython] Tl_element001  label="Tl_element : 1"  # scripted group (container) (typed FeaturePython)
  n = 1
  ref = Tl_element
FEATURE [App::DocumentObjectGroupPython] Cl_element026  label="Cl_element : 013"  # scripted group (container) (typed FeaturePython)
  n = 1
  ref = Cl_element
FEATURE [App::DocumentObjectGroupPython] G4_THALLIUM_CHLORIDE  # scripted group (container) (typed FeaturePython)
  Dunit = g/cm3
  Dvalue = 7.004
  Group = -> [Tl_element001,Cl_element026]
  conduct = 2
  density = 1
  expand = 3
  formula = G4_THALLIUM_CHLORIDE
  name = G4_THALLIUM_CHLORIDE
  specific = 4
FEATURE [App::DocumentObjectGroupPython] H_element100  label="H_element : 0.147"  # scripted group (container) (typed FeaturePython)
  n = 0.105
FEATURE [App::DocumentObjectGroupPython] C_element110  label="C_element : 0.256"  # scripted group (container) (typed FeaturePython)
  n = 0.256
FEATURE [App::DocumentObjectGroupPython] N_element042  label="N_element : 0.760"  # scripted group (container) (typed FeaturePython)
  n = 0.027
FEATURE [App::DocumentObjectGroupPython] O_element094  label="O_element : 0.602"  # scripted group (container) (typed FeaturePython)
  n = 0.602
FEATURE [App::DocumentObjectGroupPython] Na_element019  label="Na_element : 0.102"  # scripted group (container) (typed FeaturePython)
  n = 0.001
FEATURE [App::DocumentObjectGroupPython] P_element011  label="P_element : 0.109"  # scripted group (container) (typed FeaturePython)
  n = 0.002
FEATURE [App::DocumentObjectGroupPython] S_element022  label="S_element : 0.023"  # scripted group (container) (typed FeaturePython)
  n = 0.003
FEATURE [App::DocumentObjectGroupPython] Cl_element027  label="Cl_element : 0.591"  # scripted group (container) (typed FeaturePython)
  n = 0.002
FEATURE [App::DocumentObjectGroupPython] K_element012  label="K_element : 0.018"  # scripted group (container) (typed FeaturePython)
  n = 0.002
FEATURE [App::DocumentObjectGroupPython] G4_TISSUE_SOFT_ICRP  # scripted group (container) (typed FeaturePython)
  Dunit = g/cm3
  Dvalue = 1.03
  Group = -> [H_element100,C_element110,N_element042,O_element094,Na_element019,P_element011,S_element022,Cl_element027,K_element012]
  conduct = 2
  density = 1
  expand = 3
  formula = G4_TISSUE_SOFT_ICRP
  name = G4_TISSUE_SOFT_ICRP
  specific = 4
FEATURE [App::DocumentObjectGroupPython] H_element101  label="H_element : 0.148"  # scripted group (container) (typed FeaturePython)
  n = 0.101
FEATURE [App::DocumentObjectGroupPython] C_element111  label="C_element : 0.111"  # scripted group (container) (typed FeaturePython)
  n = 0.111
FEATURE [App::DocumentObjectGroupPython] N_element043  label="N_element : 0.026"  # scripted group (container) (typed FeaturePython)
  n = 0.026
FEATURE [App::DocumentObjectGroupPython] O_element095  label="O_element : 0.762"  # scripted group (container) (typed FeaturePython)
  n = 0.762
FEATURE [App::DocumentObjectGroupPython] G4_TISSUE_SOFT_ICRU_4  label="G4_TISSUE_SOFT_ICRU-4"  # scripted group (container) (typed FeaturePython)
  Dunit = g/cm3
  Dvalue = 1
  Group = -> [H_element101,C_element111,N_element043,O_element095]
  conduct = 2
  density = 1
  expand = 3
  formula = G4_TISSUE_SOFT_ICRU-4
  name = G4_TISSUE_SOFT_ICRU-4
  specific = 4
FEATURE [App::DocumentObjectGroupPython] H_element102  label="H_element : 0.149"  # scripted group (container) (typed FeaturePython)
  n = 0.101869
FEATURE [App::DocumentObjectGroupPython] C_element112  label="C_element : 0.456"  # scripted group (container) (typed FeaturePython)
  n = 0.456179
FEATURE [App::DocumentObjectGroupPython] N_element044  label="N_element : 0.761"  # scripted group (container) (typed FeaturePython)
  n = 0.035172
FEATURE [App::DocumentObjectGroupPython] O_element096  label="O_element : 0.407"  # scripted group (container) (typed FeaturePython)
  n = 0.40678
FEATURE [App::DocumentObjectGroupPython] G4_TISSUE_METHANE  label="G4_TISSUE-METHANE"  # scripted group (container) (typed FeaturePython)
  Dunit = g/cm3
  Dvalue = 0.00106409
  Group = -> [H_element102,C_element112,N_element044,O_element096]
  conduct = 2
  density = 1
  expand = 3
  formula = G4_TISSUE-METHANE
  name = G4_TISSUE-METHANE
  specific = 4
FEATURE [App::DocumentObjectGroupPython] H_element103  label="H_element : 0.103"  # scripted group (container) (typed FeaturePython)
  n = 0.102672
FEATURE [App::DocumentObjectGroupPython] C_element113  label="C_element : 0.569"  # scripted group (container) (typed FeaturePython)
  n = 0.56894
FEATURE [App::DocumentObjectGroupPython] N_element045  label="N_element : 0.762"  # scripted group (container) (typed FeaturePython)
  n = 0.035022
FEATURE [App::DocumentObjectGroupPython] O_element097  label="O_element : 0.293"  # scripted group (container) (typed FeaturePython)
  n = 0.293366
FEATURE [App::DocumentObjectGroupPython] G4_TISSUE_PROPANE  label="G4_TISSUE-PROPANE"  # scripted group (container) (typed FeaturePython)
  Dunit = g/cm3
  Dvalue = 0.00182628
  Group = -> [H_element103,C_element113,N_element045,O_element097]
  conduct = 2
  density = 1
  expand = 3
  formula = G4_TISSUE-PROPANE
  name = G4_TISSUE-PROPANE
  specific = 4
FEATURE [App::DocumentObjectGroupPython] Ti_element003  label="Ti_element : 1"  # scripted group (container) (typed FeaturePython)
  n = 1
  ref = Ti_element
FEATURE [App::DocumentObjectGroupPython] O_element098  label="O_element : 052"  # scripted group (container) (typed FeaturePython)
  n = 2
  ref = O_element
FEATURE [App::DocumentObjectGroupPython] G4_TITANIUM_DIOXIDE  # scripted group (container) (typed FeaturePython)
  Dunit = g/cm3
  Dvalue = 4.26
  Group = -> [Ti_element003,O_element098]
  conduct = 2
  density = 1
  expand = 3
  formula = G4_TITANIUM_DIOXIDE
  name = G4_TITANIUM_DIOXIDE
  specific = 4
FEATURE [App::DocumentObjectGroupPython] C_element114  label="C_element : 061"  # scripted group (container) (typed FeaturePython)
  n = 7
  ref = C_element
FEATURE [App::DocumentObjectGroupPython] H_element104  label="H_element : 055"  # scripted group (container) (typed FeaturePython)
  n = 8
  ref = H_element
FEATURE [App::DocumentObjectGroupPython] G4_TOLUENE  # scripted group (container) (typed FeaturePython)
  Dunit = g/cm3
  Dvalue = 0.8669
  Group = -> [C_element114,H_element104]
  conduct = 2
  density = 1
  expand = 3
  formula = G4_TOLUENE
  name = G4_TOLUENE
  specific = 4
FEATURE [App::DocumentObjectGroupPython] C_element115  label="C_element : 062"  # scripted group (container) (typed FeaturePython)
  n = 2
  ref = C_element
FEATURE [App::DocumentObjectGroupPython] H_element105  label="H_element : 056"  # scripted group (container) (typed FeaturePython)
  n = 1
  ref = H_element
FEATURE [App::DocumentObjectGroupPython] Cl_element028  label="Cl_element : 014"  # scripted group (container) (typed FeaturePython)
  n = 3
  ref = Cl_element
FEATURE [App::DocumentObjectGroupPython] G4_TRICHLOROETHYLENE  # scripted group (container) (typed FeaturePython)
  Dunit = g/cm3
  Dvalue = 1.46
  Group = -> [C_element115,H_element105,Cl_element028]
  conduct = 2
  density = 1
  expand = 3
  formula = G4_TRICHLOROETHYLENE
  name = G4_TRICHLOROETHYLENE
  specific = 4
FEATURE [App::DocumentObjectGroupPython] C_element116  label="C_element : 063"  # scripted group (container) (typed FeaturePython)
  n = 6
  ref = C_element
FEATURE [App::DocumentObjectGroupPython] H_element106  label="H_element : 15"  # scripted group (container) (typed FeaturePython)
  n = 15
  ref = H_element
FEATURE [App::DocumentObjectGroupPython] O_element099  label="O_element : 053"  # scripted group (container) (typed FeaturePython)
  n = 4
  ref = O_element
FEATURE [App::DocumentObjectGroupPython] P_element012  label="P_element : 1"  # scripted group (container) (typed FeaturePython)
  n = 1
  ref = P_element
FEATURE [App::DocumentObjectGroupPython] G4_TRIETHYL_PHOSPHATE  # scripted group (container) (typed FeaturePython)
  Dunit = g/cm3
  Dvalue = 1.07
  Group = -> [C_element116,H_element106,O_element099,P_element012]
  conduct = 2
  density = 1
  expand = 3
  formula = G4_TRIETHYL_PHOSPHATE
  name = G4_TRIETHYL_PHOSPHATE
  specific = 4
FEATURE [App::DocumentObjectGroupPython] W_element003  label="W_element : 003"  # scripted group (container) (typed FeaturePython)
  n = 1
  ref = W_element
FEATURE [App::DocumentObjectGroupPython] F_element017  label="F_element : 6"  # scripted group (container) (typed FeaturePython)
  n = 6
  ref = F_element
FEATURE [App::DocumentObjectGroupPython] G4_TUNGSTEN_HEXAFLUORIDE  # scripted group (container) (typed FeaturePython)
  Dunit = g/cm3
  Dvalue = 2.4
  Group = -> [W_element003,F_element017]
  conduct = 2
  density = 1
  expand = 3
  formula = G4_TUNGSTEN_HEXAFLUORIDE
  name = G4_TUNGSTEN_HEXAFLUORIDE
  specific = 4
FEATURE [App::DocumentObjectGroupPython] U_element001  label="U_element : 1"  # scripted group (container) (typed FeaturePython)
  n = 1
  ref = U_element
FEATURE [App::DocumentObjectGroupPython] C_element117  label="C_element : 064"  # scripted group (container) (typed FeaturePython)
  n = 2
  ref = C_element
FEATURE [App::DocumentObjectGroupPython] G4_URANIUM_DICARBIDE  # scripted group (container) (typed FeaturePython)
  Dunit = g/cm3
  Dvalue = 11.28
  Group = -> [U_element001,C_element117]
  conduct = 2
  density = 1
  expand = 3
  formula = G4_URANIUM_DICARBIDE
  name = G4_URANIUM_DICARBIDE
  specific = 4
FEATURE [App::DocumentObjectGroupPython] U_element002  label="U_element : 002"  # scripted group (container) (typed FeaturePython)
  n = 1
  ref = U_element
FEATURE [App::DocumentObjectGroupPython] C_element118  label="C_element : 065"  # scripted group (container) (typed FeaturePython)
  n = 1
  ref = C_element
FEATURE [App::DocumentObjectGroupPython] G4_URANIUM_MONOCARBIDE  # scripted group (container) (typed FeaturePython)
  Dunit = g/cm3
  Dvalue = 13.63
  Group = -> [U_element002,C_element118]
  conduct = 2
  density = 1
  expand = 3
  formula = G4_URANIUM_MONOCARBIDE
  name = G4_URANIUM_MONOCARBIDE
  specific = 4
FEATURE [App::DocumentObjectGroupPython] U_element003  label="U_element : 003"  # scripted group (container) (typed FeaturePython)
  n = 1
  ref = U_element
FEATURE [App::DocumentObjectGroupPython] O_element100  label="O_element : 054"  # scripted group (container) (typed FeaturePython)
  n = 2
  ref = O_element
FEATURE [App::DocumentObjectGroupPython] G4_URANIUM_OXIDE  # scripted group (container) (typed FeaturePython)
  Dunit = g/cm3
  Dvalue = 10.96
  Group = -> [U_element003,O_element100]
  conduct = 2
  density = 1
  expand = 3
  formula = G4_URANIUM_OXIDE
  name = G4_URANIUM_OXIDE
  specific = 4
FEATURE [App::DocumentObjectGroupPython] C_element119  label="C_element : 066"  # scripted group (container) (typed FeaturePython)
  n = 1
  ref = C_element
FEATURE [App::DocumentObjectGroupPython] H_element107  label="H_element : 057"  # scripted group (container) (typed FeaturePython)
  n = 4
  ref = H_element
FEATURE [App::DocumentObjectGroupPython] N_element046  label="N_element : 019"  # scripted group (container) (typed FeaturePython)
  n = 2
  ref = N_element
FEATURE [App::DocumentObjectGroupPython] O_element101  label="O_element : 055"  # scripted group (container) (typed FeaturePython)
  n = 1
  ref = O_element
FEATURE [App::DocumentObjectGroupPython] G4_UREA  # scripted group (container) (typed FeaturePython)
  Dunit = g/cm3
  Dvalue = 1.323
  Group = -> [C_element119,H_element107,N_element046,O_element101]
  conduct = 2
  density = 1
  expand = 3
  formula = G4_UREA
  name = G4_UREA
  specific = 4
FEATURE [App::DocumentObjectGroupPython] C_element120  label="C_element : 067"  # scripted group (container) (typed FeaturePython)
  n = 5
  ref = C_element
FEATURE [App::DocumentObjectGroupPython] H_element108  label="H_element : 058"  # scripted group (container) (typed FeaturePython)
  n = 11
  ref = H_element
FEATURE [App::DocumentObjectGroupPython] N_element047  label="N_element : 020"  # scripted group (container) (typed FeaturePython)
  n = 1
  ref = N_element
FEATURE [App::DocumentObjectGroupPython] O_element102  label="O_element : 056"  # scripted group (container) (typed FeaturePython)
  n = 2
  ref = O_element
FEATURE [App::DocumentObjectGroupPython] G4_VALINE  # scripted group (container) (typed FeaturePython)
  Dunit = g/cm3
  Dvalue = 1.23
  Group = -> [C_element120,H_element108,N_element047,O_element102]
  conduct = 2
  density = 1
  expand = 3
  formula = G4_VALINE
  name = G4_VALINE
  specific = 4
FEATURE [App::DocumentObjectGroupPython] H_element109  label="H_element : 0.009"  # scripted group (container) (typed FeaturePython)
  n = 0.009417
FEATURE [App::DocumentObjectGroupPython] C_element121  label="C_element : 0.281"  # scripted group (container) (typed FeaturePython)
  n = 0.280555
FEATURE [App::DocumentObjectGroupPython] F_element018  label="F_element : 0.710"  # scripted group (container) (typed FeaturePython)
  n = 0.710028
FEATURE [App::DocumentObjectGroupPython] G4_VITON  # scripted group (container) (typed FeaturePython)
  Dunit = g/cm3
  Dvalue = 1.8
  Group = -> [H_element109,C_element121,F_element018]
  conduct = 2
  density = 1
  expand = 3
  formula = G4_VITON
  name = G4_VITON
  specific = 4
FEATURE [App::DocumentObjectGroupPython] H_element110  label="H_element : 059"  # scripted group (container) (typed FeaturePython)
  n = 2
  ref = H_element
FEATURE [App::DocumentObjectGroupPython] O_element103  label="O_element : 057"  # scripted group (container) (typed FeaturePython)
  n = 1
  ref = O_element
FEATURE [App::DocumentObjectGroupPython] G4_WATER  # scripted group (container) (typed FeaturePython)
  Dunit = g/cm3
  Dvalue = 1
  Group = -> [H_element110,O_element103]
  conduct = 2
  density = 1
  expand = 3
  formula = G4_WATER
  name = G4_WATER
  specific = 4
FEATURE [App::DocumentObjectGroupPython] H_element111  label="H_element : 060"  # scripted group (container) (typed FeaturePython)
  n = 2
  ref = H_element
FEATURE [App::DocumentObjectGroupPython] O_element104  label="O_element : 058"  # scripted group (container) (typed FeaturePython)
  n = 1
  ref = O_element
FEATURE [App::DocumentObjectGroupPython] G4_WATER_VAPOR  # scripted group (container) (typed FeaturePython)
  Dunit = g/cm3
  Dvalue = 0.000756182
  Group = -> [H_element111,O_element104]
  conduct = 2
  density = 1
  expand = 3
  formula = G4_WATER_VAPOR
  name = G4_WATER_VAPOR
  specific = 4
FEATURE [App::DocumentObjectGroupPython] C_element122  label="C_element : 068"  # scripted group (container) (typed FeaturePython)
  n = 8
  ref = C_element
FEATURE [App::DocumentObjectGroupPython] H_element112  label="H_element : 061"  # scripted group (container) (typed FeaturePython)
  n = 10
  ref = H_element
FEATURE [App::DocumentObjectGroupPython] G4_XYLENE  # scripted group (container) (typed FeaturePython)
  Dunit = g/cm3
  Dvalue = 0.87
  Group = -> [C_element122,H_element112]
  conduct = 2
  density = 1
  expand = 3
  formula = G4_XYLENE
  name = G4_XYLENE
  specific = 4
FEATURE [App::DocumentObjectGroupPython] C_element123  label="C_element : 069"  # scripted group (container) (typed FeaturePython)
  n = 1
  ref = C_element
FEATURE [App::DocumentObjectGroupPython] G4_GRAPHITE  # scripted group (container) (typed FeaturePython)
  Dunit = g/cm3
  Dvalue = 2.21
  Group = -> [C_element123]
  conduct = 2
  density = 1
  expand = 3
  formula = G4_GRAPHITE
  name = G4_GRAPHITE
  specific = 4
FEATURE [App::DocumentObjectGroupPython] NIST  # scripted group (container) (typed FeaturePython)
  Group = -> [G4_A_150_TISSUE,G4_ACETONE,G4_ACETYLENE,G4_ADENINE,G4_ADIPOSE_TISSUE_ICRP,G4_AIR,G4_ALANINE,G4_ALUMINUM_OXIDE,G4_AMBER,G4_AMMONIA,G4_ANILINE,G4_ANTHRACENE,G4_B_100_BONE,G4_BAKELITE,G4_BARIUM_FLUORIDE,G4_BARIUM_SULFATE,G4_BENZENE,G4_BERYLLIUM_OXIDE,G4_BGO,G4_BLOOD_ICRP,G4_BONE_COMPACT_ICRU,G4_BONE_CORTICAL_ICRP,G4_BORON_CARBIDE,G4_BORON_OXIDE,G4_BRAIN_ICRP,G4_BUTANE,G4_N_BUTYL_ALCOHOL,G4_C_552,+152 more]
FEATURE [App::DocumentObjectGroupPython] H_element113  label="H_element : 062"  # scripted group (container) (typed FeaturePython)
  n = 1
  ref = H_element
FEATURE [App::DocumentObjectGroupPython] G4_H  # scripted group (container) (typed FeaturePython)
  Dunit = g/cm3
  Dvalue = 8.3748e-05
  Group = -> [H_element113]
  conduct = 2
  density = 1
  expand = 3
  formula = H
  name = G4_H
  specific = 4
FEATURE [App::DocumentObjectGroupPython] He_element001  label="He_element : 1"  # scripted group (container) (typed FeaturePython)
  n = 1
  ref = He_element
FEATURE [App::DocumentObjectGroupPython] G4_He  # scripted group (container) (typed FeaturePython)
  Dunit = g/cm3
  Dvalue = 0.000166322
  Group = -> [He_element001]
  conduct = 2
  density = 1
  expand = 3
  formula = He
  name = G4_He
  specific = 4
FEATURE [App::DocumentObjectGroupPython] Li_element008  label="Li_element : 008"  # scripted group (container) (typed FeaturePython)
  n = 1
  ref = Li_element
FEATURE [App::DocumentObjectGroupPython] G4_Li  # scripted group (container) (typed FeaturePython)
  Dunit = g/cm3
  Dvalue = 0.534
  Group = -> [Li_element008]
  conduct = 2
  density = 1
  expand = 3
  formula = Li
  name = G4_Li
  specific = 4
FEATURE [App::DocumentObjectGroupPython] Be_element002  label="Be_element : 002"  # scripted group (container) (typed FeaturePython)
  n = 1
  ref = Be_element
FEATURE [App::DocumentObjectGroupPython] G4_Be  # scripted group (container) (typed FeaturePython)
  Dunit = g/cm3
  Dvalue = 1.848
  Group = -> [Be_element002]
  conduct = 2
  density = 1
  expand = 3
  formula = Be
  name = G4_Be
  specific = 4
FEATURE [App::DocumentObjectGroupPython] B_element007  label="B_element : 007"  # scripted group (container) (typed FeaturePython)
  n = 1
  ref = B_element
FEATURE [App::DocumentObjectGroupPython] G4_B  # scripted group (container) (typed FeaturePython)
  Dunit = g/cm3
  Dvalue = 2.37
  Group = -> [B_element007]
  conduct = 2
  density = 1
  expand = 3
  formula = B
  name = G4_B
  specific = 4
FEATURE [App::DocumentObjectGroupPython] C_element124  label="C_element : 070"  # scripted group (container) (typed FeaturePython)
  n = 1
  ref = C_element
FEATURE [App::DocumentObjectGroupPython] G4_C  # scripted group (container) (typed FeaturePython)
  Dunit = g/cm3
  Dvalue = 2
  Group = -> [C_element124]
  conduct = 2
  density = 1
  expand = 3
  formula = C
  name = G4_C
  specific = 4
FEATURE [App::DocumentObjectGroupPython] N_element048  label="N_element : 021"  # scripted group (container) (typed FeaturePython)
  n = 1
  ref = N_element
FEATURE [App::DocumentObjectGroupPython] G4_N  # scripted group (container) (typed FeaturePython)
  Dunit = g/cm3
  Dvalue = 0.0011652
  Group = -> [N_element048]
  conduct = 2
  density = 1
  expand = 3
  formula = N
  name = G4_N
  specific = 4
FEATURE [App::DocumentObjectGroupPython] O_element105  label="O_element : 059"  # scripted group (container) (typed FeaturePython)
  n = 1
  ref = O_element
FEATURE [App::DocumentObjectGroupPython] G4_O  # scripted group (container) (typed FeaturePython)
  Dunit = g/cm3
  Dvalue = 0.00133151
  Group = -> [O_element105]
  conduct = 2
  density = 1
  expand = 3
  formula = O
  name = G4_O
  specific = 4
FEATURE [App::DocumentObjectGroupPython] F_element019  label="F_element : 008"  # scripted group (container) (typed FeaturePython)
  n = 1
  ref = F_element
FEATURE [App::DocumentObjectGroupPython] G4_F  # scripted group (container) (typed FeaturePython)
  Dunit = g/cm3
  Dvalue = 0.00158029
  Group = -> [F_element019]
  conduct = 2
  density = 1
  expand = 3
  formula = F
  name = G4_F
  specific = 4
FEATURE [App::DocumentObjectGroupPython] Ne_element001  label="Ne_element : 1"  # scripted group (container) (typed FeaturePython)
  n = 1
  ref = Ne_element
FEATURE [App::DocumentObjectGroupPython] G4_Ne  # scripted group (container) (typed FeaturePython)
  Dunit = g/cm3
  Dvalue = 0.000838505
  Group = -> [Ne_element001]
  conduct = 2
  density = 1
  expand = 3
  formula = Ne
  name = G4_Ne
  specific = 4
FEATURE [App::DocumentObjectGroupPython] Na_element020  label="Na_element : 005"  # scripted group (container) (typed FeaturePython)
  n = 1
  ref = Na_element
FEATURE [App::DocumentObjectGroupPython] G4_Na  # scripted group (container) (typed FeaturePython)
  Dunit = g/cm3
  Dvalue = 0.971
  Group = -> [Na_element020]
  conduct = 2
  density = 1
  expand = 3
  formula = Na
  name = G4_Na
  specific = 4
FEATURE [App::DocumentObjectGroupPython] Mg_element011  label="Mg_element : 005"  # scripted group (container) (typed FeaturePython)
  n = 1
  ref = Mg_element
FEATURE [App::DocumentObjectGroupPython] G4_Mg  # scripted group (container) (typed FeaturePython)
  Dunit = g/cm3
  Dvalue = 1.74
  Group = -> [Mg_element011]
  conduct = 2
  density = 1
  expand = 3
  formula = Mg
  name = G4_Mg
  specific = 4
FEATURE [App::DocumentObjectGroupPython] Al_element004  label="Al_element : 1"  # scripted group (container) (typed FeaturePython)
  n = 1
  ref = Al_element
FEATURE [App::DocumentObjectGroupPython] G4_Al  # scripted group (container) (typed FeaturePython)
  Dunit = g/cm3
  Dvalue = 2.699
  Group = -> [Al_element004]
  conduct = 2
  density = 1
  expand = 3
  formula = Al
  name = G4_Al
  specific = 4
FEATURE [App::DocumentObjectGroupPython] Si_element007  label="Si_element : 002"  # scripted group (container) (typed FeaturePython)
  n = 1
  ref = Si_element
FEATURE [App::DocumentObjectGroupPython] G4_Si  # scripted group (container) (typed FeaturePython)
  Dunit = g/cm3
  Dvalue = 2.33
  Group = -> [Si_element007]
  conduct = 2
  density = 1
  expand = 3
  formula = Si
  name = G4_Si
  specific = 4
FEATURE [App::DocumentObjectGroupPython] P_element013  label="P_element : 002"  # scripted group (container) (typed FeaturePython)
  n = 1
  ref = P_element
FEATURE [App::DocumentObjectGroupPython] G4_P  # scripted group (container) (typed FeaturePython)
  Dunit = g/cm3
  Dvalue = 2.2
  Group = -> [P_element013]
  conduct = 2
  density = 1
  expand = 3
  formula = P
  name = G4_P
  specific = 4
FEATURE [App::DocumentObjectGroupPython] S_element023  label="S_element : 007"  # scripted group (container) (typed FeaturePython)
  n = 1
  ref = S_element
FEATURE [App::DocumentObjectGroupPython] G4_S  # scripted group (container) (typed FeaturePython)
  Dunit = g/cm3
  Dvalue = 2
  Group = -> [S_element023]
  conduct = 2
  density = 1
  expand = 3
  formula = S
  name = G4_S
  specific = 4
FEATURE [App::DocumentObjectGroupPython] Cl_element029  label="Cl_element : 015"  # scripted group (container) (typed FeaturePython)
  n = 1
  ref = Cl_element
FEATURE [App::DocumentObjectGroupPython] G4_Cl  # scripted group (container) (typed FeaturePython)
  Dunit = g/cm3
  Dvalue = 0.00299473
  Group = -> [Cl_element029]
  conduct = 2
  density = 1
  expand = 3
  formula = Cl
  name = G4_Cl
  specific = 4
FEATURE [App::DocumentObjectGroupPython] Ar_element002  label="Ar_element : 1"  # scripted group (container) (typed FeaturePython)
  n = 1
  ref = Ar_element
FEATURE [App::DocumentObjectGroupPython] G4_Ar  # scripted group (container) (typed FeaturePython)
  Dunit = g/cm3
  Dvalue = 0.00166201
  Group = -> [Ar_element002]
  conduct = 2
  density = 1
  expand = 3
  formula = Ar
  name = G4_Ar
  specific = 4
FEATURE [App::DocumentObjectGroupPython] K_element013  label="K_element : 003"  # scripted group (container) (typed FeaturePython)
  n = 1
  ref = K_element
FEATURE [App::DocumentObjectGroupPython] G4_K  # scripted group (container) (typed FeaturePython)
  Dunit = g/cm3
  Dvalue = 0.862
  Group = -> [K_element013]
  conduct = 2
  density = 1
  expand = 3
  formula = K
  name = G4_K
  specific = 4
FEATURE [App::DocumentObjectGroupPython] Ca_element014  label="Ca_element : 007"  # scripted group (container) (typed FeaturePython)
  n = 1
  ref = Ca_element
FEATURE [App::DocumentObjectGroupPython] G4_Ca  # scripted group (container) (typed FeaturePython)
  Dunit = g/cm3
  Dvalue = 1.55
  Group = -> [Ca_element014]
  conduct = 2
  density = 1
  expand = 3
  formula = Ca
  name = G4_Ca
  specific = 4
FEATURE [App::DocumentObjectGroupPython] Sc_element001  label="Sc_element : 1"  # scripted group (container) (typed FeaturePython)
  n = 1
  ref = Sc_element
FEATURE [App::DocumentObjectGroupPython] G4_Sc  # scripted group (container) (typed FeaturePython)
  Dunit = g/cm3
  Dvalue = 2.989
  Group = -> [Sc_element001]
  conduct = 2
  density = 1
  expand = 3
  formula = Sc
  name = G4_Sc
  specific = 4
FEATURE [App::DocumentObjectGroupPython] Ti_element004  label="Ti_element : 002"  # scripted group (container) (typed FeaturePython)
  n = 1
  ref = Ti_element
FEATURE [App::DocumentObjectGroupPython] G4_Ti  # scripted group (container) (typed FeaturePython)
  Dunit = g/cm3
  Dvalue = 4.54
  Group = -> [Ti_element004]
  conduct = 2
  density = 1
  expand = 3
  formula = Ti
  name = G4_Ti
  specific = 4
FEATURE [App::DocumentObjectGroupPython] V_element001  label="V_element : 1"  # scripted group (container) (typed FeaturePython)
  n = 1
  ref = V_element
FEATURE [App::DocumentObjectGroupPython] G4_V  # scripted group (container) (typed FeaturePython)
  Dunit = g/cm3
  Dvalue = 6.11
  Group = -> [V_element001]
  conduct = 2
  density = 1
  expand = 3
  formula = V
  name = G4_V
  specific = 4
FEATURE [App::DocumentObjectGroupPython] Cr_element001  label="Cr_element : 1"  # scripted group (container) (typed FeaturePython)
  n = 1
  ref = Cr_element
FEATURE [App::DocumentObjectGroupPython] G4_Cr  # scripted group (container) (typed FeaturePython)
  Dunit = g/cm3
  Dvalue = 7.18
  Group = -> [Cr_element001]
  conduct = 2
  density = 1
  expand = 3
  formula = Cr
  name = G4_Cr
  specific = 4
FEATURE [App::DocumentObjectGroupPython] Mn_element001  label="Mn_element : 1"  # scripted group (container) (typed FeaturePython)
  n = 1
  ref = Mn_element
FEATURE [App::DocumentObjectGroupPython] G4_Mn  # scripted group (container) (typed FeaturePython)
  Dunit = g/cm3
  Dvalue = 7.44
  Group = -> [Mn_element001]
  conduct = 2
  density = 1
  expand = 3
  formula = Mn
  name = G4_Mn
  specific = 4
FEATURE [App::DocumentObjectGroupPython] Fe_element007  label="Fe_element : 004"  # scripted group (container) (typed FeaturePython)
  n = 1
  ref = Fe_element
FEATURE [App::DocumentObjectGroupPython] G4_Fe  # scripted group (container) (typed FeaturePython)
  Dunit = g/cm3
  Dvalue = 7.874
  Group = -> [Fe_element007]
  conduct = 2
  density = 1
  expand = 3
  formula = Fe
  name = G4_Fe
  specific = 4
FEATURE [App::DocumentObjectGroupPython] Co_element001  label="Co_element : 1"  # scripted group (container) (typed FeaturePython)
  n = 1
  ref = Co_element
FEATURE [App::DocumentObjectGroupPython] G4_Co  # scripted group (container) (typed FeaturePython)
  Dunit = g/cm3
  Dvalue = 8.9
  Group = -> [Co_element001]
  conduct = 2
  density = 1
  expand = 3
  formula = Co
  name = G4_Co
  specific = 4
FEATURE [App::DocumentObjectGroupPython] Ni_element001  label="Ni_element : 1"  # scripted group (container) (typed FeaturePython)
  n = 1
  ref = Ni_element
FEATURE [App::DocumentObjectGroupPython] G4_Ni  # scripted group (container) (typed FeaturePython)
  Dunit = g/cm3
  Dvalue = 8.902
  Group = -> [Ni_element001]
  conduct = 2
  density = 1
  expand = 3
  formula = Ni
  name = G4_Ni
  specific = 4
FEATURE [App::DocumentObjectGroupPython] Cu_element001  label="Cu_element : 1"  # scripted group (container) (typed FeaturePython)
  n = 1
  ref = Cu_element
FEATURE [App::DocumentObjectGroupPython] G4_Cu  # scripted group (container) (typed FeaturePython)
  Dunit = g/cm3
  Dvalue = 8.96
  Group = -> [Cu_element001]
  conduct = 2
  density = 1
  expand = 3
  formula = Cu
  name = G4_Cu
  specific = 4
FEATURE [App::DocumentObjectGroupPython] Zn_element001  label="Zn_element : 1"  # scripted group (container) (typed FeaturePython)
  n = 1
  ref = Zn_element
FEATURE [App::DocumentObjectGroupPython] G4_Zn  # scripted group (container) (typed FeaturePython)
  Dunit = g/cm3
  Dvalue = 7.133
  Group = -> [Zn_element001]
  conduct = 2
  density = 1
  expand = 3
  formula = Zn
  name = G4_Zn
  specific = 4
FEATURE [App::DocumentObjectGroupPython] Ga_element002  label="Ga_element : 002"  # scripted group (container) (typed FeaturePython)
  n = 1
  ref = Ga_element
FEATURE [App::DocumentObjectGroupPython] G4_Ga  # scripted group (container) (typed FeaturePython)
  Dunit = g/cm3
  Dvalue = 5.904
  Group = -> [Ga_element002]
  conduct = 2
  density = 1
  expand = 3
  formula = Ga
  name = G4_Ga
  specific = 4
FEATURE [App::DocumentObjectGroupPython] Ge_element002  label="Ge_element : 1"  # scripted group (container) (typed FeaturePython)
  n = 1
  ref = Ge_element
FEATURE [App::DocumentObjectGroupPython] G4_Ge  # scripted group (container) (typed FeaturePython)
  Dunit = g/cm3
  Dvalue = 5.323
  Group = -> [Ge_element002]
  conduct = 2
  density = 1
  expand = 3
  formula = Ge
  name = G4_Ge
  specific = 4
FEATURE [App::DocumentObjectGroupPython] As_element003  label="As_element : 002"  # scripted group (container) (typed FeaturePython)
  n = 1
  ref = As_element
FEATURE [App::DocumentObjectGroupPython] G4_As  # scripted group (container) (typed FeaturePython)
  Dunit = g/cm3
  Dvalue = 5.73
  Group = -> [As_element003]
  conduct = 2
  density = 1
  expand = 3
  formula = As
  name = G4_As
  specific = 4
FEATURE [App::DocumentObjectGroupPython] Se_element001  label="Se_element : 1"  # scripted group (container) (typed FeaturePython)
  n = 1
  ref = Se_element
FEATURE [App::DocumentObjectGroupPython] G4_Se  # scripted group (container) (typed FeaturePython)
  Dunit = g/cm3
  Dvalue = 4.5
  Group = -> [Se_element001]
  conduct = 2
  density = 1
  expand = 3
  formula = Se
  name = G4_Se
  specific = 4
FEATURE [App::DocumentObjectGroupPython] Br_element007  label="Br_element : 004"  # scripted group (container) (typed FeaturePython)
  n = 1
  ref = Br_element
FEATURE [App::DocumentObjectGroupPython] G4_Br  # scripted group (container) (typed FeaturePython)
  Dunit = g/cm3
  Dvalue = 0.0070721
  Group = -> [Br_element007]
  conduct = 2
  density = 1
  expand = 3
  formula = Br
  name = G4_Br
  specific = 4
FEATURE [App::DocumentObjectGroupPython] Kr_element001  label="Kr_element : 1"  # scripted group (container) (typed FeaturePython)
  n = 1
  ref = Kr_element
FEATURE [App::DocumentObjectGroupPython] G4_Kr  # scripted group (container) (typed FeaturePython)
  Dunit = g/cm3
  Dvalue = 0.00347832
  Group = -> [Kr_element001]
  conduct = 2
  density = 1
  expand = 3
  formula = Kr
  name = G4_Kr
  specific = 4
FEATURE [App::DocumentObjectGroupPython] Rb_element001  label="Rb_element : 1"  # scripted group (container) (typed FeaturePython)
  n = 1
  ref = Rb_element
FEATURE [App::DocumentObjectGroupPython] G4_Rb  # scripted group (container) (typed FeaturePython)
  Dunit = g/cm3
  Dvalue = 1.532
  Group = -> [Rb_element001]
  conduct = 2
  density = 1
  expand = 3
  formula = Rb
  name = G4_Rb
  specific = 4
FEATURE [App::DocumentObjectGroupPython] Sr_element001  label="Sr_element : 1"  # scripted group (container) (typed FeaturePython)
  n = 1
  ref = Sr_element
FEATURE [App::DocumentObjectGroupPython] G4_Sr  # scripted group (container) (typed FeaturePython)
  Dunit = g/cm3
  Dvalue = 2.54
  Group = -> [Sr_element001]
  conduct = 2
  density = 1
  expand = 3
  formula = Sr
  name = G4_Sr
  specific = 4
FEATURE [App::DocumentObjectGroupPython] Y_element001  label="Y_element : 1"  # scripted group (container) (typed FeaturePython)
  n = 1
  ref = Y_element
FEATURE [App::DocumentObjectGroupPython] G4_Y  # scripted group (container) (typed FeaturePython)
  Dunit = g/cm3
  Dvalue = 4.469
  Group = -> [Y_element001]
  conduct = 2
  density = 1
  expand = 3
  formula = Y
  name = G4_Y
  specific = 4
FEATURE [App::DocumentObjectGroupPython] Zr_element001  label="Zr_element : 1"  # scripted group (container) (typed FeaturePython)
  n = 1
  ref = Zr_element
FEATURE [App::DocumentObjectGroupPython] G4_Zr  # scripted group (container) (typed FeaturePython)
  Dunit = g/cm3
  Dvalue = 6.506
  Group = -> [Zr_element001]
  conduct = 2
  density = 1
  expand = 3
  formula = Zr
  name = G4_Zr
  specific = 4
FEATURE [App::DocumentObjectGroupPython] Nb_element001  label="Nb_element : 1"  # scripted group (container) (typed FeaturePython)
  n = 1
  ref = Nb_element
FEATURE [App::DocumentObjectGroupPython] G4_Nb  # scripted group (container) (typed FeaturePython)
  Dunit = g/cm3
  Dvalue = 8.57
  Group = -> [Nb_element001]
  conduct = 2
  density = 1
  expand = 3
  formula = Nb
  name = G4_Nb
  specific = 4
FEATURE [App::DocumentObjectGroupPython] Mo_element001  label="Mo_element : 1"  # scripted group (container) (typed FeaturePython)
  n = 1
  ref = Mo_element
FEATURE [App::DocumentObjectGroupPython] G4_Mo  # scripted group (container) (typed FeaturePython)
  Dunit = g/cm3
  Dvalue = 10.22
  Group = -> [Mo_element001]
  conduct = 2
  density = 1
  expand = 3
  formula = Mo
  name = G4_Mo
  specific = 4
FEATURE [App::DocumentObjectGroupPython] Tc_element001  label="Tc_element : 1"  # scripted group (container) (typed FeaturePython)
  n = 1
  ref = Tc_element
FEATURE [App::DocumentObjectGroupPython] G4_Tc  # scripted group (container) (typed FeaturePython)
  Dunit = g/cm3
  Dvalue = 11.5
  Group = -> [Tc_element001]
  conduct = 2
  density = 1
  expand = 3
  formula = Tc
  name = G4_Tc
  specific = 4
FEATURE [App::DocumentObjectGroupPython] Ru_element001  label="Ru_element : 1"  # scripted group (container) (typed FeaturePython)
  n = 1
  ref = Ru_element
FEATURE [App::DocumentObjectGroupPython] G4_Ru  # scripted group (container) (typed FeaturePython)
  Dunit = g/cm3
  Dvalue = 12.41
  Group = -> [Ru_element001]
  conduct = 2
  density = 1
  expand = 3
  formula = Ru
  name = G4_Ru
  specific = 4
FEATURE [App::DocumentObjectGroupPython] Rh_element001  label="Rh_element : 1"  # scripted group (container) (typed FeaturePython)
  n = 1
  ref = Rh_element
FEATURE [App::DocumentObjectGroupPython] G4_Rh  # scripted group (container) (typed FeaturePython)
  Dunit = g/cm3
  Dvalue = 12.41
  Group = -> [Rh_element001]
  conduct = 2
  density = 1
  expand = 3
  formula = Rh
  name = G4_Rh
  specific = 4
FEATURE [App::DocumentObjectGroupPython] Pd_element001  label="Pd_element : 1"  # scripted group (container) (typed FeaturePython)
  n = 1
  ref = Pd_element
FEATURE [App::DocumentObjectGroupPython] G4_Pd  # scripted group (container) (typed FeaturePython)
  Dunit = g/cm3
  Dvalue = 12.02
  Group = -> [Pd_element001]
  conduct = 2
  density = 1
  expand = 3
  formula = Pd
  name = G4_Pd
  specific = 4
FEATURE [App::DocumentObjectGroupPython] Ag_element006  label="Ag_element : 004"  # scripted group (container) (typed FeaturePython)
  n = 1
  ref = Ag_element
FEATURE [App::DocumentObjectGroupPython] G4_Ag  # scripted group (container) (typed FeaturePython)
  Dunit = g/cm3
  Dvalue = 10.5
  Group = -> [Ag_element006]
  conduct = 2
  density = 1
  expand = 3
  formula = Ag
  name = G4_Ag
  specific = 4
FEATURE [App::DocumentObjectGroupPython] Cd_element003  label="Cd_element : 003"  # scripted group (container) (typed FeaturePython)
  n = 1
  ref = Cd_element
FEATURE [App::DocumentObjectGroupPython] G4_Cd  # scripted group (container) (typed FeaturePython)
  Dunit = g/cm3
  Dvalue = 8.65
  Group = -> [Cd_element003]
  conduct = 2
  density = 1
  expand = 3
  formula = Cd
  name = G4_Cd
  specific = 4
FEATURE [App::DocumentObjectGroupPython] In_element001  label="In_element : 1"  # scripted group (container) (typed FeaturePython)
  n = 1
  ref = In_element
FEATURE [App::DocumentObjectGroupPython] G4_In  # scripted group (container) (typed FeaturePython)
  Dunit = g/cm3
  Dvalue = 7.31
  Group = -> [In_element001]
  conduct = 2
  density = 1
  expand = 3
  formula = In
  name = G4_In
  specific = 4
FEATURE [App::DocumentObjectGroupPython] Sn_element001  label="Sn_element : 1"  # scripted group (container) (typed FeaturePython)
  n = 1
  ref = Sn_element
FEATURE [App::DocumentObjectGroupPython] G4_Sn  # scripted group (container) (typed FeaturePython)
  Dunit = g/cm3
  Dvalue = 7.31
  Group = -> [Sn_element001]
  conduct = 2
  density = 1
  expand = 3
  formula = Sn
  name = G4_Sn
  specific = 4
FEATURE [App::DocumentObjectGroupPython] Sb_element001  label="Sb_element : 1"  # scripted group (container) (typed FeaturePython)
  n = 1
  ref = Sb_element
FEATURE [App::DocumentObjectGroupPython] G4_Sb  # scripted group (container) (typed FeaturePython)
  Dunit = g/cm3
  Dvalue = 6.691
  Group = -> [Sb_element001]
  conduct = 2
  density = 1
  expand = 3
  formula = Sb
  name = G4_Sb
  specific = 4
FEATURE [App::DocumentObjectGroupPython] Te_element002  label="Te_element : 002"  # scripted group (container) (typed FeaturePython)
  n = 1
  ref = Te_element
FEATURE [App::DocumentObjectGroupPython] G4_Te  # scripted group (container) (typed FeaturePython)
  Dunit = g/cm3
  Dvalue = 6.24
  Group = -> [Te_element002]
  conduct = 2
  density = 1
  expand = 3
  formula = Te
  name = G4_Te
  specific = 4
FEATURE [App::DocumentObjectGroupPython] I_element010  label="I_element : 006"  # scripted group (container) (typed FeaturePython)
  n = 1
  ref = I_element
FEATURE [App::DocumentObjectGroupPython] G4_I  # scripted group (container) (typed FeaturePython)
  Dunit = g/cm3
  Dvalue = 4.93
  Group = -> [I_element010]
  conduct = 2
  density = 1
  expand = 3
  formula = I
  name = G4_I
  specific = 4
FEATURE [App::DocumentObjectGroupPython] Xe_element001  label="Xe_element : 1"  # scripted group (container) (typed FeaturePython)
  n = 1
  ref = Xe_element
FEATURE [App::DocumentObjectGroupPython] G4_Xe  # scripted group (container) (typed FeaturePython)
  Dunit = g/cm3
  Dvalue = 0.00548536
  Group = -> [Xe_element001]
  conduct = 2
  density = 1
  expand = 3
  formula = Xe
  name = G4_Xe
  specific = 4
FEATURE [App::DocumentObjectGroupPython] Cs_element003  label="Cs_element : 003"  # scripted group (container) (typed FeaturePython)
  n = 1
  ref = Cs_element
FEATURE [App::DocumentObjectGroupPython] G4_Cs  # scripted group (container) (typed FeaturePython)
  Dunit = g/cm3
  Dvalue = 1.873
  Group = -> [Cs_element003]
  conduct = 2
  density = 1
  expand = 3
  formula = Cs
  name = G4_Cs
  specific = 4
FEATURE [App::DocumentObjectGroupPython] Ba_element003  label="Ba_element : 003"  # scripted group (container) (typed FeaturePython)
  n = 1
  ref = Ba_element
FEATURE [App::DocumentObjectGroupPython] G4_Ba  # scripted group (container) (typed FeaturePython)
  Dunit = g/cm3
  Dvalue = 3.5
  Group = -> [Ba_element003]
  conduct = 2
  density = 1
  expand = 3
  formula = Ba
  name = G4_Ba
  specific = 4
FEATURE [App::DocumentObjectGroupPython] La_element003  label="La_element : 003"  # scripted group (container) (typed FeaturePython)
  n = 1
  ref = La_element
FEATURE [App::DocumentObjectGroupPython] G4_La  # scripted group (container) (typed FeaturePython)
  Dunit = g/cm3
  Dvalue = 6.154
  Group = -> [La_element003]
  conduct = 2
  density = 1
  expand = 3
  formula = La
  name = G4_La
  specific = 4
FEATURE [App::DocumentObjectGroupPython] Ce_element002  label="Ce_element : 1"  # scripted group (container) (typed FeaturePython)
  n = 1
  ref = Ce_element
FEATURE [App::DocumentObjectGroupPython] G4_Ce  # scripted group (container) (typed FeaturePython)
  Dunit = g/cm3
  Dvalue = 6.657
  Group = -> [Ce_element002]
  conduct = 2
  density = 1
  expand = 3
  formula = Ce
  name = G4_Ce
  specific = 4
FEATURE [App::DocumentObjectGroupPython] Pr_element001  label="Pr_element : 1"  # scripted group (container) (typed FeaturePython)
  n = 1
  ref = Pr_element
FEATURE [App::DocumentObjectGroupPython] G4_Pr  # scripted group (container) (typed FeaturePython)
  Dunit = g/cm3
  Dvalue = 6.71
  Group = -> [Pr_element001]
  conduct = 2
  density = 1
  expand = 3
  formula = Pr
  name = G4_Pr
  specific = 4
FEATURE [App::DocumentObjectGroupPython] Nd_element001  label="Nd_element : 1"  # scripted group (container) (typed FeaturePython)
  n = 1
  ref = Nd_element
FEATURE [App::DocumentObjectGroupPython] G4_Nd  # scripted group (container) (typed FeaturePython)
  Dunit = g/cm3
  Dvalue = 6.9
  Group = -> [Nd_element001]
  conduct = 2
  density = 1
  expand = 3
  formula = Nd
  name = G4_Nd
  specific = 4
FEATURE [App::DocumentObjectGroupPython] Pm_element001  label="Pm_element : 1"  # scripted group (container) (typed FeaturePython)
  n = 1
  ref = Pm_element
FEATURE [App::DocumentObjectGroupPython] G4_Pm  # scripted group (container) (typed FeaturePython)
  Dunit = g/cm3
  Dvalue = 7.22
  Group = -> [Pm_element001]
  conduct = 2
  density = 1
  expand = 3
  formula = Pm
  name = G4_Pm
  specific = 4
FEATURE [App::DocumentObjectGroupPython] Sm_element001  label="Sm_element : 1"  # scripted group (container) (typed FeaturePython)
  n = 1
  ref = Sm_element
FEATURE [App::DocumentObjectGroupPython] G4_Sm  # scripted group (container) (typed FeaturePython)
  Dunit = g/cm3
  Dvalue = 7.46
  Group = -> [Sm_element001]
  conduct = 2
  density = 1
  expand = 3
  formula = Sm
  name = G4_Sm
  specific = 4
FEATURE [App::DocumentObjectGroupPython] Eu_element001  label="Eu_element : 1"  # scripted group (container) (typed FeaturePython)
  n = 1
  ref = Eu_element
FEATURE [App::DocumentObjectGroupPython] G4_Eu  # scripted group (container) (typed FeaturePython)
  Dunit = g/cm3
  Dvalue = 5.243
  Group = -> [Eu_element001]
  conduct = 2
  density = 1
  expand = 3
  formula = Eu
  name = G4_Eu
  specific = 4
FEATURE [App::DocumentObjectGroupPython] Gd_element002  label="Gd_element : 1"  # scripted group (container) (typed FeaturePython)
  n = 1
  ref = Gd_element
FEATURE [App::DocumentObjectGroupPython] G4_Gd  # scripted group (container) (typed FeaturePython)
  Dunit = g/cm3
  Dvalue = 7.9004
  Group = -> [Gd_element002]
  conduct = 2
  density = 1
  expand = 3
  formula = Gd
  name = G4_Gd
  specific = 4
FEATURE [App::DocumentObjectGroupPython] Tb_element001  label="Tb_element : 1"  # scripted group (container) (typed FeaturePython)
  n = 1
  ref = Tb_element
FEATURE [App::DocumentObjectGroupPython] G4_Tb  # scripted group (container) (typed FeaturePython)
  Dunit = g/cm3
  Dvalue = 8.229
  Group = -> [Tb_element001]
  conduct = 2
  density = 1
  expand = 3
  formula = Tb
  name = G4_Tb
  specific = 4
FEATURE [App::DocumentObjectGroupPython] Dy_element001  label="Dy_element : 1"  # scripted group (container) (typed FeaturePython)
  n = 1
  ref = Dy_element
FEATURE [App::DocumentObjectGroupPython] G4_Dy  # scripted group (container) (typed FeaturePython)
  Dunit = g/cm3
  Dvalue = 8.55
  Group = -> [Dy_element001]
  conduct = 2
  density = 1
  expand = 3
  formula = Dy
  name = G4_Dy
  specific = 4
FEATURE [App::DocumentObjectGroupPython] Ho_element001  label="Ho_element : 1"  # scripted group (container) (typed FeaturePython)
  n = 1
  ref = Ho_element
FEATURE [App::DocumentObjectGroupPython] G4_Ho  # scripted group (container) (typed FeaturePython)
  Dunit = g/cm3
  Dvalue = 8.795
  Group = -> [Ho_element001]
  conduct = 2
  density = 1
  expand = 3
  formula = Ho
  name = G4_Ho
  specific = 4
FEATURE [App::DocumentObjectGroupPython] Er_element001  label="Er_element : 1"  # scripted group (container) (typed FeaturePython)
  n = 1
  ref = Er_element
FEATURE [App::DocumentObjectGroupPython] G4_Er  # scripted group (container) (typed FeaturePython)
  Dunit = g/cm3
  Dvalue = 9.066
  Group = -> [Er_element001]
  conduct = 2
  density = 1
  expand = 3
  formula = Er
  name = G4_Er
  specific = 4
FEATURE [App::DocumentObjectGroupPython] Tm_element001  label="Tm_element : 1"  # scripted group (container) (typed FeaturePython)
  n = 1
  ref = Tm_element
FEATURE [App::DocumentObjectGroupPython] G4_Tm  # scripted group (container) (typed FeaturePython)
  Dunit = g/cm3
  Dvalue = 9.321
  Group = -> [Tm_element001]
  conduct = 2
  density = 1
  expand = 3
  formula = Tm
  name = G4_Tm
  specific = 4
FEATURE [App::DocumentObjectGroupPython] Yb_element001  label="Yb_element : 1"  # scripted group (container) (typed FeaturePython)
  n = 1
  ref = Yb_element
FEATURE [App::DocumentObjectGroupPython] G4_Yb  # scripted group (container) (typed FeaturePython)
  Dunit = g/cm3
  Dvalue = 6.73
  Group = -> [Yb_element001]
  conduct = 2
  density = 1
  expand = 3
  formula = Yb
  name = G4_Yb
  specific = 4
FEATURE [App::DocumentObjectGroupPython] Lu_element001  label="Lu_element : 1"  # scripted group (container) (typed FeaturePython)
  n = 1
  ref = Lu_element
FEATURE [App::DocumentObjectGroupPython] G4_Lu  # scripted group (container) (typed FeaturePython)
  Dunit = g/cm3
  Dvalue = 9.84
  Group = -> [Lu_element001]
  conduct = 2
  density = 1
  expand = 3
  formula = Lu
  name = G4_Lu
  specific = 4
FEATURE [App::DocumentObjectGroupPython] Hf_element001  label="Hf_element : 1"  # scripted group (container) (typed FeaturePython)
  n = 1
  ref = Hf_element
FEATURE [App::DocumentObjectGroupPython] G4_Hf  # scripted group (container) (typed FeaturePython)
  Dunit = g/cm3
  Dvalue = 13.31
  Group = -> [Hf_element001]
  conduct = 2
  density = 1
  expand = 3
  formula = Hf
  name = G4_Hf
  specific = 4
FEATURE [App::DocumentObjectGroupPython] Ta_element001  label="Ta_element : 1"  # scripted group (container) (typed FeaturePython)
  n = 1
  ref = Ta_element
FEATURE [App::DocumentObjectGroupPython] G4_Ta  # scripted group (container) (typed FeaturePython)
  Dunit = g/cm3
  Dvalue = 16.654
  Group = -> [Ta_element001]
  conduct = 2
  density = 1
  expand = 3
  formula = Ta
  name = G4_Ta
  specific = 4
FEATURE [App::DocumentObjectGroupPython] W_element004  label="W_element : 004"  # scripted group (container) (typed FeaturePython)
  n = 1
  ref = W_element
FEATURE [App::DocumentObjectGroupPython] G4_W  # scripted group (container) (typed FeaturePython)
  Dunit = g/cm3
  Dvalue = 19.3
  Group = -> [W_element004]
  conduct = 2
  density = 1
  expand = 3
  formula = W
  name = G4_W
  specific = 4
FEATURE [App::DocumentObjectGroupPython] Re_element001  label="Re_element : 1"  # scripted group (container) (typed FeaturePython)
  n = 1
  ref = Re_element
FEATURE [App::DocumentObjectGroupPython] G4_Re  # scripted group (container) (typed FeaturePython)
  Dunit = g/cm3
  Dvalue = 21.02
  Group = -> [Re_element001]
  conduct = 2
  density = 1
  expand = 3
  formula = Re
  name = G4_Re
  specific = 4
FEATURE [App::DocumentObjectGroupPython] Os_element001  label="Os_element : 1"  # scripted group (container) (typed FeaturePython)
  n = 1
  ref = Os_element
FEATURE [App::DocumentObjectGroupPython] G4_Os  # scripted group (container) (typed FeaturePython)
  Dunit = g/cm3
  Dvalue = 22.57
  Group = -> [Os_element001]
  conduct = 2
  density = 1
  expand = 3
  formula = Os
  name = G4_Os
  specific = 4
FEATURE [App::DocumentObjectGroupPython] Ir_element001  label="Ir_element : 1"  # scripted group (container) (typed FeaturePython)
  n = 1
  ref = Ir_element
FEATURE [App::DocumentObjectGroupPython] G4_Ir  # scripted group (container) (typed FeaturePython)
  Dunit = g/cm3
  Dvalue = 22.42
  Group = -> [Ir_element001]
  conduct = 2
  density = 1
  expand = 3
  formula = Ir
  name = G4_Ir
  specific = 4
FEATURE [App::DocumentObjectGroupPython] Pt_element001  label="Pt_element : 1"  # scripted group (container) (typed FeaturePython)
  n = 1
  ref = Pt_element
FEATURE [App::DocumentObjectGroupPython] G4_Pt  # scripted group (container) (typed FeaturePython)
  Dunit = g/cm3
  Dvalue = 21.45
  Group = -> [Pt_element001]
  conduct = 2
  density = 1
  expand = 3
  formula = Pt
  name = G4_Pt
  specific = 4
FEATURE [App::DocumentObjectGroupPython] Au_element001  label="Au_element : 1"  # scripted group (container) (typed FeaturePython)
  n = 1
  ref = Au_element
FEATURE [App::DocumentObjectGroupPython] G4_Au  # scripted group (container) (typed FeaturePython)
  Dunit = g/cm3
  Dvalue = 19.32
  Group = -> [Au_element001]
  conduct = 2
  density = 1
  expand = 3
  formula = Au
  name = G4_Au
  specific = 4
FEATURE [App::DocumentObjectGroupPython] Hg_element002  label="Hg_element : 002"  # scripted group (container) (typed FeaturePython)
  n = 1
  ref = Hg_element
FEATURE [App::DocumentObjectGroupPython] G4_Hg  # scripted group (container) (typed FeaturePython)
  Dunit = g/cm3
  Dvalue = 13.546
  Group = -> [Hg_element002]
  conduct = 2
  density = 1
  expand = 3
  formula = Hg
  name = G4_Hg
  specific = 4
FEATURE [App::DocumentObjectGroupPython] Tl_element002  label="Tl_element : 002"  # scripted group (container) (typed FeaturePython)
  n = 1
  ref = Tl_element
FEATURE [App::DocumentObjectGroupPython] G4_Tl  # scripted group (container) (typed FeaturePython)
  Dunit = g/cm3
  Dvalue = 11.72
  Group = -> [Tl_element002]
  conduct = 2
  density = 1
  expand = 3
  formula = Tl
  name = G4_Tl
  specific = 4
FEATURE [App::DocumentObjectGroupPython] Pb_element003  label="Pb_element : 1"  # scripted group (container) (typed FeaturePython)
  n = 1
  ref = Pb_element
FEATURE [App::DocumentObjectGroupPython] G4_Pb  # scripted group (container) (typed FeaturePython)
  Dunit = g/cm3
  Dvalue = 11.35
  Group = -> [Pb_element003]
  conduct = 2
  density = 1
  expand = 3
  formula = Pb
  name = G4_Pb
  specific = 4
FEATURE [App::DocumentObjectGroupPython] Bi_element002  label="Bi_element : 1"  # scripted group (container) (typed FeaturePython)
  n = 1
  ref = Bi_element
FEATURE [App::DocumentObjectGroupPython] G4_Bi  # scripted group (container) (typed FeaturePython)
  Dunit = g/cm3
  Dvalue = 9.747
  Group = -> [Bi_element002]
  conduct = 2
  density = 1
  expand = 3
  formula = Bi
  name = G4_Bi
  specific = 4
FEATURE [App::DocumentObjectGroupPython] Po_element001  label="Po_element : 1"  # scripted group (container) (typed FeaturePython)
  n = 1
  ref = Po_element
FEATURE [App::DocumentObjectGroupPython] G4_Po  # scripted group (container) (typed FeaturePython)
  Dunit = g/cm3
  Dvalue = 9.32
  Group = -> [Po_element001]
  conduct = 2
  density = 1
  expand = 3
  formula = Po
  name = G4_Po
  specific = 4
FEATURE [App::DocumentObjectGroupPython] At_element001  label="At_element : 1"  # scripted group (container) (typed FeaturePython)
  n = 1
  ref = At_element
FEATURE [App::DocumentObjectGroupPython] G4_At  # scripted group (container) (typed FeaturePython)
  Dunit = g/cm3
  Dvalue = 9.32
  Group = -> [At_element001]
  conduct = 2
  density = 1
  expand = 3
  formula = At
  name = G4_At
  specific = 4
FEATURE [App::DocumentObjectGroupPython] Rn_element001  label="Rn_element : 1"  # scripted group (container) (typed FeaturePython)
  n = 1
  ref = Rn_element
FEATURE [App::DocumentObjectGroupPython] G4_Rn  # scripted group (container) (typed FeaturePython)
  Dunit = g/cm3
  Dvalue = 0.00900662
  Group = -> [Rn_element001]
  conduct = 2
  density = 1
  expand = 3
  formula = Rn
  name = G4_Rn
  specific = 4
FEATURE [App::DocumentObjectGroupPython] Fr_element001  label="Fr_element : 1"  # scripted group (container) (typed FeaturePython)
  n = 1
  ref = Fr_element
FEATURE [App::DocumentObjectGroupPython] G4_Fr  # scripted group (container) (typed FeaturePython)
  Dunit = g/cm3
  Dvalue = 1
  Group = -> [Fr_element001]
  conduct = 2
  density = 1
  expand = 3
  formula = Fr
  name = G4_Fr
  specific = 4
FEATURE [App::DocumentObjectGroupPython] Ra_element001  label="Ra_element : 1"  # scripted group (container) (typed FeaturePython)
  n = 1
  ref = Ra_element
FEATURE [App::DocumentObjectGroupPython] G4_Ra  # scripted group (container) (typed FeaturePython)
  Dunit = g/cm3
  Dvalue = 5
  Group = -> [Ra_element001]
  conduct = 2
  density = 1
  expand = 3
  formula = Ra
  name = G4_Ra
  specific = 4
FEATURE [App::DocumentObjectGroupPython] Ac_element001  label="Ac_element : 1"  # scripted group (container) (typed FeaturePython)
  n = 1
  ref = Ac_element
FEATURE [App::DocumentObjectGroupPython] G4_Ac  # scripted group (container) (typed FeaturePython)
  Dunit = g/cm3
  Dvalue = 10.07
  Group = -> [Ac_element001]
  conduct = 2
  density = 1
  expand = 3
  formula = Ac
  name = G4_Ac
  specific = 4
FEATURE [App::DocumentObjectGroupPython] Th_element001  label="Th_element : 1"  # scripted group (container) (typed FeaturePython)
  n = 1
  ref = Th_element
FEATURE [App::DocumentObjectGroupPython] G4_Th  # scripted group (container) (typed FeaturePython)
  Dunit = g/cm3
  Dvalue = 11.72
  Group = -> [Th_element001]
  conduct = 2
  density = 1
  expand = 3
  formula = Th
  name = G4_Th
  specific = 4
FEATURE [App::DocumentObjectGroupPython] Pa_element001  label="Pa_element : 1"  # scripted group (container) (typed FeaturePython)
  n = 1
  ref = Pa_element
FEATURE [App::DocumentObjectGroupPython] G4_Pa  # scripted group (container) (typed FeaturePython)
  Dunit = g/cm3
  Dvalue = 15.37
  Group = -> [Pa_element001]
  conduct = 2
  density = 1
  expand = 3
  formula = Pa
  name = G4_Pa
  specific = 4
FEATURE [App::DocumentObjectGroupPython] U_element004  label="U_element : 004"  # scripted group (container) (typed FeaturePython)
  n = 1
  ref = U_element
FEATURE [App::DocumentObjectGroupPython] G4_U  # scripted group (container) (typed FeaturePython)
  Dunit = g/cm3
  Dvalue = 18.95
  Group = -> [U_element004]
  conduct = 2
  density = 1
  expand = 3
  formula = U
  name = G4_U
  specific = 4
FEATURE [App::DocumentObjectGroupPython] Np_element001  label="Np_element : 1"  # scripted group (container) (typed FeaturePython)
  n = 1
  ref = Np_element
FEATURE [App::DocumentObjectGroupPython] G4_Np  # scripted group (container) (typed FeaturePython)
  Dunit = g/cm3
  Dvalue = 20.25
  Group = -> [Np_element001]
  conduct = 2
  density = 1
  expand = 3
  formula = Np
  name = G4_Np
  specific = 4
FEATURE [App::DocumentObjectGroupPython] Pu_element002  label="Pu_element : 002"  # scripted group (container) (typed FeaturePython)
  n = 1
  ref = Pu_element
FEATURE [App::DocumentObjectGroupPython] G4_Pu  # scripted group (container) (typed FeaturePython)
  Dunit = g/cm3
  Dvalue = 19.84
  Group = -> [Pu_element002]
  conduct = 2
  density = 1
  expand = 3
  formula = Pu
  name = G4_Pu
  specific = 4
FEATURE [App::DocumentObjectGroupPython] Am_element001  label="Am_element : 1"  # scripted group (container) (typed FeaturePython)
  n = 1
  ref = Am_element
FEATURE [App::DocumentObjectGroupPython] G4_Am  # scripted group (container) (typed FeaturePython)
  Dunit = g/cm3
  Dvalue = 13.67
  Group = -> [Am_element001]
  conduct = 2
  density = 1
  expand = 3
  formula = Am
  name = G4_Am
  specific = 4
FEATURE [App::DocumentObjectGroupPython] Cm_element001  label="Cm_element : 1"  # scripted group (container) (typed FeaturePython)
  n = 1
  ref = Cm_element
FEATURE [App::DocumentObjectGroupPython] G4_Cm  # scripted group (container) (typed FeaturePython)
  Dunit = g/cm3
  Dvalue = 13.51
  Group = -> [Cm_element001]
  conduct = 2
  density = 1
  expand = 3
  formula = Cm
  name = G4_Cm
  specific = 4
FEATURE [App::DocumentObjectGroupPython] Bk_element001  label="Bk_element : 1"  # scripted group (container) (typed FeaturePython)
  n = 1
  ref = Bk_element
FEATURE [App::DocumentObjectGroupPython] G4_Bk  # scripted group (container) (typed FeaturePython)
  Dunit = g/cm3
  Dvalue = 14
  Group = -> [Bk_element001]
  conduct = 2
  density = 1
  expand = 3
  formula = Bk
  name = G4_Bk
  specific = 4
FEATURE [App::DocumentObjectGroupPython] Cf_element001  label="Cf_element : 1"  # scripted group (container) (typed FeaturePython)
  n = 1
  ref = Cf_element
FEATURE [App::DocumentObjectGroupPython] G4_Cf  # scripted group (container) (typed FeaturePython)
  Dunit = g/cm3
  Dvalue = 10
  Group = -> [Cf_element001]
  conduct = 2
  density = 1
  expand = 3
  formula = Cf
  name = G4_Cf
  specific = 4
FEATURE [App::DocumentObjectGroupPython] Element  # scripted group (container) (typed FeaturePython)
  Group = -> [G4_H,G4_He,G4_Li,G4_Be,G4_B,G4_C,G4_N,G4_O,G4_F,G4_Ne,G4_Na,G4_Mg,G4_Al,G4_Si,G4_P,G4_S,G4_Cl,G4_Ar,G4_K,G4_Ca,G4_Sc,G4_Ti,G4_V,G4_Cr,G4_Mn,G4_Fe,G4_Co,G4_Ni,G4_Cu,G4_Zn,G4_Ga,G4_Ge,G4_As,G4_Se,G4_Br,G4_Kr,G4_Rb,G4_Sr,G4_Y,G4_Zr,G4_Nb,G4_Mo,G4_Tc,G4_Ru,G4_Rh,G4_Pd,G4_Ag,G4_Cd,G4_In,G4_Sn,G4_Sb,G4_Te,G4_I,G4_Xe,G4_Cs,G4_Ba,G4_La,G4_Ce,G4_Pr,G4_Nd,G4_Pm,G4_Sm,G4_Eu,G4_Gd,G4_Tb,G4_Dy,G4_Ho,G4_Er,+30 more]
FEATURE [App::DocumentObjectGroupPython] H_element114  label="H_element : 063"  # scripted group (container) (typed FeaturePython)
  n = 2
  ref = H_element
FEATURE [App::DocumentObjectGroupPython] G4_lH2  # scripted group (container) (typed FeaturePython)
  Dunit = g/cm3
  Dvalue = 0.0708
  Group = -> [H_element114]
  conduct = 2
  density = 1
  expand = 3
  formula = G4_lH2
  name = G4_lH2
  specific = 4
FEATURE [App::DocumentObjectGroupPython] N_element049  label="N_element : 022"  # scripted group (container) (typed FeaturePython)
  n = 2
  ref = N_element
FEATURE [App::DocumentObjectGroupPython] G4_lN2  # scripted group (container) (typed FeaturePython)
  Dunit = g/cm3
  Dvalue = 0.807
  Group = -> [N_element049]
  conduct = 2
  density = 1
  expand = 3
  formula = G4_lN2
  name = G4_lN2
  specific = 4
FEATURE [App::DocumentObjectGroupPython] O_element106  label="O_element : 060"  # scripted group (container) (typed FeaturePython)
  n = 2
  ref = O_element
FEATURE [App::DocumentObjectGroupPython] G4_lO2  # scripted group (container) (typed FeaturePython)
  Dunit = g/cm3
  Dvalue = 1.141
  Group = -> [O_element106]
  conduct = 2
  density = 1
  expand = 3
  formula = G4_lO2
  name = G4_lO2
  specific = 4
FEATURE [App::DocumentObjectGroupPython] Ar  label="Ar : 1"  # scripted group (container) (typed FeaturePython)
  n = 1
  ref = Ar
FEATURE [App::DocumentObjectGroupPython] G4_lAr  # scripted group (container) (typed FeaturePython)
  Dunit = g/cm3
  Dvalue = 1.396
  Group = -> [Ar]
  conduct = 2
  density = 1
  expand = 3
  formula = G4_lAr
  name = G4_lAr
  specific = 4
FEATURE [App::DocumentObjectGroupPython] Br  label="Br : 1"  # scripted group (container) (typed FeaturePython)
  n = 1
  ref = Br
FEATURE [App::DocumentObjectGroupPython] G4_lBr  # scripted group (container) (typed FeaturePython)
  Dunit = g/cm3
  Dvalue = 3.1028
  Group = -> [Br]
  conduct = 2
  density = 1
  expand = 3
  formula = G4_lBr
  name = G4_lBr
  specific = 4
FEATURE [App::DocumentObjectGroupPython] Kr  label="Kr : 1"  # scripted group (container) (typed FeaturePython)
  n = 1
  ref = Kr
FEATURE [App::DocumentObjectGroupPython] G4_lKr  # scripted group (container) (typed FeaturePython)
  Dunit = g/cm3
  Dvalue = 2.418
  Group = -> [Kr]
  conduct = 2
  density = 1
  expand = 3
  formula = G4_lKr
  name = G4_lKr
  specific = 4
FEATURE [App::DocumentObjectGroupPython] Xe  label="Xe : 1"  # scripted group (container) (typed FeaturePython)
  n = 1
  ref = Xe
FEATURE [App::DocumentObjectGroupPython] G4_lXe  # scripted group (container) (typed FeaturePython)
  Dunit = g/cm3
  Dvalue = 2.953
  Group = -> [Xe]
  conduct = 2
  density = 1
  expand = 3
  formula = G4_lXe
  name = G4_lXe
  specific = 4
FEATURE [App::DocumentObjectGroupPython] O_element107  label="O_element : 061"  # scripted group (container) (typed FeaturePython)
  n = 4
  ref = O_element
FEATURE [App::DocumentObjectGroupPython] Pb_element004  label="Pb_element : 002"  # scripted group (container) (typed FeaturePython)
  n = 1
  ref = Pb_element
FEATURE [App::DocumentObjectGroupPython] W_element005  label="W_element : 005"  # scripted group (container) (typed FeaturePython)
  n = 1
  ref = W_element
FEATURE [App::DocumentObjectGroupPython] G4_PbWO4  # scripted group (container) (typed FeaturePython)
  Dunit = g/cm3
  Dvalue = 8.28
  Group = -> [O_element107,Pb_element004,W_element005]
  conduct = 2
  density = 1
  expand = 3
  formula = G4_PbWO4
  name = G4_PbWO4
  specific = 4
FEATURE [App::DocumentObjectGroupPython] alactic  label="alactic : 1"  # scripted group (container) (typed FeaturePython)
  n = 1
  ref = alactic
FEATURE [App::DocumentObjectGroupPython] G4_Galactic  # scripted group (container) (typed FeaturePython)
  Dunit = g/cm3
  Dvalue = 0
  Group = -> [alactic]
  conduct = 2
  density = 1
  expand = 3
  formula = G4_Galactic
  name = G4_Galactic
  specific = 4
FEATURE [App::DocumentObjectGroupPython] RAPHITE_POROUS  label="RAPHITE_POROUS : 1"  # scripted group (container) (typed FeaturePython)
  n = 1
  ref = RAPHITE_POROUS
FEATURE [App::DocumentObjectGroupPython] G4_GRAPHITE_POROUS  # scripted group (container) (typed FeaturePython)
  Dunit = g/cm3
  Dvalue = 1.7
  Group = -> [RAPHITE_POROUS]
  conduct = 2
  density = 1
  expand = 3
  formula = G4_GRAPHITE_POROUS
  name = G4_GRAPHITE_POROUS
  specific = 4
FEATURE [App::DocumentObjectGroupPython] H_element115  label="H_element : 0.150"  # scripted group (container) (typed FeaturePython)
  n = 0.080538
FEATURE [App::DocumentObjectGroupPython] C_element125  label="C_element : 0.600"  # scripted group (container) (typed FeaturePython)
  n = 0.599848
FEATURE [App::DocumentObjectGroupPython] O_element108  label="O_element : 0.320"  # scripted group (container) (typed FeaturePython)
  n = 0.319614
FEATURE [App::DocumentObjectGroupPython] G4_LUCITE  # scripted group (container) (typed FeaturePython)
  Dunit = g/cm3
  Dvalue = 1.19
  Group = -> [H_element115,C_element125,O_element108]
  conduct = 2
  density = 1
  expand = 3
  formula = G4_LUCITE
  name = G4_LUCITE
  specific = 4
FEATURE [App::DocumentObjectGroupPython] Cu_element002  label="Cu_element : 62"  # scripted group (container) (typed FeaturePython)
  n = 62
  ref = Cu_element
FEATURE [App::DocumentObjectGroupPython] Zn_element002  label="Zn_element : 35"  # scripted group (container) (typed FeaturePython)
  n = 35
  ref = Zn_element
FEATURE [App::DocumentObjectGroupPython] Pb_element005  label="Pb_element : 3"  # scripted group (container) (typed FeaturePython)
  n = 3
  ref = Pb_element
FEATURE [App::DocumentObjectGroupPython] G4_BRASS  # scripted group (container) (typed FeaturePython)
  Dunit = g/cm3
  Dvalue = 8.52
  Group = -> [Cu_element002,Zn_element002,Pb_element005]
  conduct = 2
  density = 1
  expand = 3
  formula = G4_BRASS
  name = G4_BRASS
  specific = 4
FEATURE [App::DocumentObjectGroupPython] Cu_element003  label="Cu_element : 89"  # scripted group (container) (typed FeaturePython)
  n = 89
  ref = Cu_element
FEATURE [App::DocumentObjectGroupPython] Zn_element003  label="Zn_element : 9"  # scripted group (container) (typed FeaturePython)
  n = 9
  ref = Zn_element
FEATURE [App::DocumentObjectGroupPython] Pb_element006  label="Pb_element : 2"  # scripted group (container) (typed FeaturePython)
  n = 2
  ref = Pb_element
FEATURE [App::DocumentObjectGroupPython] G4_BRONZE  # scripted group (container) (typed FeaturePython)
  Dunit = g/cm3
  Dvalue = 8.82
  Group = -> [Cu_element003,Zn_element003,Pb_element006]
  conduct = 2
  density = 1
  expand = 3
  formula = G4_BRONZE
  name = G4_BRONZE
  specific = 4
FEATURE [App::DocumentObjectGroupPython] Fe_element008  label="Fe_element : 74"  # scripted group (container) (typed FeaturePython)
  n = 74
  ref = Fe_element
FEATURE [App::DocumentObjectGroupPython] Cr_element002  label="Cr_element : 18"  # scripted group (container) (typed FeaturePython)
  n = 18
  ref = Cr_element
FEATURE [App::DocumentObjectGroupPython] Ni_element002  label="Ni_element : 8"  # scripted group (container) (typed FeaturePython)
  n = 8
  ref = Ni_element
FEATURE [App::DocumentObjectGroupPython] G4_STAINLESS_STEEL  label="G4_STAINLESS-STEEL"  # scripted group (container) (typed FeaturePython)
  Dunit = g/cm3
  Dvalue = 8
  Group = -> [Fe_element008,Cr_element002,Ni_element002]
  conduct = 2
  density = 1
  expand = 3
  formula = G4_STAINLESS-STEEL
  name = G4_STAINLESS-STEEL
  specific = 4
FEATURE [App::DocumentObjectGroupPython] H_element116  label="H_element : 064"  # scripted group (container) (typed FeaturePython)
  n = 18
  ref = H_element
FEATURE [App::DocumentObjectGroupPython] C_element126  label="C_element : 071"  # scripted group (container) (typed FeaturePython)
  n = 12
  ref = C_element
FEATURE [App::DocumentObjectGroupPython] O_element109  label="O_element : 062"  # scripted group (container) (typed FeaturePython)
  n = 7
  ref = O_element
FEATURE [App::DocumentObjectGroupPython] G4_CR39  # scripted group (container) (typed FeaturePython)
  Dunit = g/cm3
  Dvalue = 1.32
  Group = -> [H_element116,C_element126,O_element109]
  conduct = 2
  density = 1
  expand = 3
  formula = G4_CR39
  name = G4_CR39
  specific = 4
FEATURE [App::DocumentObjectGroupPython] H_element117  label="H_element : 38"  # scripted group (container) (typed FeaturePython)
  n = 38
  ref = H_element
FEATURE [App::DocumentObjectGroupPython] C_element127  label="C_element : 072"  # scripted group (container) (typed FeaturePython)
  n = 18
  ref = C_element
FEATURE [App::DocumentObjectGroupPython] O_element110  label="O_element : 063"  # scripted group (container) (typed FeaturePython)
  n = 1
  ref = O_element
FEATURE [App::DocumentObjectGroupPython] G4_OCTADECANOL  # scripted group (container) (typed FeaturePython)
  Dunit = g/cm3
  Dvalue = 0.812
  Group = -> [H_element117,C_element127,O_element110]
  conduct = 2
  density = 1
  expand = 3
  formula = G4_OCTADECANOL
  name = G4_OCTADECANOL
  specific = 4
FEATURE [App::DocumentObjectGroupPython] HEP  # scripted group (container) (typed FeaturePython)
  Group = -> [G4_lH2,G4_lN2,G4_lO2,G4_lAr,G4_lBr,G4_lKr,G4_lXe,G4_PbWO4,G4_Galactic,G4_GRAPHITE_POROUS,G4_LUCITE,G4_BRASS,G4_BRONZE,G4_STAINLESS_STEEL,G4_CR39,G4_OCTADECANOL]
FEATURE [App::DocumentObjectGroupPython] C_element128  label="C_element : 073"  # scripted group (container) (typed FeaturePython)
  n = 14
  ref = C_element
FEATURE [App::DocumentObjectGroupPython] H_element118  label="H_element : 065"  # scripted group (container) (typed FeaturePython)
  n = 10
  ref = H_element
FEATURE [App::DocumentObjectGroupPython] O_element111  label="O_element : 064"  # scripted group (container) (typed FeaturePython)
  n = 2
  ref = O_element
FEATURE [App::DocumentObjectGroupPython] N_element050  label="N_element : 023"  # scripted group (container) (typed FeaturePython)
  n = 2
  ref = N_element
FEATURE [App::DocumentObjectGroupPython] G4_KEVLAR  # scripted group (container) (typed FeaturePython)
  Dunit = g/cm3
  Dvalue = 1.44
  Group = -> [C_element128,H_element118,O_element111,N_element050]
  conduct = 2
  density = 1
  expand = 3
  formula = G4_KEVLAR
  name = G4_KEVLAR
  specific = 4
FEATURE [App::DocumentObjectGroupPython] C_element129  label="C_element : 074"  # scripted group (container) (typed FeaturePython)
  n = 10
  ref = C_element
FEATURE [App::DocumentObjectGroupPython] H_element119  label="H_element : 066"  # scripted group (container) (typed FeaturePython)
  n = 8
  ref = H_element
FEATURE [App::DocumentObjectGroupPython] O_element112  label="O_element : 065"  # scripted group (container) (typed FeaturePython)
  n = 4
  ref = O_element
FEATURE [App::DocumentObjectGroupPython] G4_DACRON  # scripted group (container) (typed FeaturePython)
  Dunit = g/cm3
  Dvalue = 1.4
  Group = -> [C_element129,H_element119,O_element112]
  conduct = 2
  density = 1
  expand = 3
  formula = G4_DACRON
  name = G4_DACRON
  specific = 4
FEATURE [App::DocumentObjectGroupPython] C_element130  label="C_element : 075"  # scripted group (container) (typed FeaturePython)
  n = 4
  ref = C_element
FEATURE [App::DocumentObjectGroupPython] H_element120  label="H_element : 067"  # scripted group (container) (typed FeaturePython)
  n = 5
  ref = H_element
FEATURE [App::DocumentObjectGroupPython] Cl_element030  label="Cl_element : 016"  # scripted group (container) (typed FeaturePython)
  n = 1
  ref = Cl_element
FEATURE [App::DocumentObjectGroupPython] G4_NEOPRENE  # scripted group (container) (typed FeaturePython)
  Dunit = g/cm3
  Dvalue = 1.23
  Group = -> [C_element130,H_element120,Cl_element030]
  conduct = 2
  density = 1
  expand = 3
  formula = G4_NEOPRENE
  name = G4_NEOPRENE
  specific = 4
FEATURE [App::DocumentObjectGroupPython] Space  # scripted group (container) (typed FeaturePython)
  Group = -> [G4_KEVLAR,G4_DACRON,G4_NEOPRENE]
FEATURE [App::DocumentObjectGroupPython] H_element121  label="H_element : 068"  # scripted group (container) (typed FeaturePython)
  n = 5
  ref = H_element
FEATURE [App::DocumentObjectGroupPython] C_element131  label="C_element : 076"  # scripted group (container) (typed FeaturePython)
  n = 4
  ref = C_element
FEATURE [App::DocumentObjectGroupPython] N_element051  label="N_element : 3"  # scripted group (container) (typed FeaturePython)
  n = 3
  ref = N_element
FEATURE [App::DocumentObjectGroupPython] O_element113  label="O_element : 066"  # scripted group (container) (typed FeaturePython)
  n = 1
  ref = O_element
FEATURE [App::DocumentObjectGroupPython] G4_CYTOSINE  # scripted group (container) (typed FeaturePython)
  Dunit = g/cm3
  Dvalue = 1.55
  Group = -> [H_element121,C_element131,N_element051,O_element113]
  conduct = 2
  density = 1
  expand = 3
  formula = G4_CYTOSINE
  name = G4_CYTOSINE
  specific = 4
FEATURE [App::DocumentObjectGroupPython] H_element122  label="H_element : 069"  # scripted group (container) (typed FeaturePython)
  n = 6
  ref = H_element
FEATURE [App::DocumentObjectGroupPython] C_element132  label="C_element : 077"  # scripted group (container) (typed FeaturePython)
  n = 5
  ref = C_element
FEATURE [App::DocumentObjectGroupPython] N_element052  label="N_element : 024"  # scripted group (container) (typed FeaturePython)
  n = 2
  ref = N_element
FEATURE [App::DocumentObjectGroupPython] O_element114  label="O_element : 067"  # scripted group (container) (typed FeaturePython)
  n = 2
  ref = O_element
FEATURE [App::DocumentObjectGroupPython] G4_THYMINE  # scripted group (container) (typed FeaturePython)
  Dunit = g/cm3
  Dvalue = 1.23
  Group = -> [H_element122,C_element132,N_element052,O_element114]
  conduct = 2
  density = 1
  expand = 3
  formula = G4_THYMINE
  name = G4_THYMINE
  specific = 4
FEATURE [App::DocumentObjectGroupPython] H_element123  label="H_element : 070"  # scripted group (container) (typed FeaturePython)
  n = 4
  ref = H_element
FEATURE [App::DocumentObjectGroupPython] C_element133  label="C_element : 078"  # scripted group (container) (typed FeaturePython)
  n = 4
  ref = C_element
FEATURE [App::DocumentObjectGroupPython] N_element053  label="N_element : 025"  # scripted group (container) (typed FeaturePython)
  n = 2
  ref = N_element
FEATURE [App::DocumentObjectGroupPython] O_element115  label="O_element : 068"  # scripted group (container) (typed FeaturePython)
  n = 2
  ref = O_element
FEATURE [App::DocumentObjectGroupPython] G4_URACIL  # scripted group (container) (typed FeaturePython)
  Dunit = g/cm3
  Dvalue = 1.32
  Group = -> [H_element123,C_element133,N_element053,O_element115]
  conduct = 2
  density = 1
  expand = 3
  formula = G4_URACIL
  name = G4_URACIL
  specific = 4
FEATURE [App::DocumentObjectGroupPython] H_element124  label="H_element : 071"  # scripted group (container) (typed FeaturePython)
  n = 4
  ref = H_element
FEATURE [App::DocumentObjectGroupPython] C_element134  label="C_element : 079"  # scripted group (container) (typed FeaturePython)
  n = 5
  ref = C_element
FEATURE [App::DocumentObjectGroupPython] N_element054  label="N_element : 026"  # scripted group (container) (typed FeaturePython)
  n = 5
  ref = N_element
FEATURE [App::DocumentObjectGroupPython] G4_DNA_ADENINE  # scripted group (container) (typed FeaturePython)
  Dunit = g/cm3
  Dvalue = 1
  Group = -> [H_element124,C_element134,N_element054]
  conduct = 2
  density = 1
  expand = 3
  formula = G4_DNA_ADENINE
  name = G4_DNA_ADENINE
  specific = 4
FEATURE [App::DocumentObjectGroupPython] H_element125  label="H_element : 072"  # scripted group (container) (typed FeaturePython)
  n = 4
  ref = H_element
FEATURE [App::DocumentObjectGroupPython] C_element135  label="C_element : 080"  # scripted group (container) (typed FeaturePython)
  n = 5
  ref = C_element
FEATURE [App::DocumentObjectGroupPython] N_element055  label="N_element : 027"  # scripted group (container) (typed FeaturePython)
  n = 5
  ref = N_element
FEATURE [App::DocumentObjectGroupPython] O_element116  label="O_element : 069"  # scripted group (container) (typed FeaturePython)
  n = 1
  ref = O_element
FEATURE [App::DocumentObjectGroupPython] G4_DNA_GUANINE  # scripted group (container) (typed FeaturePython)
  Dunit = g/cm3
  Dvalue = 1
  Group = -> [H_element125,C_element135,N_element055,O_element116]
  conduct = 2
  density = 1
  expand = 3
  formula = G4_DNA_GUANINE
  name = G4_DNA_GUANINE
  specific = 4
FEATURE [App::DocumentObjectGroupPython] H_element126  label="H_element : 073"  # scripted group (container) (typed FeaturePython)
  n = 4
  ref = H_element
FEATURE [App::DocumentObjectGroupPython] C_element136  label="C_element : 081"  # scripted group (container) (typed FeaturePython)
  n = 4
  ref = C_element
FEATURE [App::DocumentObjectGroupPython] N_element056  label="N_element : 028"  # scripted group (container) (typed FeaturePython)
  n = 3
  ref = N_element
FEATURE [App::DocumentObjectGroupPython] O_element117  label="O_element : 070"  # scripted group (container) (typed FeaturePython)
  n = 1
  ref = O_element
FEATURE [App::DocumentObjectGroupPython] G4_DNA_CYTOSINE  # scripted group (container) (typed FeaturePython)
  Dunit = g/cm3
  Dvalue = 1
  Group = -> [H_element126,C_element136,N_element056,O_element117]
  conduct = 2
  density = 1
  expand = 3
  formula = G4_DNA_CYTOSINE
  name = G4_DNA_CYTOSINE
  specific = 4
FEATURE [App::DocumentObjectGroupPython] H_element127  label="H_element : 074"  # scripted group (container) (typed FeaturePython)
  n = 5
  ref = H_element
FEATURE [App::DocumentObjectGroupPython] C_element137  label="C_element : 082"  # scripted group (container) (typed FeaturePython)
  n = 5
  ref = C_element
FEATURE [App::DocumentObjectGroupPython] N_element057  label="N_element : 029"  # scripted group (container) (typed FeaturePython)
  n = 2
  ref = N_element
FEATURE [App::DocumentObjectGroupPython] O_element118  label="O_element : 071"  # scripted group (container) (typed FeaturePython)
  n = 2
  ref = O_element
FEATURE [App::DocumentObjectGroupPython] G4_DNA_THYMINE  # scripted group (container) (typed FeaturePython)
  Dunit = g/cm3
  Dvalue = 1
  Group = -> [H_element127,C_element137,N_element057,O_element118]
  conduct = 2
  density = 1
  expand = 3
  formula = G4_DNA_THYMINE
  name = G4_DNA_THYMINE
  specific = 4
FEATURE [App::DocumentObjectGroupPython] H_element128  label="H_element : 075"  # scripted group (container) (typed FeaturePython)
  n = 3
  ref = H_element
FEATURE [App::DocumentObjectGroupPython] C_element138  label="C_element : 083"  # scripted group (container) (typed FeaturePython)
  n = 4
  ref = C_element
FEATURE [App::DocumentObjectGroupPython] N_element058  label="N_element : 030"  # scripted group (container) (typed FeaturePython)
  n = 2
  ref = N_element
FEATURE [App::DocumentObjectGroupPython] O_element119  label="O_element : 072"  # scripted group (container) (typed FeaturePython)
  n = 2
  ref = O_element
FEATURE [App::DocumentObjectGroupPython] G4_DNA_URACIL  # scripted group (container) (typed FeaturePython)
  Dunit = g/cm3
  Dvalue = 1
  Group = -> [H_element128,C_element138,N_element058,O_element119]
  conduct = 2
  density = 1
  expand = 3
  formula = G4_DNA_URACIL
  name = G4_DNA_URACIL
  specific = 4
FEATURE [App::DocumentObjectGroupPython] H_element129  label="H_element : 076"  # scripted group (container) (typed FeaturePython)
  n = 10
  ref = H_element
FEATURE [App::DocumentObjectGroupPython] C_element139  label="C_element : 084"  # scripted group (container) (typed FeaturePython)
  n = 10
  ref = C_element
FEATURE [App::DocumentObjectGroupPython] N_element059  label="N_element : 031"  # scripted group (container) (typed FeaturePython)
  n = 5
  ref = N_element
FEATURE [App::DocumentObjectGroupPython] O_element120  label="O_element : 073"  # scripted group (container) (typed FeaturePython)
  n = 4
  ref = O_element
FEATURE [App::DocumentObjectGroupPython] G4_DNA_ADENOSINE  # scripted group (container) (typed FeaturePython)
  Dunit = g/cm3
  Dvalue = 1
  Group = -> [H_element129,C_element139,N_element059,O_element120]
  conduct = 2
  density = 1
  expand = 3
  formula = G4_DNA_ADENOSINE
  name = G4_DNA_ADENOSINE
  specific = 4
FEATURE [App::DocumentObjectGroupPython] H_element130  label="H_element : 077"  # scripted group (container) (typed FeaturePython)
  n = 10
  ref = H_element
FEATURE [App::DocumentObjectGroupPython] C_element140  label="C_element : 085"  # scripted group (container) (typed FeaturePython)
  n = 10
  ref = C_element
FEATURE [App::DocumentObjectGroupPython] N_element060  label="N_element : 032"  # scripted group (container) (typed FeaturePython)
  n = 5
  ref = N_element
FEATURE [App::DocumentObjectGroupPython] O_element121  label="O_element : 074"  # scripted group (container) (typed FeaturePython)
  n = 5
  ref = O_element
FEATURE [App::DocumentObjectGroupPython] G4_DNA_GUANOSINE  # scripted group (container) (typed FeaturePython)
  Dunit = g/cm3
  Dvalue = 1
  Group = -> [H_element130,C_element140,N_element060,O_element121]
  conduct = 2
  density = 1
  expand = 3
  formula = G4_DNA_GUANOSINE
  name = G4_DNA_GUANOSINE
  specific = 4
FEATURE [App::DocumentObjectGroupPython] H_element131  label="H_element : 078"  # scripted group (container) (typed FeaturePython)
  n = 10
  ref = H_element
FEATURE [App::DocumentObjectGroupPython] C_element141  label="C_element : 086"  # scripted group (container) (typed FeaturePython)
  n = 9
  ref = C_element
FEATURE [App::DocumentObjectGroupPython] N_element061  label="N_element : 033"  # scripted group (container) (typed FeaturePython)
  n = 3
  ref = N_element
FEATURE [App::DocumentObjectGroupPython] O_element122  label="O_element : 075"  # scripted group (container) (typed FeaturePython)
  n = 5
  ref = O_element
FEATURE [App::DocumentObjectGroupPython] G4_DNA_CYTIDINE  # scripted group (container) (typed FeaturePython)
  Dunit = g/cm3
  Dvalue = 1
  Group = -> [H_element131,C_element141,N_element061,O_element122]
  conduct = 2
  density = 1
  expand = 3
  formula = G4_DNA_CYTIDINE
  name = G4_DNA_CYTIDINE
  specific = 4
FEATURE [App::DocumentObjectGroupPython] H_element132  label="H_element : 079"  # scripted group (container) (typed FeaturePython)
  n = 9
  ref = H_element
FEATURE [App::DocumentObjectGroupPython] C_element142  label="C_element : 087"  # scripted group (container) (typed FeaturePython)
  n = 9
  ref = C_element
FEATURE [App::DocumentObjectGroupPython] N_element062  label="N_element : 034"  # scripted group (container) (typed FeaturePython)
  n = 2
  ref = N_element
FEATURE [App::DocumentObjectGroupPython] O_element123  label="O_element : 076"  # scripted group (container) (typed FeaturePython)
  n = 6
  ref = O_element
FEATURE [App::DocumentObjectGroupPython] G4_DNA_URIDINE  # scripted group (container) (typed FeaturePython)
  Dunit = g/cm3
  Dvalue = 1
  Group = -> [H_element132,C_element142,N_element062,O_element123]
  conduct = 2
  density = 1
  expand = 3
  formula = G4_DNA_URIDINE
  name = G4_DNA_URIDINE
  specific = 4
FEATURE [App::DocumentObjectGroupPython] H_element133  label="H_element : 080"  # scripted group (container) (typed FeaturePython)
  n = 11
  ref = H_element
FEATURE [App::DocumentObjectGroupPython] C_element143  label="C_element : 088"  # scripted group (container) (typed FeaturePython)
  n = 10
  ref = C_element
FEATURE [App::DocumentObjectGroupPython] N_element063  label="N_element : 035"  # scripted group (container) (typed FeaturePython)
  n = 2
  ref = N_element
FEATURE [App::DocumentObjectGroupPython] O_element124  label="O_element : 077"  # scripted group (container) (typed FeaturePython)
  n = 6
  ref = O_element
FEATURE [App::DocumentObjectGroupPython] G4_DNA_METHYLURIDINE  # scripted group (container) (typed FeaturePython)
  Dunit = g/cm3
  Dvalue = 1
  Group = -> [H_element133,C_element143,N_element063,O_element124]
  conduct = 2
  density = 1
  expand = 3
  formula = G4_DNA_METHYLURIDINE
  name = G4_DNA_METHYLURIDINE
  specific = 4
FEATURE [App::DocumentObjectGroupPython] P_element014  label="P_element : 003"  # scripted group (container) (typed FeaturePython)
  n = 1
  ref = P_element
FEATURE [App::DocumentObjectGroupPython] O_element125  label="O_element : 078"  # scripted group (container) (typed FeaturePython)
  n = 3
  ref = O_element
FEATURE [App::DocumentObjectGroupPython] G4_DNA_MONOPHOSPHATE  # scripted group (container) (typed FeaturePython)
  Dunit = g/cm3
  Dvalue = 1
  Group = -> [P_element014,O_element125]
  conduct = 2
  density = 1
  expand = 3
  formula = G4_DNA_MONOPHOSPHATE
  name = G4_DNA_MONOPHOSPHATE
  specific = 4
FEATURE [App::DocumentObjectGroupPython] H_element134  label="H_element : 081"  # scripted group (container) (typed FeaturePython)
  n = 10
  ref = H_element
FEATURE [App::DocumentObjectGroupPython] C_element144  label="C_element : 089"  # scripted group (container) (typed FeaturePython)
  n = 10
  ref = C_element
FEATURE [App::DocumentObjectGroupPython] N_element064  label="N_element : 036"  # scripted group (container) (typed FeaturePython)
  n = 5
  ref = N_element
FEATURE [App::DocumentObjectGroupPython] O_element126  label="O_element : 079"  # scripted group (container) (typed FeaturePython)
  n = 7
  ref = O_element
FEATURE [App::DocumentObjectGroupPython] P_element015  label="P_element : 004"  # scripted group (container) (typed FeaturePython)
  n = 1
  ref = P_element
FEATURE [App::DocumentObjectGroupPython] G4_DNA_A  # scripted group (container) (typed FeaturePython)
  Dunit = g/cm3
  Dvalue = 1
  Group = -> [H_element134,C_element144,N_element064,O_element126,P_element015]
  conduct = 2
  density = 1
  expand = 3
  formula = G4_DNA_A
  name = G4_DNA_A
  specific = 4
FEATURE [App::DocumentObjectGroupPython] H_element135  label="H_element : 082"  # scripted group (container) (typed FeaturePython)
  n = 10
  ref = H_element
FEATURE [App::DocumentObjectGroupPython] C_element145  label="C_element : 090"  # scripted group (container) (typed FeaturePython)
  n = 10
  ref = C_element
FEATURE [App::DocumentObjectGroupPython] N_element065  label="N_element : 037"  # scripted group (container) (typed FeaturePython)
  n = 5
  ref = N_element
FEATURE [App::DocumentObjectGroupPython] O_element127  label="O_element : 8"  # scripted group (container) (typed FeaturePython)
  n = 8
  ref = O_element
FEATURE [App::DocumentObjectGroupPython] P_element016  label="P_element : 005"  # scripted group (container) (typed FeaturePython)
  n = 1
  ref = P_element
FEATURE [App::DocumentObjectGroupPython] G4_DNA_G  # scripted group (container) (typed FeaturePython)
  Dunit = g/cm3
  Dvalue = 1
  Group = -> [H_element135,C_element145,N_element065,O_element127,P_element016]
  conduct = 2
  density = 1
  expand = 3
  formula = G4_DNA_G
  name = G4_DNA_G
  specific = 4
FEATURE [App::DocumentObjectGroupPython] H_element136  label="H_element : 083"  # scripted group (container) (typed FeaturePython)
  n = 10
  ref = H_element
FEATURE [App::DocumentObjectGroupPython] C_element146  label="C_element : 091"  # scripted group (container) (typed FeaturePython)
  n = 9
  ref = C_element
FEATURE [App::DocumentObjectGroupPython] N_element066  label="N_element : 038"  # scripted group (container) (typed FeaturePython)
  n = 3
  ref = N_element
FEATURE [App::DocumentObjectGroupPython] O_element128  label="O_element : 080"  # scripted group (container) (typed FeaturePython)
  n = 8
  ref = O_element
FEATURE [App::DocumentObjectGroupPython] P_element017  label="P_element : 006"  # scripted group (container) (typed FeaturePython)
  n = 1
  ref = P_element
FEATURE [App::DocumentObjectGroupPython] G4_DNA_C  # scripted group (container) (typed FeaturePython)
  Dunit = g/cm3
  Dvalue = 1
  Group = -> [H_element136,C_element146,N_element066,O_element128,P_element017]
  conduct = 2
  density = 1
  expand = 3
  formula = G4_DNA_C
  name = G4_DNA_C
  specific = 4
FEATURE [App::DocumentObjectGroupPython] H_element137  label="H_element : 084"  # scripted group (container) (typed FeaturePython)
  n = 9
  ref = H_element
FEATURE [App::DocumentObjectGroupPython] C_element147  label="C_element : 092"  # scripted group (container) (typed FeaturePython)
  n = 9
  ref = C_element
FEATURE [App::DocumentObjectGroupPython] N_element067  label="N_element : 039"  # scripted group (container) (typed FeaturePython)
  n = 2
  ref = N_element
FEATURE [App::DocumentObjectGroupPython] O_element129  label="O_element : 9"  # scripted group (container) (typed FeaturePython)
  n = 9
  ref = O_element
FEATURE [App::DocumentObjectGroupPython] P_element018  label="P_element : 007"  # scripted group (container) (typed FeaturePython)
  n = 1
  ref = P_element
FEATURE [App::DocumentObjectGroupPython] G4_DNA_U  # scripted group (container) (typed FeaturePython)
  Dunit = g/cm3
  Dvalue = 1
  Group = -> [H_element137,C_element147,N_element067,O_element129,P_element018]
  conduct = 2
  density = 1
  expand = 3
  formula = G4_DNA_U
  name = G4_DNA_U
  specific = 4
FEATURE [App::DocumentObjectGroupPython] H_element138  label="H_element : 085"  # scripted group (container) (typed FeaturePython)
  n = 11
  ref = H_element
FEATURE [App::DocumentObjectGroupPython] C_element148  label="C_element : 093"  # scripted group (container) (typed FeaturePython)
  n = 10
  ref = C_element
FEATURE [App::DocumentObjectGroupPython] N_element068  label="N_element : 040"  # scripted group (container) (typed FeaturePython)
  n = 2
  ref = N_element
FEATURE [App::DocumentObjectGroupPython] O_element130  label="O_element : 081"  # scripted group (container) (typed FeaturePython)
  n = 9
  ref = O_element
FEATURE [App::DocumentObjectGroupPython] P_element019  label="P_element : 008"  # scripted group (container) (typed FeaturePython)
  n = 1
  ref = P_element
FEATURE [App::DocumentObjectGroupPython] G4_DNA_MU  # scripted group (container) (typed FeaturePython)
  Dunit = g/cm3
  Dvalue = 1
  Group = -> [H_element138,C_element148,N_element068,O_element130,P_element019]
  conduct = 2
  density = 1
  expand = 3
  formula = G4_DNA_MU
  name = G4_DNA_MU
  specific = 4
FEATURE [App::DocumentObjectGroupPython] BioChemical  # scripted group (container) (typed FeaturePython)
  Group = -> [G4_CYTOSINE,G4_THYMINE,G4_URACIL,G4_DNA_ADENINE,G4_DNA_GUANINE,G4_DNA_CYTOSINE,G4_DNA_THYMINE,G4_DNA_URACIL,G4_DNA_ADENOSINE,G4_DNA_GUANOSINE,G4_DNA_CYTIDINE,G4_DNA_URIDINE,G4_DNA_METHYLURIDINE,G4_DNA_MONOPHOSPHATE,G4_DNA_A,G4_DNA_G,G4_DNA_C,G4_DNA_U,G4_DNA_MU]
FEATURE [App::DocumentObjectGroupPython] G4Materials  # scripted group (container) (typed FeaturePython)
  Group = -> [NIST,Element,HEP,Space,BioChemical]
  version = 1
FEATURE [App::DocumentObjectGroupPython] Geant4  # scripted group (container) (typed FeaturePython)
  Group = -> [G4Isotopes,G4Elements,G4Materials]
FEATURE [App::DocumentObjectGroupPython] Materials  # scripted group (container) (typed FeaturePython)
  Group = -> [Geant4]
FEATURE [Part::FeaturePython] GDMLBox_WorldBox  # WARN: FeaturePython — macro-defined, semantics opaque (R4)
  lunit = 2
  material = 5
  x = 200
  y = 200
  z = 200
FEATURE [Part::FeaturePython] GDMLSphere_Sphere  # WARN: FeaturePython — macro-defined, semantics opaque (R4)
  Placement = pos=(20,0,0) rot=(0,0,1;0rad)
  aunit = 0
  deltaphi = 2.02
  deltatheta = 2.02
  lunit = 2
  material = 18
  rmax = 20
  rmin = 10
  startphi = 0
  starttheta = 0
FEATURE [Part::FeaturePython] GDMLTorus_Torus  # WARN: FeaturePython — macro-defined, semantics opaque (R4)
  aunit = deg
  deltaphi = 360
  lunit = 2
  material = 5
  rmax = 5
  rmin = 0
  rtor = 10
  startphi = 10
FEATURE [Part::MultiFuse] Fusion
  Placement = pos=(30,0,0) rot=(0,0,1;0rad)
  Shapes = -> [GDMLSphere_Sphere,GDMLTorus_Torus]
  material = 18
FEATURE [Part::FeaturePython] Array  # Draft array (typed FeaturePython)
  Angle = 360
  ArrayType = 1
  Axis = (0,0,1)
  Base = -> Fusion
  Center = (0,0,0)
  Count = 5
  Fuse = false
  IntervalAxis = (0,0,0)
  IntervalX = (50,0,0)
  IntervalY = (0,50,0)
  IntervalZ = (0,0,50)
  NumberCircles = 3
  NumberPolar = 5
  NumberX = 2
  NumberY = 2
  NumberZ = 1
  RadialDistance = 50
  Symmetry = 1
  TangentialDistance = 25
  material = 261
FEATURE [App::Part] Part
  Group = -> [GDMLSphere_Sphere,GDMLTorus_Torus,Fusion,Array]
  Origin = -> Origin001
FEATURE [App::Part] worldVOL
  Group = -> [GDMLBox_WorldBox,Part]
  Origin = -> Origin
